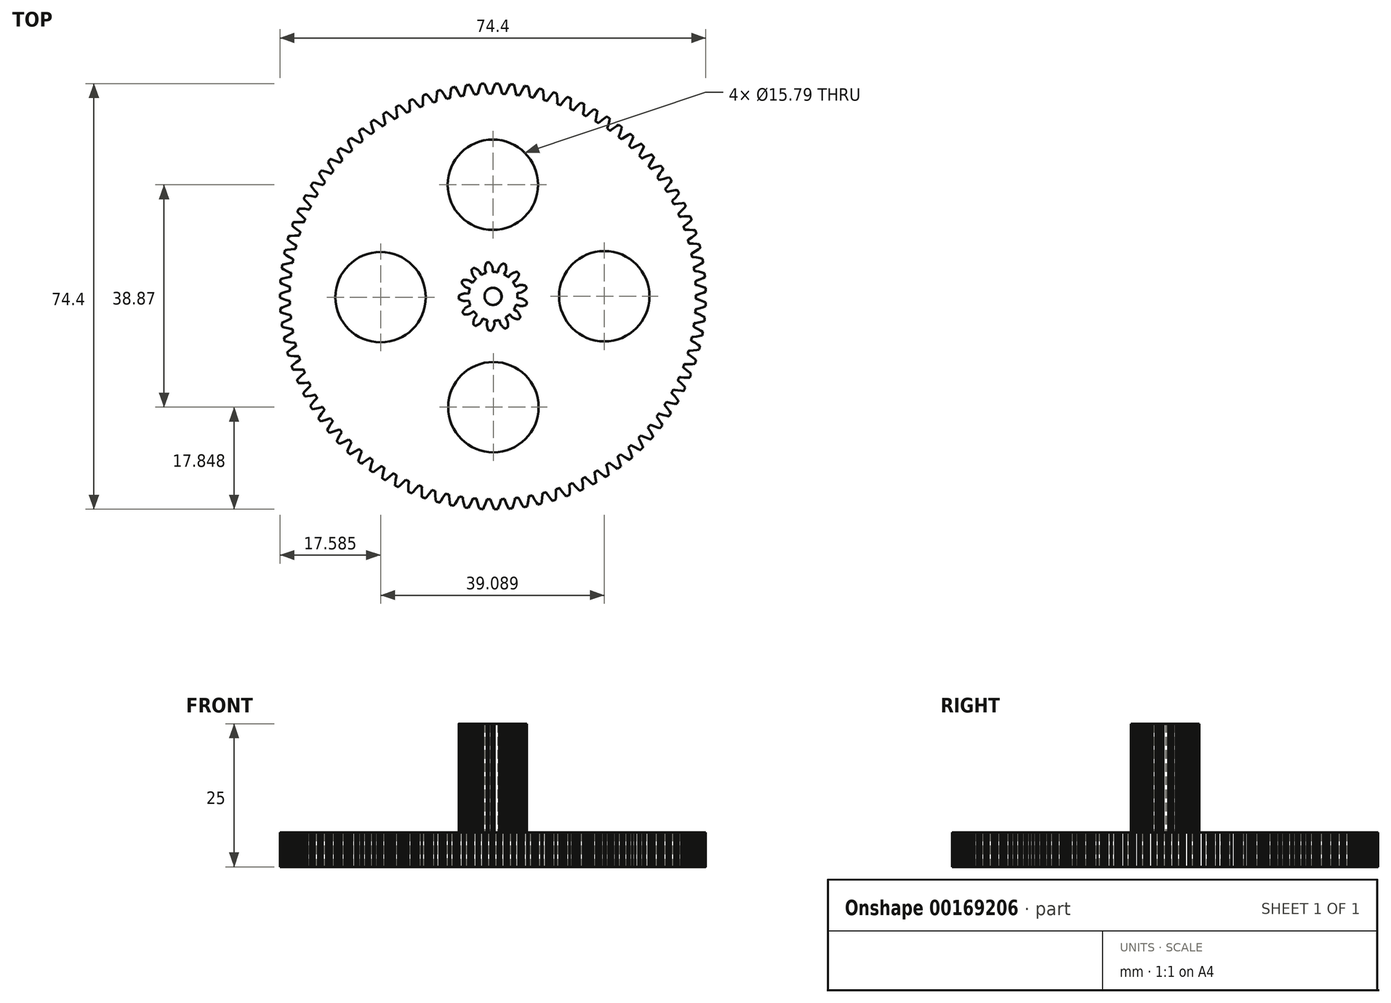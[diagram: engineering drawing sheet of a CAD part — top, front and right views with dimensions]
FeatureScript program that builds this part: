
annotation { "Feature Type Name" : "Feature", "Feature Type Description" : "" }
export const myFeature = defineFeature(function(context is Context, id is Id, definition is map)
    precondition{}
    {
        {
            assignVariable(context, id + "F0", {"name" : "Gear1", "anyValue" : 25});
        }
        {
            var Q0;
            Q0=qCreatedBy(makeId("Top.planeOp"),FACE);
            var sketch = newSketch(context, id + "F1", { "sketchPlane" : qUnion([Q0])});
            skCircle(sketch, "E0", {"center": v(0, 0) * mm, "radius": 1.5 * mm});
            skLineSegment(sketch, "E1", {"start": v(27.62, 22.27) * mm, "end": v(27.85, 22.37) * mm});
            skLineSegment(sketch, "E2", {"start": v(27.85, 22.37) * mm, "end": v(28.37, 22.56) * mm});
            skLineSegment(sketch, "E3", {"start": v(28.37, 22.56) * mm, "end": v(28.98, 22.76) * mm});
            skLineSegment(sketch, "E4", {"start": v(28.98, 22.76) * mm, "end": v(29.35, 22.86) * mm});
            skArc(sketch, "E5", {"start": v(29.35, 22.86) * mm, "mid": v(29.55, 22.6) * mm, "end": v(29.74, 22.35) * mm});
            skLineSegment(sketch, "E6", {"start": v(29.74, 22.35) * mm, "end": v(29.55, 22.01) * mm});
            skLineSegment(sketch, "E7", {"start": v(29.55, 22.01) * mm, "end": v(29.2, 21.47) * mm});
            skLineSegment(sketch, "E8", {"start": v(29.2, 21.47) * mm, "end": v(28.87, 21.02) * mm});
            skLineSegment(sketch, "E9", {"start": v(28.87, 21.02) * mm, "end": v(28.72, 20.83) * mm});
            skArc(sketch, "E10", {"start": v(28.72, 20.83) * mm, "mid": v(28.9, 20.57) * mm, "end": v(29.1, 20.3) * mm});
            skLineSegment(sketch, "E11", {"start": v(29.1, 20.3) * mm, "end": v(29.32, 20.4) * mm});
            skLineSegment(sketch, "E12", {"start": v(29.32, 20.4) * mm, "end": v(29.85, 20.55) * mm});
            skLineSegment(sketch, "E13", {"start": v(29.85, 20.55) * mm, "end": v(30.48, 20.7) * mm});
            skLineSegment(sketch, "E14", {"start": v(30.48, 20.7) * mm, "end": v(30.86, 20.78) * mm});
            skArc(sketch, "E15", {"start": v(30.86, 20.78) * mm, "mid": v(31.04, 20.51) * mm, "end": v(31.21, 20.24) * mm});
            skLineSegment(sketch, "E16", {"start": v(31.21, 20.24) * mm, "end": v(31, 19.92) * mm});
            skLineSegment(sketch, "E17", {"start": v(31, 19.92) * mm, "end": v(30.61, 19.4) * mm});
            skLineSegment(sketch, "E18", {"start": v(30.61, 19.4) * mm, "end": v(30.26, 18.98) * mm});
            skLineSegment(sketch, "E19", {"start": v(30.26, 18.98) * mm, "end": v(30.09, 18.8) * mm});
            skArc(sketch, "E20", {"start": v(30.09, 18.8) * mm, "mid": v(30.26, 18.53) * mm, "end": v(30.42, 18.25) * mm});
            skLineSegment(sketch, "E21", {"start": v(30.42, 18.25) * mm, "end": v(30.66, 18.32) * mm});
            skLineSegment(sketch, "E22", {"start": v(30.66, 18.32) * mm, "end": v(31.2, 18.44) * mm});
            skLineSegment(sketch, "E23", {"start": v(31.2, 18.44) * mm, "end": v(31.83, 18.55) * mm});
            skLineSegment(sketch, "E24", {"start": v(31.83, 18.55) * mm, "end": v(32.22, 18.6) * mm});
            skArc(sketch, "E25", {"start": v(32.22, 18.6) * mm, "mid": v(32.38, 18.32) * mm, "end": v(32.54, 18.04) * mm});
            skLineSegment(sketch, "E26", {"start": v(32.54, 18.04) * mm, "end": v(32.3, 17.73) * mm});
            skLineSegment(sketch, "E27", {"start": v(32.3, 17.73) * mm, "end": v(31.88, 17.25) * mm});
            skLineSegment(sketch, "E28", {"start": v(31.88, 17.25) * mm, "end": v(31.5, 16.85) * mm});
            skLineSegment(sketch, "E29", {"start": v(31.5, 16.85) * mm, "end": v(31.31, 16.68) * mm});
            skArc(sketch, "E30", {"start": v(31.31, 16.68) * mm, "mid": v(31.46, 16.4) * mm, "end": v(31.6, 16.11) * mm});
            skLineSegment(sketch, "E31", {"start": v(31.6, 16.11) * mm, "end": v(31.85, 16.16) * mm});
            skLineSegment(sketch, "E32", {"start": v(31.85, 16.16) * mm, "end": v(32.4, 16.25) * mm});
            skLineSegment(sketch, "E33", {"start": v(32.4, 16.25) * mm, "end": v(33.04, 16.31) * mm});
            skLineSegment(sketch, "E34", {"start": v(33.04, 16.31) * mm, "end": v(33.43, 16.33) * mm});
            skArc(sketch, "E35", {"start": v(33.43, 16.33) * mm, "mid": v(33.57, 16.04) * mm, "end": v(33.7, 15.76) * mm});
            skLineSegment(sketch, "E36", {"start": v(33.7, 15.76) * mm, "end": v(33.44, 15.46) * mm});
            skLineSegment(sketch, "E37", {"start": v(33.44, 15.46) * mm, "end": v(33, 15) * mm});
            skLineSegment(sketch, "E38", {"start": v(33, 15) * mm, "end": v(32.58, 14.63) * mm});
            skLineSegment(sketch, "E39", {"start": v(32.58, 14.63) * mm, "end": v(32.4, 14.48) * mm});
            skArc(sketch, "E40", {"start": v(32.4, 14.48) * mm, "mid": v(32.52, 14.19) * mm, "end": v(32.65, 13.9) * mm});
            skLineSegment(sketch, "E41", {"start": v(32.65, 13.9) * mm, "end": v(32.89, 13.93) * mm});
            skLineSegment(sketch, "E42", {"start": v(32.89, 13.93) * mm, "end": v(33.44, 13.97) * mm});
            skLineSegment(sketch, "E43", {"start": v(33.44, 13.97) * mm, "end": v(34.08, 14) * mm});
            skLineSegment(sketch, "E44", {"start": v(34.08, 14) * mm, "end": v(34.48, 13.99) * mm});
            skArc(sketch, "E45", {"start": v(34.48, 13.99) * mm, "mid": v(34.6, 13.7) * mm, "end": v(34.71, 13.4) * mm});
            skLineSegment(sketch, "E46", {"start": v(34.71, 13.4) * mm, "end": v(34.43, 13.12) * mm});
            skLineSegment(sketch, "E47", {"start": v(34.43, 13.12) * mm, "end": v(33.95, 12.7) * mm});
            skLineSegment(sketch, "E48", {"start": v(33.95, 12.7) * mm, "end": v(33.51, 12.35) * mm});
            skLineSegment(sketch, "E49", {"start": v(33.51, 12.35) * mm, "end": v(33.31, 12.2) * mm});
            skArc(sketch, "E50", {"start": v(33.31, 12.2) * mm, "mid": v(33.42, 11.9) * mm, "end": v(33.53, 11.6) * mm});
            skLineSegment(sketch, "E51", {"start": v(33.53, 11.6) * mm, "end": v(33.77, 11.62) * mm});
            skLineSegment(sketch, "E52", {"start": v(33.77, 11.62) * mm, "end": v(34.33, 11.63) * mm});
            skLineSegment(sketch, "E53", {"start": v(34.33, 11.63) * mm, "end": v(34.97, 11.61) * mm});
            skLineSegment(sketch, "E54", {"start": v(34.97, 11.61) * mm, "end": v(35.36, 11.58) * mm});
            skArc(sketch, "E55", {"start": v(35.36, 11.58) * mm, "mid": v(35.46, 11.27) * mm, "end": v(35.55, 10.97) * mm});
            skLineSegment(sketch, "E56", {"start": v(35.55, 10.97) * mm, "end": v(35.25, 10.71) * mm});
            skLineSegment(sketch, "E57", {"start": v(35.25, 10.71) * mm, "end": v(34.74, 10.33) * mm});
            skLineSegment(sketch, "E58", {"start": v(34.74, 10.33) * mm, "end": v(34.28, 10.01) * mm});
            skLineSegment(sketch, "E59", {"start": v(34.28, 10.01) * mm, "end": v(34.08, 9.88) * mm});
            skArc(sketch, "E60", {"start": v(34.08, 9.88) * mm, "mid": v(34.16, 9.58) * mm, "end": v(34.25, 9.27) * mm});
            skLineSegment(sketch, "E61", {"start": v(34.25, 9.27) * mm, "end": v(34.5, 9.27) * mm});
            skLineSegment(sketch, "E62", {"start": v(34.5, 9.27) * mm, "end": v(35.05, 9.24) * mm});
            skLineSegment(sketch, "E63", {"start": v(35.05, 9.24) * mm, "end": v(35.69, 9.17) * mm});
            skLineSegment(sketch, "E64", {"start": v(35.69, 9.17) * mm, "end": v(36.07, 9.11) * mm});
            skArc(sketch, "E65", {"start": v(36.07, 9.11) * mm, "mid": v(36.15, 8.8) * mm, "end": v(36.22, 8.49) * mm});
            skLineSegment(sketch, "E66", {"start": v(36.22, 8.49) * mm, "end": v(35.9, 8.26) * mm});
            skLineSegment(sketch, "E67", {"start": v(35.9, 8.26) * mm, "end": v(35.37, 7.9) * mm});
            skLineSegment(sketch, "E68", {"start": v(35.37, 7.9) * mm, "end": v(34.9, 7.62) * mm});
            skLineSegment(sketch, "E69", {"start": v(34.9, 7.62) * mm, "end": v(34.68, 7.5) * mm});
            skArc(sketch, "E70", {"start": v(34.68, 7.5) * mm, "mid": v(34.74, 7.2) * mm, "end": v(34.8, 6.88) * mm});
            skLineSegment(sketch, "E71", {"start": v(34.8, 6.88) * mm, "end": v(35.05, 6.87) * mm});
            skLineSegment(sketch, "E72", {"start": v(35.05, 6.87) * mm, "end": v(35.6, 6.8) * mm});
            skLineSegment(sketch, "E73", {"start": v(35.6, 6.8) * mm, "end": v(36.23, 6.69) * mm});
            skLineSegment(sketch, "E74", {"start": v(36.23, 6.69) * mm, "end": v(36.61, 6.6) * mm});
            skArc(sketch, "E75", {"start": v(36.61, 6.6) * mm, "mid": v(36.67, 6.28) * mm, "end": v(36.72, 5.97) * mm});
            skLineSegment(sketch, "E76", {"start": v(36.72, 5.97) * mm, "end": v(36.4, 5.76) * mm});
            skLineSegment(sketch, "E77", {"start": v(36.4, 5.76) * mm, "end": v(35.83, 5.45) * mm});
            skLineSegment(sketch, "E78", {"start": v(35.83, 5.45) * mm, "end": v(35.34, 5.2) * mm});
            skLineSegment(sketch, "E79", {"start": v(35.34, 5.2) * mm, "end": v(35.11, 5.1) * mm});
            skArc(sketch, "E80", {"start": v(35.11, 5.1) * mm, "mid": v(35.16, 4.78) * mm, "end": v(35.2, 4.47) * mm});
            skLineSegment(sketch, "E81", {"start": v(35.2, 4.47) * mm, "end": v(35.44, 4.43) * mm});
            skLineSegment(sketch, "E82", {"start": v(35.44, 4.43) * mm, "end": v(35.99, 4.33) * mm});
            skLineSegment(sketch, "E83", {"start": v(35.99, 4.33) * mm, "end": v(36.6, 4.17) * mm});
            skLineSegment(sketch, "E84", {"start": v(36.6, 4.17) * mm, "end": v(36.98, 4.06) * mm});
            skArc(sketch, "E85", {"start": v(36.98, 4.06) * mm, "mid": v(37.02, 3.74) * mm, "end": v(37.05, 3.42) * mm});
            skLineSegment(sketch, "E86", {"start": v(37.05, 3.42) * mm, "end": v(36.7, 3.24) * mm});
            skLineSegment(sketch, "E87", {"start": v(36.7, 3.24) * mm, "end": v(36.12, 2.96) * mm});
            skLineSegment(sketch, "E88", {"start": v(36.12, 2.96) * mm, "end": v(35.61, 2.75) * mm});
            skLineSegment(sketch, "E89", {"start": v(35.61, 2.75) * mm, "end": v(35.38, 2.66) * mm});
            skArc(sketch, "E90", {"start": v(35.38, 2.66) * mm, "mid": v(35.4, 2.35) * mm, "end": v(35.42, 2.03) * mm});
            skLineSegment(sketch, "E91", {"start": v(35.42, 2.03) * mm, "end": v(35.66, 1.98) * mm});
            skLineSegment(sketch, "E92", {"start": v(35.66, 1.98) * mm, "end": v(36.2, 1.83) * mm});
            skLineSegment(sketch, "E93", {"start": v(36.2, 1.83) * mm, "end": v(36.8, 1.64) * mm});
            skLineSegment(sketch, "E94", {"start": v(36.8, 1.64) * mm, "end": v(37.17, 1.5) * mm});
            skArc(sketch, "E95", {"start": v(37.17, 1.5) * mm, "mid": v(37.19, 1.18) * mm, "end": v(37.2, 0.86) * mm});
            skLineSegment(sketch, "E96", {"start": v(37.2, 0.86) * mm, "end": v(36.84, 0.7) * mm});
            skLineSegment(sketch, "E97", {"start": v(36.84, 0.7) * mm, "end": v(36.24, 0.46) * mm});
            skLineSegment(sketch, "E98", {"start": v(36.24, 0.46) * mm, "end": v(35.71, 0.28) * mm});
            skLineSegment(sketch, "E99", {"start": v(35.71, 0.28) * mm, "end": v(35.48, 0.22) * mm});
            skArc(sketch, "E100", {"start": v(35.48, 0.22) * mm, "mid": v(35.48, -0.1) * mm, "end": v(35.48, -0.42) * mm});
            skLineSegment(sketch, "E101", {"start": v(35.48, -0.42) * mm, "end": v(35.71, -0.49) * mm});
            skLineSegment(sketch, "E102", {"start": v(35.71, -0.49) * mm, "end": v(36.24, -0.67) * mm});
            skLineSegment(sketch, "E103", {"start": v(36.24, -0.67) * mm, "end": v(36.83, -0.9) * mm});
            skLineSegment(sketch, "E104", {"start": v(36.83, -0.9) * mm, "end": v(37.19, -1.07) * mm});
            skArc(sketch, "E105", {"start": v(37.19, -1.07) * mm, "mid": v(37.18, -1.4) * mm, "end": v(37.17, -1.71) * mm});
            skLineSegment(sketch, "E106", {"start": v(37.17, -1.71) * mm, "end": v(36.8, -1.85) * mm});
            skLineSegment(sketch, "E107", {"start": v(36.8, -1.85) * mm, "end": v(36.19, -2.04) * mm});
            skLineSegment(sketch, "E108", {"start": v(36.19, -2.04) * mm, "end": v(35.65, -2.18) * mm});
            skLineSegment(sketch, "E109", {"start": v(35.65, -2.18) * mm, "end": v(35.4, -2.23) * mm});
            skArc(sketch, "E110", {"start": v(35.4, -2.23) * mm, "mid": v(35.39, -2.55) * mm, "end": v(35.36, -2.87) * mm});
            skLineSegment(sketch, "E111", {"start": v(35.36, -2.87) * mm, "end": v(35.6, -2.95) * mm});
            skLineSegment(sketch, "E112", {"start": v(35.6, -2.95) * mm, "end": v(36.1, -3.17) * mm});
            skLineSegment(sketch, "E113", {"start": v(36.1, -3.17) * mm, "end": v(36.68, -3.45) * mm});
            skLineSegment(sketch, "E114", {"start": v(36.68, -3.45) * mm, "end": v(37.03, -3.63) * mm});
            skArc(sketch, "E115", {"start": v(37.03, -3.63) * mm, "mid": v(37, -3.95) * mm, "end": v(36.96, -4.27) * mm});
            skLineSegment(sketch, "E116", {"start": v(36.96, -4.27) * mm, "end": v(36.58, -4.38) * mm});
            skLineSegment(sketch, "E117", {"start": v(36.58, -4.38) * mm, "end": v(35.96, -4.53) * mm});
            skLineSegment(sketch, "E118", {"start": v(35.96, -4.53) * mm, "end": v(35.41, -4.63) * mm});
            skLineSegment(sketch, "E119", {"start": v(35.41, -4.63) * mm, "end": v(35.17, -4.67) * mm});
            skArc(sketch, "E120", {"start": v(35.17, -4.67) * mm, "mid": v(35.13, -4.98) * mm, "end": v(35.08, -5.3) * mm});
            skLineSegment(sketch, "E121", {"start": v(35.08, -5.3) * mm, "end": v(35.3, -5.4) * mm});
            skLineSegment(sketch, "E122", {"start": v(35.3, -5.4) * mm, "end": v(35.8, -5.65) * mm});
            skLineSegment(sketch, "E123", {"start": v(35.8, -5.65) * mm, "end": v(36.36, -5.97) * mm});
            skLineSegment(sketch, "E124", {"start": v(36.36, -5.97) * mm, "end": v(36.69, -6.18) * mm});
            skArc(sketch, "E125", {"start": v(36.69, -6.18) * mm, "mid": v(36.63, -6.5) * mm, "end": v(36.58, -6.8) * mm});
            skLineSegment(sketch, "E126", {"start": v(36.58, -6.8) * mm, "end": v(36.2, -6.9) * mm});
            skLineSegment(sketch, "E127", {"start": v(36.2, -6.9) * mm, "end": v(35.56, -7) * mm});
            skLineSegment(sketch, "E128", {"start": v(35.56, -7) * mm, "end": v(35, -7.07) * mm});
            skLineSegment(sketch, "E129", {"start": v(35, -7.07) * mm, "end": v(34.76, -7.08) * mm});
            skArc(sketch, "E130", {"start": v(34.76, -7.08) * mm, "mid": v(34.7, -7.4) * mm, "end": v(34.63, -7.7) * mm});
            skLineSegment(sketch, "E131", {"start": v(34.63, -7.7) * mm, "end": v(34.85, -7.82) * mm});
            skLineSegment(sketch, "E132", {"start": v(34.85, -7.82) * mm, "end": v(35.33, -8.1) * mm});
            skLineSegment(sketch, "E133", {"start": v(35.33, -8.1) * mm, "end": v(35.86, -8.46) * mm});
            skLineSegment(sketch, "E134", {"start": v(35.86, -8.46) * mm, "end": v(36.17, -8.7) * mm});
            skArc(sketch, "E135", {"start": v(36.17, -8.7) * mm, "mid": v(36.1, -9) * mm, "end": v(36.02, -9.32) * mm});
            skLineSegment(sketch, "E136", {"start": v(36.02, -9.32) * mm, "end": v(35.63, -9.37) * mm});
            skLineSegment(sketch, "E137", {"start": v(35.63, -9.37) * mm, "end": v(35, -9.44) * mm});
            skLineSegment(sketch, "E138", {"start": v(35, -9.44) * mm, "end": v(34.44, -9.46) * mm});
            skLineSegment(sketch, "E139", {"start": v(34.44, -9.46) * mm, "end": v(34.2, -9.46) * mm});
            skArc(sketch, "E140", {"start": v(34.2, -9.46) * mm, "mid": v(34.1, -9.77) * mm, "end": v(34.02, -10.08) * mm});
            skLineSegment(sketch, "E141", {"start": v(34.02, -10.08) * mm, "end": v(34.23, -10.2) * mm});
            skLineSegment(sketch, "E142", {"start": v(34.23, -10.2) * mm, "end": v(34.68, -10.52) * mm});
            skLineSegment(sketch, "E143", {"start": v(34.68, -10.52) * mm, "end": v(35.2, -10.91) * mm});
            skLineSegment(sketch, "E144", {"start": v(35.2, -10.91) * mm, "end": v(35.49, -11.17) * mm});
            skArc(sketch, "E145", {"start": v(35.49, -11.17) * mm, "mid": v(35.4, -11.47) * mm, "end": v(35.3, -11.78) * mm});
            skLineSegment(sketch, "E146", {"start": v(35.3, -11.78) * mm, "end": v(34.9, -11.8) * mm});
            skLineSegment(sketch, "E147", {"start": v(34.9, -11.8) * mm, "end": v(34.26, -11.83) * mm});
            skLineSegment(sketch, "E148", {"start": v(34.26, -11.83) * mm, "end": v(33.7, -11.82) * mm});
            skLineSegment(sketch, "E149", {"start": v(33.7, -11.82) * mm, "end": v(33.46, -11.8) * mm});
            skArc(sketch, "E150", {"start": v(33.46, -11.8) * mm, "mid": v(33.35, -12.1) * mm, "end": v(33.24, -12.4) * mm});
            skLineSegment(sketch, "E151", {"start": v(33.24, -12.4) * mm, "end": v(33.44, -12.54) * mm});
            skLineSegment(sketch, "E152", {"start": v(33.44, -12.54) * mm, "end": v(33.87, -12.9) * mm});
            skLineSegment(sketch, "E153", {"start": v(33.87, -12.9) * mm, "end": v(34.35, -13.32) * mm});
            skLineSegment(sketch, "E154", {"start": v(34.35, -13.32) * mm, "end": v(34.63, -13.6) * mm});
            skArc(sketch, "E155", {"start": v(34.63, -13.6) * mm, "mid": v(34.51, -13.89) * mm, "end": v(34.4, -14.18) * mm});
            skLineSegment(sketch, "E156", {"start": v(34.4, -14.18) * mm, "end": v(34, -14.19) * mm});
            skLineSegment(sketch, "E157", {"start": v(34, -14.19) * mm, "end": v(33.36, -14.16) * mm});
            skLineSegment(sketch, "E158", {"start": v(33.36, -14.16) * mm, "end": v(32.8, -14.11) * mm});
            skLineSegment(sketch, "E159", {"start": v(32.8, -14.11) * mm, "end": v(32.56, -14.08) * mm});
            skArc(sketch, "E160", {"start": v(32.56, -14.08) * mm, "mid": v(32.44, -14.37) * mm, "end": v(32.3, -14.66) * mm});
            skLineSegment(sketch, "E161", {"start": v(32.3, -14.66) * mm, "end": v(32.5, -14.82) * mm});
            skLineSegment(sketch, "E162", {"start": v(32.5, -14.82) * mm, "end": v(32.9, -15.2) * mm});
            skLineSegment(sketch, "E163", {"start": v(32.9, -15.2) * mm, "end": v(33.35, -15.65) * mm});
            skLineSegment(sketch, "E164", {"start": v(33.35, -15.65) * mm, "end": v(33.61, -15.95) * mm});
            skArc(sketch, "E165", {"start": v(33.61, -15.95) * mm, "mid": v(33.47, -16.24) * mm, "end": v(33.33, -16.52) * mm});
            skLineSegment(sketch, "E166", {"start": v(33.33, -16.52) * mm, "end": v(32.94, -16.5) * mm});
            skLineSegment(sketch, "E167", {"start": v(32.94, -16.5) * mm, "end": v(32.3, -16.43) * mm});
            skLineSegment(sketch, "E168", {"start": v(32.3, -16.43) * mm, "end": v(31.76, -16.34) * mm});
            skLineSegment(sketch, "E169", {"start": v(31.76, -16.34) * mm, "end": v(31.52, -16.3) * mm});
            skArc(sketch, "E170", {"start": v(31.52, -16.3) * mm, "mid": v(31.37, -16.58) * mm, "end": v(31.22, -16.86) * mm});
            skLineSegment(sketch, "E171", {"start": v(31.22, -16.86) * mm, "end": v(31.4, -17.03) * mm});
            skLineSegment(sketch, "E172", {"start": v(31.4, -17.03) * mm, "end": v(31.78, -17.43) * mm});
            skLineSegment(sketch, "E173", {"start": v(31.78, -17.43) * mm, "end": v(32.2, -17.92) * mm});
            skLineSegment(sketch, "E174", {"start": v(32.2, -17.92) * mm, "end": v(32.43, -18.23) * mm});
            skArc(sketch, "E175", {"start": v(32.43, -18.23) * mm, "mid": v(32.27, -18.5) * mm, "end": v(32.11, -18.78) * mm});
            skLineSegment(sketch, "E176", {"start": v(32.11, -18.78) * mm, "end": v(31.73, -18.73) * mm});
            skLineSegment(sketch, "E177", {"start": v(31.73, -18.73) * mm, "end": v(31.1, -18.62) * mm});
            skLineSegment(sketch, "E178", {"start": v(31.1, -18.62) * mm, "end": v(30.55, -18.5) * mm});
            skLineSegment(sketch, "E179", {"start": v(30.55, -18.5) * mm, "end": v(30.32, -18.43) * mm});
            skArc(sketch, "E180", {"start": v(30.32, -18.43) * mm, "mid": v(30.15, -18.7) * mm, "end": v(29.98, -18.97) * mm});
            skLineSegment(sketch, "E181", {"start": v(29.98, -18.97) * mm, "end": v(30.15, -19.15) * mm});
            skLineSegment(sketch, "E182", {"start": v(30.15, -19.15) * mm, "end": v(30.5, -19.58) * mm});
            skLineSegment(sketch, "E183", {"start": v(30.5, -19.58) * mm, "end": v(30.88, -20.1) * mm});
            skLineSegment(sketch, "E184", {"start": v(30.88, -20.1) * mm, "end": v(31.1, -20.42) * mm});
            skArc(sketch, "E185", {"start": v(31.1, -20.42) * mm, "mid": v(30.92, -20.69) * mm, "end": v(30.74, -20.95) * mm});
            skLineSegment(sketch, "E186", {"start": v(30.74, -20.95) * mm, "end": v(30.36, -20.88) * mm});
            skLineSegment(sketch, "E187", {"start": v(30.36, -20.88) * mm, "end": v(29.74, -20.72) * mm});
            skLineSegment(sketch, "E188", {"start": v(29.74, -20.72) * mm, "end": v(29.2, -20.56) * mm});
            skLineSegment(sketch, "E189", {"start": v(29.2, -20.56) * mm, "end": v(28.97, -20.48) * mm});
            skArc(sketch, "E190", {"start": v(28.97, -20.48) * mm, "mid": v(28.79, -20.73) * mm, "end": v(28.6, -21) * mm});
            skLineSegment(sketch, "E191", {"start": v(28.6, -21) * mm, "end": v(28.75, -21.18) * mm});
            skLineSegment(sketch, "E192", {"start": v(28.75, -21.18) * mm, "end": v(29.07, -21.64) * mm});
            skLineSegment(sketch, "E193", {"start": v(29.07, -21.64) * mm, "end": v(29.42, -22.18) * mm});
            skLineSegment(sketch, "E194", {"start": v(29.42, -22.18) * mm, "end": v(29.61, -22.52) * mm});
            skArc(sketch, "E195", {"start": v(29.61, -22.52) * mm, "mid": v(29.42, -22.77) * mm, "end": v(29.22, -23.02) * mm});
            skLineSegment(sketch, "E196", {"start": v(29.22, -23.02) * mm, "end": v(28.84, -22.92) * mm});
            skLineSegment(sketch, "E197", {"start": v(28.84, -22.92) * mm, "end": v(28.23, -22.72) * mm});
            skLineSegment(sketch, "E198", {"start": v(28.23, -22.72) * mm, "end": v(27.72, -22.52) * mm});
            skLineSegment(sketch, "E199", {"start": v(27.72, -22.52) * mm, "end": v(27.5, -22.43) * mm});
            skArc(sketch, "E200", {"start": v(27.5, -22.43) * mm, "mid": v(27.29, -22.67) * mm, "end": v(27.08, -22.92) * mm});
            skLineSegment(sketch, "E201", {"start": v(27.08, -22.92) * mm, "end": v(27.22, -23.12) * mm});
            skLineSegment(sketch, "E202", {"start": v(27.22, -23.12) * mm, "end": v(27.51, -23.6) * mm});
            skLineSegment(sketch, "E203", {"start": v(27.51, -23.6) * mm, "end": v(27.82, -24.15) * mm});
            skLineSegment(sketch, "E204", {"start": v(27.82, -24.15) * mm, "end": v(28, -24.5) * mm});
            skArc(sketch, "E205", {"start": v(28, -24.5) * mm, "mid": v(27.78, -24.75) * mm, "end": v(27.56, -24.99) * mm});
            skLineSegment(sketch, "E206", {"start": v(27.56, -24.99) * mm, "end": v(27.2, -24.86) * mm});
            skLineSegment(sketch, "E207", {"start": v(27.2, -24.86) * mm, "end": v(26.6, -24.62) * mm});
            skLineSegment(sketch, "E208", {"start": v(26.6, -24.62) * mm, "end": v(26.1, -24.38) * mm});
            skLineSegment(sketch, "E209", {"start": v(26.1, -24.38) * mm, "end": v(25.88, -24.27) * mm});
            skArc(sketch, "E210", {"start": v(25.88, -24.27) * mm, "mid": v(25.66, -24.5) * mm, "end": v(25.44, -24.73) * mm});
            skLineSegment(sketch, "E211", {"start": v(25.44, -24.73) * mm, "end": v(25.56, -24.94) * mm});
            skLineSegment(sketch, "E212", {"start": v(25.56, -24.94) * mm, "end": v(25.82, -25.43) * mm});
            skLineSegment(sketch, "E213", {"start": v(25.82, -25.43) * mm, "end": v(26.09, -26.02) * mm});
            skLineSegment(sketch, "E214", {"start": v(26.09, -26.02) * mm, "end": v(26.23, -26.38) * mm});
            skArc(sketch, "E215", {"start": v(26.23, -26.38) * mm, "mid": v(26, -26.6) * mm, "end": v(25.77, -26.83) * mm});
            skLineSegment(sketch, "E216", {"start": v(25.77, -26.83) * mm, "end": v(25.41, -26.67) * mm});
            skLineSegment(sketch, "E217", {"start": v(25.41, -26.67) * mm, "end": v(24.84, -26.4) * mm});
            skLineSegment(sketch, "E218", {"start": v(24.84, -26.4) * mm, "end": v(24.35, -26.12) * mm});
            skLineSegment(sketch, "E219", {"start": v(24.35, -26.12) * mm, "end": v(24.14, -26) * mm});
            skArc(sketch, "E220", {"start": v(24.14, -26) * mm, "mid": v(23.9, -26.21) * mm, "end": v(23.67, -26.42) * mm});
            skLineSegment(sketch, "E221", {"start": v(23.67, -26.42) * mm, "end": v(23.78, -26.64) * mm});
            skLineSegment(sketch, "E222", {"start": v(23.78, -26.64) * mm, "end": v(24, -27.15) * mm});
            skLineSegment(sketch, "E223", {"start": v(24, -27.15) * mm, "end": v(24.23, -27.75) * mm});
            skLineSegment(sketch, "E224", {"start": v(24.23, -27.75) * mm, "end": v(24.35, -28.13) * mm});
            skArc(sketch, "E225", {"start": v(24.35, -28.13) * mm, "mid": v(24.1, -28.33) * mm, "end": v(23.86, -28.54) * mm});
            skLineSegment(sketch, "E226", {"start": v(23.86, -28.54) * mm, "end": v(23.51, -28.36) * mm});
            skLineSegment(sketch, "E227", {"start": v(23.51, -28.36) * mm, "end": v(22.96, -28.04) * mm});
            skLineSegment(sketch, "E228", {"start": v(22.96, -28.04) * mm, "end": v(22.5, -27.74) * mm});
            skLineSegment(sketch, "E229", {"start": v(22.5, -27.74) * mm, "end": v(22.3, -27.6) * mm});
            skArc(sketch, "E230", {"start": v(22.3, -27.6) * mm, "mid": v(22.04, -27.8) * mm, "end": v(21.8, -28) * mm});
            skLineSegment(sketch, "E231", {"start": v(21.8, -28) * mm, "end": v(21.89, -28.22) * mm});
            skLineSegment(sketch, "E232", {"start": v(21.89, -28.22) * mm, "end": v(22.07, -28.74) * mm});
            skLineSegment(sketch, "E233", {"start": v(22.07, -28.74) * mm, "end": v(22.26, -29.36) * mm});
            skLineSegment(sketch, "E234", {"start": v(22.26, -29.36) * mm, "end": v(22.35, -29.74) * mm});
            skArc(sketch, "E235", {"start": v(22.35, -29.74) * mm, "mid": v(22.1, -29.93) * mm, "end": v(21.84, -30.12) * mm});
            skLineSegment(sketch, "E236", {"start": v(21.84, -30.12) * mm, "end": v(21.5, -29.92) * mm});
            skLineSegment(sketch, "E237", {"start": v(21.5, -29.92) * mm, "end": v(20.97, -29.56) * mm});
            skLineSegment(sketch, "E238", {"start": v(20.97, -29.56) * mm, "end": v(20.52, -29.23) * mm});
            skLineSegment(sketch, "E239", {"start": v(20.52, -29.23) * mm, "end": v(20.33, -29.07) * mm});
            skArc(sketch, "E240", {"start": v(20.33, -29.07) * mm, "mid": v(20.07, -29.25) * mm, "end": v(19.8, -29.43) * mm});
            skLineSegment(sketch, "E241", {"start": v(19.8, -29.43) * mm, "end": v(19.89, -29.66) * mm});
            skLineSegment(sketch, "E242", {"start": v(19.89, -29.66) * mm, "end": v(20.04, -30.2) * mm});
            skLineSegment(sketch, "E243", {"start": v(20.04, -30.2) * mm, "end": v(20.18, -30.82) * mm});
            skLineSegment(sketch, "E244", {"start": v(20.18, -30.82) * mm, "end": v(20.25, -31.2) * mm});
            skArc(sketch, "E245", {"start": v(20.25, -31.2) * mm, "mid": v(19.98, -31.38) * mm, "end": v(19.7, -31.55) * mm});
            skLineSegment(sketch, "E246", {"start": v(19.7, -31.55) * mm, "end": v(19.39, -31.33) * mm});
            skLineSegment(sketch, "E247", {"start": v(19.39, -31.33) * mm, "end": v(18.88, -30.94) * mm});
            skLineSegment(sketch, "E248", {"start": v(18.88, -30.94) * mm, "end": v(18.46, -30.57) * mm});
            skLineSegment(sketch, "E249", {"start": v(18.46, -30.57) * mm, "end": v(18.28, -30.4) * mm});
            skArc(sketch, "E250", {"start": v(18.28, -30.4) * mm, "mid": v(18, -30.57) * mm, "end": v(17.73, -30.73) * mm});
            skLineSegment(sketch, "E251", {"start": v(17.73, -30.73) * mm, "end": v(17.8, -30.96) * mm});
            skLineSegment(sketch, "E252", {"start": v(17.8, -30.96) * mm, "end": v(17.9, -31.5) * mm});
            skLineSegment(sketch, "E253", {"start": v(17.9, -31.5) * mm, "end": v(18, -32.14) * mm});
            skLineSegment(sketch, "E254", {"start": v(18, -32.14) * mm, "end": v(18.05, -32.53) * mm});
            skArc(sketch, "E255", {"start": v(18.05, -32.53) * mm, "mid": v(17.76, -32.69) * mm, "end": v(17.48, -32.84) * mm});
            skLineSegment(sketch, "E256", {"start": v(17.48, -32.84) * mm, "end": v(17.18, -32.6) * mm});
            skLineSegment(sketch, "E257", {"start": v(17.18, -32.6) * mm, "end": v(16.7, -32.16) * mm});
            skLineSegment(sketch, "E258", {"start": v(16.7, -32.16) * mm, "end": v(16.3, -31.77) * mm});
            skLineSegment(sketch, "E259", {"start": v(16.3, -31.77) * mm, "end": v(16.14, -31.6) * mm});
            skArc(sketch, "E260", {"start": v(16.14, -31.6) * mm, "mid": v(15.85, -31.74) * mm, "end": v(15.57, -31.88) * mm});
            skLineSegment(sketch, "E261", {"start": v(15.57, -31.88) * mm, "end": v(15.61, -32.12) * mm});
            skLineSegment(sketch, "E262", {"start": v(15.61, -32.12) * mm, "end": v(15.69, -32.67) * mm});
            skLineSegment(sketch, "E263", {"start": v(15.69, -32.67) * mm, "end": v(15.74, -33.3) * mm});
            skLineSegment(sketch, "E264", {"start": v(15.74, -33.3) * mm, "end": v(15.76, -33.7) * mm});
            skArc(sketch, "E265", {"start": v(15.76, -33.7) * mm, "mid": v(15.47, -33.83) * mm, "end": v(15.18, -33.97) * mm});
            skLineSegment(sketch, "E266", {"start": v(15.18, -33.97) * mm, "end": v(14.89, -33.7) * mm});
            skLineSegment(sketch, "E267", {"start": v(14.89, -33.7) * mm, "end": v(14.44, -33.24) * mm});
            skLineSegment(sketch, "E268", {"start": v(14.44, -33.24) * mm, "end": v(14.07, -32.82) * mm});
            skLineSegment(sketch, "E269", {"start": v(14.07, -32.82) * mm, "end": v(13.92, -32.63) * mm});
            skArc(sketch, "E270", {"start": v(13.92, -32.63) * mm, "mid": v(13.63, -32.75) * mm, "end": v(13.33, -32.87) * mm});
            skLineSegment(sketch, "E271", {"start": v(13.33, -32.87) * mm, "end": v(13.36, -33.12) * mm});
            skLineSegment(sketch, "E272", {"start": v(13.36, -33.12) * mm, "end": v(13.4, -33.67) * mm});
            skLineSegment(sketch, "E273", {"start": v(13.4, -33.67) * mm, "end": v(13.4, -34.31) * mm});
            skLineSegment(sketch, "E274", {"start": v(13.4, -34.31) * mm, "end": v(13.4, -34.7) * mm});
            skArc(sketch, "E275", {"start": v(13.4, -34.7) * mm, "mid": v(13.1, -34.82) * mm, "end": v(12.8, -34.93) * mm});
            skLineSegment(sketch, "E276", {"start": v(12.8, -34.93) * mm, "end": v(12.53, -34.64) * mm});
            skLineSegment(sketch, "E277", {"start": v(12.53, -34.64) * mm, "end": v(12.11, -34.16) * mm});
            skLineSegment(sketch, "E278", {"start": v(12.11, -34.16) * mm, "end": v(11.78, -33.71) * mm});
            skLineSegment(sketch, "E279", {"start": v(11.78, -33.71) * mm, "end": v(11.64, -33.51) * mm});
            skArc(sketch, "E280", {"start": v(11.64, -33.51) * mm, "mid": v(11.34, -33.62) * mm, "end": v(11.03, -33.72) * mm});
            skLineSegment(sketch, "E281", {"start": v(11.03, -33.72) * mm, "end": v(11.04, -33.96) * mm});
            skLineSegment(sketch, "E282", {"start": v(11.04, -33.96) * mm, "end": v(11.04, -34.52) * mm});
            skLineSegment(sketch, "E283", {"start": v(11.04, -34.52) * mm, "end": v(11, -35.16) * mm});
            skLineSegment(sketch, "E284", {"start": v(11, -35.16) * mm, "end": v(10.97, -35.55) * mm});
            skArc(sketch, "E285", {"start": v(10.97, -35.55) * mm, "mid": v(10.66, -35.64) * mm, "end": v(10.36, -35.73) * mm});
            skLineSegment(sketch, "E286", {"start": v(10.36, -35.73) * mm, "end": v(10.1, -35.43) * mm});
            skLineSegment(sketch, "E287", {"start": v(10.1, -35.43) * mm, "end": v(9.73, -34.9) * mm});
            skLineSegment(sketch, "E288", {"start": v(9.73, -34.9) * mm, "end": v(9.42, -34.45) * mm});
            skLineSegment(sketch, "E289", {"start": v(9.42, -34.45) * mm, "end": v(9.3, -34.23) * mm});
            skArc(sketch, "E290", {"start": v(9.3, -34.23) * mm, "mid": v(8.99, -34.32) * mm, "end": v(8.68, -34.4) * mm});
            skLineSegment(sketch, "E291", {"start": v(8.68, -34.4) * mm, "end": v(8.67, -34.64) * mm});
            skLineSegment(sketch, "E292", {"start": v(8.67, -34.64) * mm, "end": v(8.63, -35.2) * mm});
            skLineSegment(sketch, "E293", {"start": v(8.63, -35.2) * mm, "end": v(8.56, -35.83) * mm});
            skLineSegment(sketch, "E294", {"start": v(8.56, -35.83) * mm, "end": v(8.5, -36.22) * mm});
            skArc(sketch, "E295", {"start": v(8.5, -36.22) * mm, "mid": v(8.18, -36.3) * mm, "end": v(7.87, -36.36) * mm});
            skLineSegment(sketch, "E296", {"start": v(7.87, -36.36) * mm, "end": v(7.64, -36.04) * mm});
            skLineSegment(sketch, "E297", {"start": v(7.64, -36.04) * mm, "end": v(7.3, -35.5) * mm});
            skLineSegment(sketch, "E298", {"start": v(7.3, -35.5) * mm, "end": v(7.02, -35.01) * mm});
            skLineSegment(sketch, "E299", {"start": v(7.02, -35.01) * mm, "end": v(6.91, -34.8) * mm});
            skArc(sketch, "E300", {"start": v(6.91, -34.8) * mm, "mid": v(6.6, -34.86) * mm, "end": v(6.29, -34.91) * mm});
            skLineSegment(sketch, "E301", {"start": v(6.29, -34.91) * mm, "end": v(6.26, -35.16) * mm});
            skLineSegment(sketch, "E302", {"start": v(6.26, -35.16) * mm, "end": v(6.19, -35.7) * mm});
            skLineSegment(sketch, "E303", {"start": v(6.19, -35.7) * mm, "end": v(6.06, -36.34) * mm});
            skLineSegment(sketch, "E304", {"start": v(6.06, -36.34) * mm, "end": v(5.97, -36.72) * mm});
            skArc(sketch, "E305", {"start": v(5.97, -36.72) * mm, "mid": v(5.65, -36.77) * mm, "end": v(5.34, -36.81) * mm});
            skLineSegment(sketch, "E306", {"start": v(5.34, -36.81) * mm, "end": v(5.13, -36.48) * mm});
            skLineSegment(sketch, "E307", {"start": v(5.13, -36.48) * mm, "end": v(4.83, -35.92) * mm});
            skLineSegment(sketch, "E308", {"start": v(4.83, -35.92) * mm, "end": v(4.6, -35.41) * mm});
            skLineSegment(sketch, "E309", {"start": v(4.6, -35.41) * mm, "end": v(4.5, -35.19) * mm});
            skArc(sketch, "E310", {"start": v(4.5, -35.19) * mm, "mid": v(4.18, -35.23) * mm, "end": v(3.86, -35.26) * mm});
            skLineSegment(sketch, "E311", {"start": v(3.86, -35.26) * mm, "end": v(3.82, -35.5) * mm});
            skLineSegment(sketch, "E312", {"start": v(3.82, -35.5) * mm, "end": v(3.7, -36.05) * mm});
            skLineSegment(sketch, "E313", {"start": v(3.7, -36.05) * mm, "end": v(3.54, -36.67) * mm});
            skLineSegment(sketch, "E314", {"start": v(3.54, -36.67) * mm, "end": v(3.42, -37.04) * mm});
            skArc(sketch, "E315", {"start": v(3.42, -37.04) * mm, "mid": v(3.1, -37.07) * mm, "end": v(2.79, -37.1) * mm});
            skLineSegment(sketch, "E316", {"start": v(2.79, -37.1) * mm, "end": v(2.6, -36.75) * mm});
            skLineSegment(sketch, "E317", {"start": v(2.6, -36.75) * mm, "end": v(2.34, -36.16) * mm});
            skLineSegment(sketch, "E318", {"start": v(2.34, -36.16) * mm, "end": v(2.14, -35.65) * mm});
            skLineSegment(sketch, "E319", {"start": v(2.14, -35.65) * mm, "end": v(2.06, -35.41) * mm});
            skArc(sketch, "E320", {"start": v(2.06, -35.41) * mm, "mid": v(1.74, -35.43) * mm, "end": v(1.42, -35.45) * mm});
            skLineSegment(sketch, "E321", {"start": v(1.42, -35.45) * mm, "end": v(1.37, -35.68) * mm});
            skLineSegment(sketch, "E322", {"start": v(1.37, -35.68) * mm, "end": v(1.21, -36.22) * mm});
            skLineSegment(sketch, "E323", {"start": v(1.21, -36.22) * mm, "end": v(1, -36.83) * mm});
            skLineSegment(sketch, "E324", {"start": v(1, -36.83) * mm, "end": v(0.86, -37.19) * mm});
            skArc(sketch, "E325", {"start": v(0.86, -37.19) * mm, "mid": v(0.54, -37.2) * mm, "end": v(0.22, -37.2) * mm});
            skLineSegment(sketch, "E326", {"start": v(0.22, -37.2) * mm, "end": v(0.06, -36.84) * mm});
            skLineSegment(sketch, "E327", {"start": v(0.06, -36.84) * mm, "end": v(-0.16, -36.24) * mm});
            skLineSegment(sketch, "E328", {"start": v(-0.16, -36.24) * mm, "end": v(-0.33, -35.7) * mm});
            skLineSegment(sketch, "E329", {"start": v(-0.33, -35.7) * mm, "end": v(-0.4, -35.47) * mm});
            skArc(sketch, "E330", {"start": v(-0.4, -35.47) * mm, "mid": v(-0.7, -35.47) * mm, "end": v(-1.03, -35.46) * mm});
            skLineSegment(sketch, "E331", {"start": v(-1.03, -35.46) * mm, "end": v(-1.1, -35.7) * mm});
            skLineSegment(sketch, "E332", {"start": v(-1.1, -35.7) * mm, "end": v(-1.29, -36.22) * mm});
            skLineSegment(sketch, "E333", {"start": v(-1.29, -36.22) * mm, "end": v(-1.54, -36.8) * mm});
            skLineSegment(sketch, "E334", {"start": v(-1.54, -36.8) * mm, "end": v(-1.7, -37.16) * mm});
            skArc(sketch, "E335", {"start": v(-1.7, -37.16) * mm, "mid": v(-2.03, -37.14) * mm, "end": v(-2.35, -37.12) * mm});
            skLineSegment(sketch, "E336", {"start": v(-2.35, -37.12) * mm, "end": v(-2.48, -36.76) * mm});
            skLineSegment(sketch, "E337", {"start": v(-2.48, -36.76) * mm, "end": v(-2.66, -36.14) * mm});
            skLineSegment(sketch, "E338", {"start": v(-2.66, -36.14) * mm, "end": v(-2.8, -35.6) * mm});
            skLineSegment(sketch, "E339", {"start": v(-2.8, -35.6) * mm, "end": v(-2.84, -35.36) * mm});
            skArc(sketch, "E340", {"start": v(-2.84, -35.36) * mm, "mid": v(-3.15, -35.33) * mm, "end": v(-3.47, -35.3) * mm});
            skLineSegment(sketch, "E341", {"start": v(-3.47, -35.3) * mm, "end": v(-3.56, -35.53) * mm});
            skLineSegment(sketch, "E342", {"start": v(-3.56, -35.53) * mm, "end": v(-3.79, -36.04) * mm});
            skLineSegment(sketch, "E343", {"start": v(-3.79, -36.04) * mm, "end": v(-4.07, -36.61) * mm});
            skLineSegment(sketch, "E344", {"start": v(-4.07, -36.61) * mm, "end": v(-4.27, -36.95) * mm});
            skArc(sketch, "E345", {"start": v(-4.27, -36.95) * mm, "mid": v(-4.59, -36.91) * mm, "end": v(-4.9, -36.87) * mm});
            skLineSegment(sketch, "E346", {"start": v(-4.9, -36.87) * mm, "end": v(-5, -36.5) * mm});
            skLineSegment(sketch, "E347", {"start": v(-5, -36.5) * mm, "end": v(-5.15, -35.87) * mm});
            skLineSegment(sketch, "E348", {"start": v(-5.15, -35.87) * mm, "end": v(-5.24, -35.32) * mm});
            skLineSegment(sketch, "E349", {"start": v(-5.24, -35.32) * mm, "end": v(-5.27, -35.08) * mm});
            skArc(sketch, "E350", {"start": v(-5.27, -35.08) * mm, "mid": v(-5.58, -35.03) * mm, "end": v(-5.9, -34.98) * mm});
            skLineSegment(sketch, "E351", {"start": v(-5.9, -34.98) * mm, "end": v(-6, -35.2) * mm});
            skLineSegment(sketch, "E352", {"start": v(-6, -35.2) * mm, "end": v(-6.26, -35.7) * mm});
            skLineSegment(sketch, "E353", {"start": v(-6.26, -35.7) * mm, "end": v(-6.6, -36.24) * mm});
            skLineSegment(sketch, "E354", {"start": v(-6.6, -36.24) * mm, "end": v(-6.8, -36.57) * mm});
            skArc(sketch, "E355", {"start": v(-6.8, -36.57) * mm, "mid": v(-7.12, -36.51) * mm, "end": v(-7.44, -36.45) * mm});
            skLineSegment(sketch, "E356", {"start": v(-7.44, -36.45) * mm, "end": v(-7.51, -36.06) * mm});
            skLineSegment(sketch, "E357", {"start": v(-7.51, -36.06) * mm, "end": v(-7.6, -35.43) * mm});
            skLineSegment(sketch, "E358", {"start": v(-7.6, -35.43) * mm, "end": v(-7.67, -34.88) * mm});
            skLineSegment(sketch, "E359", {"start": v(-7.67, -34.88) * mm, "end": v(-7.68, -34.63) * mm});
            skArc(sketch, "E360", {"start": v(-7.68, -34.63) * mm, "mid": v(-7.99, -34.56) * mm, "end": v(-8.3, -34.49) * mm});
            skLineSegment(sketch, "E361", {"start": v(-8.3, -34.49) * mm, "end": v(-8.42, -34.7) * mm});
            skLineSegment(sketch, "E362", {"start": v(-8.42, -34.7) * mm, "end": v(-8.71, -35.17) * mm});
            skLineSegment(sketch, "E363", {"start": v(-8.71, -35.17) * mm, "end": v(-9.08, -35.7) * mm});
            skLineSegment(sketch, "E364", {"start": v(-9.08, -35.7) * mm, "end": v(-9.31, -36.01) * mm});
            skArc(sketch, "E365", {"start": v(-9.31, -36.01) * mm, "mid": v(-9.62, -35.93) * mm, "end": v(-9.93, -35.85) * mm});
            skLineSegment(sketch, "E366", {"start": v(-9.93, -35.85) * mm, "end": v(-9.98, -35.46) * mm});
            skLineSegment(sketch, "E367", {"start": v(-9.98, -35.46) * mm, "end": v(-10.04, -34.82) * mm});
            skLineSegment(sketch, "E368", {"start": v(-10.04, -34.82) * mm, "end": v(-10.05, -34.26) * mm});
            skLineSegment(sketch, "E369", {"start": v(-10.05, -34.26) * mm, "end": v(-10.05, -34.02) * mm});
            skArc(sketch, "E370", {"start": v(-10.05, -34.02) * mm, "mid": v(-10.35, -33.93) * mm, "end": v(-10.66, -33.83) * mm});
            skLineSegment(sketch, "E371", {"start": v(-10.66, -33.83) * mm, "end": v(-10.8, -34.04) * mm});
            skLineSegment(sketch, "E372", {"start": v(-10.8, -34.04) * mm, "end": v(-11.12, -34.49) * mm});
            skLineSegment(sketch, "E373", {"start": v(-11.12, -34.49) * mm, "end": v(-11.52, -35) * mm});
            skLineSegment(sketch, "E374", {"start": v(-11.52, -35) * mm, "end": v(-11.78, -35.28) * mm});
            skArc(sketch, "E375", {"start": v(-11.78, -35.28) * mm, "mid": v(-12.08, -35.18) * mm, "end": v(-12.38, -35.08) * mm});
            skLineSegment(sketch, "E376", {"start": v(-12.38, -35.08) * mm, "end": v(-12.4, -34.69) * mm});
            skLineSegment(sketch, "E377", {"start": v(-12.4, -34.69) * mm, "end": v(-12.41, -34.04) * mm});
            skLineSegment(sketch, "E378", {"start": v(-12.41, -34.04) * mm, "end": v(-12.4, -33.49) * mm});
            skLineSegment(sketch, "E379", {"start": v(-12.4, -33.49) * mm, "end": v(-12.37, -33.24) * mm});
            skArc(sketch, "E380", {"start": v(-12.37, -33.24) * mm, "mid": v(-12.67, -33.13) * mm, "end": v(-12.97, -33.02) * mm});
            skLineSegment(sketch, "E381", {"start": v(-12.97, -33.02) * mm, "end": v(-13.11, -33.21) * mm});
            skLineSegment(sketch, "E382", {"start": v(-13.11, -33.21) * mm, "end": v(-13.47, -33.64) * mm});
            skLineSegment(sketch, "E383", {"start": v(-13.47, -33.64) * mm, "end": v(-13.9, -34.11) * mm});
            skLineSegment(sketch, "E384", {"start": v(-13.9, -34.11) * mm, "end": v(-14.18, -34.39) * mm});
            skArc(sketch, "E385", {"start": v(-14.18, -34.39) * mm, "mid": v(-14.48, -34.26) * mm, "end": v(-14.77, -34.14) * mm});
            skLineSegment(sketch, "E386", {"start": v(-14.77, -34.14) * mm, "end": v(-14.77, -33.75) * mm});
            skLineSegment(sketch, "E387", {"start": v(-14.77, -33.75) * mm, "end": v(-14.73, -33.1) * mm});
            skLineSegment(sketch, "E388", {"start": v(-14.73, -33.1) * mm, "end": v(-14.67, -32.55) * mm});
            skLineSegment(sketch, "E389", {"start": v(-14.67, -32.55) * mm, "end": v(-14.64, -32.31) * mm});
            skArc(sketch, "E390", {"start": v(-14.64, -32.31) * mm, "mid": v(-14.93, -32.18) * mm, "end": v(-15.21, -32.04) * mm});
            skLineSegment(sketch, "E391", {"start": v(-15.21, -32.04) * mm, "end": v(-15.37, -32.23) * mm});
            skLineSegment(sketch, "E392", {"start": v(-15.37, -32.23) * mm, "end": v(-15.76, -32.63) * mm});
            skLineSegment(sketch, "E393", {"start": v(-15.76, -32.63) * mm, "end": v(-16.22, -33.07) * mm});
            skLineSegment(sketch, "E394", {"start": v(-16.22, -33.07) * mm, "end": v(-16.52, -33.33) * mm});
            skArc(sketch, "E395", {"start": v(-16.52, -33.33) * mm, "mid": v(-16.8, -33.18) * mm, "end": v(-17.1, -33.04) * mm});
            skLineSegment(sketch, "E396", {"start": v(-17.1, -33.04) * mm, "end": v(-17.06, -32.65) * mm});
            skLineSegment(sketch, "E397", {"start": v(-17.06, -32.65) * mm, "end": v(-16.98, -32.01) * mm});
            skLineSegment(sketch, "E398", {"start": v(-16.98, -32.01) * mm, "end": v(-16.89, -31.46) * mm});
            skLineSegment(sketch, "E399", {"start": v(-16.89, -31.46) * mm, "end": v(-16.83, -31.22) * mm});
            skArc(sketch, "E400", {"start": v(-16.83, -31.22) * mm, "mid": v(-17.11, -31.07) * mm, "end": v(-17.39, -30.92) * mm});
            skLineSegment(sketch, "E401", {"start": v(-17.39, -30.92) * mm, "end": v(-17.56, -31.1) * mm});
            skLineSegment(sketch, "E402", {"start": v(-17.56, -31.1) * mm, "end": v(-17.97, -31.47) * mm});
            skLineSegment(sketch, "E403", {"start": v(-17.97, -31.47) * mm, "end": v(-18.47, -31.87) * mm});
            skLineSegment(sketch, "E404", {"start": v(-18.47, -31.87) * mm, "end": v(-18.78, -32.1) * mm});
            skArc(sketch, "E405", {"start": v(-18.78, -32.1) * mm, "mid": v(-19.06, -31.94) * mm, "end": v(-19.33, -31.78) * mm});
            skLineSegment(sketch, "E406", {"start": v(-19.33, -31.78) * mm, "end": v(-19.27, -31.4) * mm});
            skLineSegment(sketch, "E407", {"start": v(-19.27, -31.4) * mm, "end": v(-19.15, -30.76) * mm});
            skLineSegment(sketch, "E408", {"start": v(-19.15, -30.76) * mm, "end": v(-19.02, -30.22) * mm});
            skLineSegment(sketch, "E409", {"start": v(-19.02, -30.22) * mm, "end": v(-18.94, -29.99) * mm});
            skArc(sketch, "E410", {"start": v(-18.94, -29.99) * mm, "mid": v(-19.21, -29.82) * mm, "end": v(-19.48, -29.64) * mm});
            skLineSegment(sketch, "E411", {"start": v(-19.48, -29.64) * mm, "end": v(-19.66, -29.8) * mm});
            skLineSegment(sketch, "E412", {"start": v(-19.66, -29.8) * mm, "end": v(-20.1, -30.15) * mm});
            skLineSegment(sketch, "E413", {"start": v(-20.1, -30.15) * mm, "end": v(-20.62, -30.52) * mm});
            skLineSegment(sketch, "E414", {"start": v(-20.62, -30.52) * mm, "end": v(-20.95, -30.73) * mm});
            skArc(sketch, "E415", {"start": v(-20.95, -30.73) * mm, "mid": v(-21.22, -30.55) * mm, "end": v(-21.48, -30.37) * mm});
            skLineSegment(sketch, "E416", {"start": v(-21.48, -30.37) * mm, "end": v(-21.4, -29.99) * mm});
            skLineSegment(sketch, "E417", {"start": v(-21.4, -29.99) * mm, "end": v(-21.23, -29.37) * mm});
            skLineSegment(sketch, "E418", {"start": v(-21.23, -29.37) * mm, "end": v(-21.06, -28.84) * mm});
            skLineSegment(sketch, "E419", {"start": v(-21.06, -28.84) * mm, "end": v(-20.97, -28.6) * mm});
            skArc(sketch, "E420", {"start": v(-20.97, -28.6) * mm, "mid": v(-21.22, -28.42) * mm, "end": v(-21.48, -28.23) * mm});
            skLineSegment(sketch, "E421", {"start": v(-21.48, -28.23) * mm, "end": v(-21.67, -28.38) * mm});
            skLineSegment(sketch, "E422", {"start": v(-21.67, -28.38) * mm, "end": v(-22.13, -28.7) * mm});
            skLineSegment(sketch, "E423", {"start": v(-22.13, -28.7) * mm, "end": v(-22.68, -29.03) * mm});
            skLineSegment(sketch, "E424", {"start": v(-22.68, -29.03) * mm, "end": v(-23.02, -29.22) * mm});
            skArc(sketch, "E425", {"start": v(-23.02, -29.22) * mm, "mid": v(-23.27, -29.02) * mm, "end": v(-23.52, -28.81) * mm});
            skLineSegment(sketch, "E426", {"start": v(-23.52, -28.81) * mm, "end": v(-23.41, -28.44) * mm});
            skLineSegment(sketch, "E427", {"start": v(-23.41, -28.44) * mm, "end": v(-23.2, -27.83) * mm});
            skLineSegment(sketch, "E428", {"start": v(-23.2, -27.83) * mm, "end": v(-23, -27.32) * mm});
            skLineSegment(sketch, "E429", {"start": v(-23, -27.32) * mm, "end": v(-22.9, -27.1) * mm});
            skArc(sketch, "E430", {"start": v(-22.9, -27.1) * mm, "mid": v(-23.13, -26.89) * mm, "end": v(-23.38, -26.68) * mm});
            skLineSegment(sketch, "E431", {"start": v(-23.38, -26.68) * mm, "end": v(-23.58, -26.81) * mm});
            skLineSegment(sketch, "E432", {"start": v(-23.58, -26.81) * mm, "end": v(-24.06, -27.1) * mm});
            skLineSegment(sketch, "E433", {"start": v(-24.06, -27.1) * mm, "end": v(-24.63, -27.4) * mm});
            skLineSegment(sketch, "E434", {"start": v(-24.63, -27.4) * mm, "end": v(-24.98, -27.56) * mm});
            skArc(sketch, "E435", {"start": v(-24.98, -27.56) * mm, "mid": v(-25.22, -27.34) * mm, "end": v(-25.45, -27.12) * mm});
            skLineSegment(sketch, "E436", {"start": v(-25.45, -27.12) * mm, "end": v(-25.32, -26.76) * mm});
            skLineSegment(sketch, "E437", {"start": v(-25.32, -26.76) * mm, "end": v(-25.07, -26.17) * mm});
            skLineSegment(sketch, "E438", {"start": v(-25.07, -26.17) * mm, "end": v(-24.82, -25.67) * mm});
            skLineSegment(sketch, "E439", {"start": v(-24.82, -25.67) * mm, "end": v(-24.7, -25.45) * mm});
            skArc(sketch, "E440", {"start": v(-24.7, -25.45) * mm, "mid": v(-24.93, -25.23) * mm, "end": v(-25.16, -25) * mm});
            skLineSegment(sketch, "E441", {"start": v(-25.16, -25) * mm, "end": v(-25.37, -25.12) * mm});
            skLineSegment(sketch, "E442", {"start": v(-25.37, -25.12) * mm, "end": v(-25.87, -25.37) * mm});
            skLineSegment(sketch, "E443", {"start": v(-25.87, -25.37) * mm, "end": v(-26.46, -25.63) * mm});
            skLineSegment(sketch, "E444", {"start": v(-26.46, -25.63) * mm, "end": v(-26.82, -25.77) * mm});
            skArc(sketch, "E445", {"start": v(-26.82, -25.77) * mm, "mid": v(-27.05, -25.54) * mm, "end": v(-27.26, -25.3) * mm});
            skLineSegment(sketch, "E446", {"start": v(-27.26, -25.3) * mm, "end": v(-27.1, -24.94) * mm});
            skLineSegment(sketch, "E447", {"start": v(-27.1, -24.94) * mm, "end": v(-26.81, -24.37) * mm});
            skLineSegment(sketch, "E448", {"start": v(-26.81, -24.37) * mm, "end": v(-26.54, -23.9) * mm});
            skLineSegment(sketch, "E449", {"start": v(-26.54, -23.9) * mm, "end": v(-26.4, -23.68) * mm});
            skArc(sketch, "E450", {"start": v(-26.4, -23.68) * mm, "mid": v(-26.62, -23.45) * mm, "end": v(-26.83, -23.2) * mm});
            skLineSegment(sketch, "E451", {"start": v(-26.83, -23.2) * mm, "end": v(-27.05, -23.31) * mm});
            skLineSegment(sketch, "E452", {"start": v(-27.05, -23.31) * mm, "end": v(-27.56, -23.53) * mm});
            skLineSegment(sketch, "E453", {"start": v(-27.56, -23.53) * mm, "end": v(-28.16, -23.74) * mm});
            skLineSegment(sketch, "E454", {"start": v(-28.16, -23.74) * mm, "end": v(-28.54, -23.86) * mm});
            skArc(sketch, "E455", {"start": v(-28.54, -23.86) * mm, "mid": v(-28.74, -23.6) * mm, "end": v(-28.94, -23.36) * mm});
            skLineSegment(sketch, "E456", {"start": v(-28.94, -23.36) * mm, "end": v(-28.76, -23.01) * mm});
            skLineSegment(sketch, "E457", {"start": v(-28.76, -23.01) * mm, "end": v(-28.43, -22.46) * mm});
            skLineSegment(sketch, "E458", {"start": v(-28.43, -22.46) * mm, "end": v(-28.12, -22) * mm});
            skLineSegment(sketch, "E459", {"start": v(-28.12, -22) * mm, "end": v(-27.98, -21.8) * mm});
            skArc(sketch, "E460", {"start": v(-27.98, -21.8) * mm, "mid": v(-28.17, -21.55) * mm, "end": v(-28.36, -21.3) * mm});
            skLineSegment(sketch, "E461", {"start": v(-28.36, -21.3) * mm, "end": v(-28.6, -21.39) * mm});
            skLineSegment(sketch, "E462", {"start": v(-28.6, -21.39) * mm, "end": v(-29.12, -21.57) * mm});
            skLineSegment(sketch, "E463", {"start": v(-29.12, -21.57) * mm, "end": v(-29.73, -21.74) * mm});
            skLineSegment(sketch, "E464", {"start": v(-29.73, -21.74) * mm, "end": v(-30.12, -21.83) * mm});
            skArc(sketch, "E465", {"start": v(-30.12, -21.83) * mm, "mid": v(-30.3, -21.57) * mm, "end": v(-30.49, -21.3) * mm});
            skLineSegment(sketch, "E466", {"start": v(-30.49, -21.3) * mm, "end": v(-30.28, -20.98) * mm});
            skLineSegment(sketch, "E467", {"start": v(-30.28, -20.98) * mm, "end": v(-29.91, -20.45) * mm});
            skLineSegment(sketch, "E468", {"start": v(-29.91, -20.45) * mm, "end": v(-29.57, -20) * mm});
            skLineSegment(sketch, "E469", {"start": v(-29.57, -20) * mm, "end": v(-29.41, -19.82) * mm});
            skArc(sketch, "E470", {"start": v(-29.41, -19.82) * mm, "mid": v(-29.59, -19.56) * mm, "end": v(-29.76, -19.3) * mm});
            skLineSegment(sketch, "E471", {"start": v(-29.76, -19.3) * mm, "end": v(-30, -19.37) * mm});
            skLineSegment(sketch, "E472", {"start": v(-30, -19.37) * mm, "end": v(-30.54, -19.5) * mm});
            skLineSegment(sketch, "E473", {"start": v(-30.54, -19.5) * mm, "end": v(-31.16, -19.64) * mm});
            skLineSegment(sketch, "E474", {"start": v(-31.16, -19.64) * mm, "end": v(-31.55, -19.7) * mm});
            skArc(sketch, "E475", {"start": v(-31.55, -19.7) * mm, "mid": v(-31.72, -19.43) * mm, "end": v(-31.88, -19.15) * mm});
            skLineSegment(sketch, "E476", {"start": v(-31.88, -19.15) * mm, "end": v(-31.65, -18.84) * mm});
            skLineSegment(sketch, "E477", {"start": v(-31.65, -18.84) * mm, "end": v(-31.25, -18.34) * mm});
            skLineSegment(sketch, "E478", {"start": v(-31.25, -18.34) * mm, "end": v(-30.88, -17.92) * mm});
            skLineSegment(sketch, "E479", {"start": v(-30.88, -17.92) * mm, "end": v(-30.71, -17.75) * mm});
            skArc(sketch, "E480", {"start": v(-30.71, -17.75) * mm, "mid": v(-30.87, -17.47) * mm, "end": v(-31.02, -17.2) * mm});
            skLineSegment(sketch, "E481", {"start": v(-31.02, -17.2) * mm, "end": v(-31.26, -17.25) * mm});
            skLineSegment(sketch, "E482", {"start": v(-31.26, -17.25) * mm, "end": v(-31.8, -17.35) * mm});
            skLineSegment(sketch, "E483", {"start": v(-31.8, -17.35) * mm, "end": v(-32.44, -17.44) * mm});
            skLineSegment(sketch, "E484", {"start": v(-32.44, -17.44) * mm, "end": v(-32.83, -17.48) * mm});
            skArc(sketch, "E485", {"start": v(-32.83, -17.48) * mm, "mid": v(-32.98, -17.2) * mm, "end": v(-33.13, -16.9) * mm});
            skLineSegment(sketch, "E486", {"start": v(-33.13, -16.9) * mm, "end": v(-32.88, -16.6) * mm});
            skLineSegment(sketch, "E487", {"start": v(-32.88, -16.6) * mm, "end": v(-32.44, -16.14) * mm});
            skLineSegment(sketch, "E488", {"start": v(-32.44, -16.14) * mm, "end": v(-32.05, -15.75) * mm});
            skLineSegment(sketch, "E489", {"start": v(-32.05, -15.75) * mm, "end": v(-31.86, -15.59) * mm});
            skArc(sketch, "E490", {"start": v(-31.86, -15.59) * mm, "mid": v(-32, -15.3) * mm, "end": v(-32.14, -15.01) * mm});
            skLineSegment(sketch, "E491", {"start": v(-32.14, -15.01) * mm, "end": v(-32.38, -15.05) * mm});
            skLineSegment(sketch, "E492", {"start": v(-32.38, -15.05) * mm, "end": v(-32.93, -15.12) * mm});
            skLineSegment(sketch, "E493", {"start": v(-32.93, -15.12) * mm, "end": v(-33.57, -15.16) * mm});
            skLineSegment(sketch, "E494", {"start": v(-33.57, -15.16) * mm, "end": v(-33.96, -15.17) * mm});
            skArc(sketch, "E495", {"start": v(-33.96, -15.17) * mm, "mid": v(-34.1, -14.87) * mm, "end": v(-34.22, -14.58) * mm});
            skLineSegment(sketch, "E496", {"start": v(-34.22, -14.58) * mm, "end": v(-33.95, -14.3) * mm});
            skLineSegment(sketch, "E497", {"start": v(-33.95, -14.3) * mm, "end": v(-33.48, -13.86) * mm});
            skLineSegment(sketch, "E498", {"start": v(-33.48, -13.86) * mm, "end": v(-33.06, -13.5) * mm});
            skLineSegment(sketch, "E499", {"start": v(-33.06, -13.5) * mm, "end": v(-32.86, -13.35) * mm});
            skArc(sketch, "E500", {"start": v(-32.86, -13.35) * mm, "mid": v(-32.98, -13.05) * mm, "end": v(-33.1, -12.76) * mm});
            skLineSegment(sketch, "E501", {"start": v(-33.1, -12.76) * mm, "end": v(-33.34, -12.78) * mm});
            skLineSegment(sketch, "E502", {"start": v(-33.34, -12.78) * mm, "end": v(-33.9, -12.8) * mm});
            skLineSegment(sketch, "E503", {"start": v(-33.9, -12.8) * mm, "end": v(-34.54, -12.8) * mm});
            skLineSegment(sketch, "E504", {"start": v(-34.54, -12.8) * mm, "end": v(-34.93, -12.79) * mm});
            skArc(sketch, "E505", {"start": v(-34.93, -12.79) * mm, "mid": v(-35.04, -12.49) * mm, "end": v(-35.14, -12.19) * mm});
            skLineSegment(sketch, "E506", {"start": v(-35.14, -12.19) * mm, "end": v(-34.85, -11.92) * mm});
            skLineSegment(sketch, "E507", {"start": v(-34.85, -11.92) * mm, "end": v(-34.36, -11.52) * mm});
            skLineSegment(sketch, "E508", {"start": v(-34.36, -11.52) * mm, "end": v(-33.9, -11.19) * mm});
            skLineSegment(sketch, "E509", {"start": v(-33.9, -11.19) * mm, "end": v(-33.7, -11.05) * mm});
            skArc(sketch, "E510", {"start": v(-33.7, -11.05) * mm, "mid": v(-33.8, -10.75) * mm, "end": v(-33.9, -10.44) * mm});
            skLineSegment(sketch, "E511", {"start": v(-33.9, -10.44) * mm, "end": v(-34.14, -10.45) * mm});
            skLineSegment(sketch, "E512", {"start": v(-34.14, -10.45) * mm, "end": v(-34.7, -10.44) * mm});
            skLineSegment(sketch, "E513", {"start": v(-34.7, -10.44) * mm, "end": v(-35.34, -10.4) * mm});
            skLineSegment(sketch, "E514", {"start": v(-35.34, -10.4) * mm, "end": v(-35.73, -10.35) * mm});
            skArc(sketch, "E515", {"start": v(-35.73, -10.35) * mm, "mid": v(-35.81, -10.04) * mm, "end": v(-35.9, -9.73) * mm});
            skLineSegment(sketch, "E516", {"start": v(-35.9, -9.73) * mm, "end": v(-35.6, -9.49) * mm});
            skLineSegment(sketch, "E517", {"start": v(-35.6, -9.49) * mm, "end": v(-35.07, -9.12) * mm});
            skLineSegment(sketch, "E518", {"start": v(-35.07, -9.12) * mm, "end": v(-34.6, -8.82) * mm});
            skLineSegment(sketch, "E519", {"start": v(-34.6, -8.82) * mm, "end": v(-34.39, -8.7) * mm});
            skArc(sketch, "E520", {"start": v(-34.39, -8.7) * mm, "mid": v(-34.46, -8.39) * mm, "end": v(-34.54, -8.08) * mm});
            skLineSegment(sketch, "E521", {"start": v(-34.54, -8.08) * mm, "end": v(-34.78, -8.07) * mm});
            skLineSegment(sketch, "E522", {"start": v(-34.78, -8.07) * mm, "end": v(-35.34, -8.02) * mm});
            skLineSegment(sketch, "E523", {"start": v(-35.34, -8.02) * mm, "end": v(-35.97, -7.93) * mm});
            skLineSegment(sketch, "E524", {"start": v(-35.97, -7.93) * mm, "end": v(-36.36, -7.86) * mm});
            skArc(sketch, "E525", {"start": v(-36.36, -7.86) * mm, "mid": v(-36.42, -7.54) * mm, "end": v(-36.49, -7.23) * mm});
            skLineSegment(sketch, "E526", {"start": v(-36.49, -7.23) * mm, "end": v(-36.16, -7.01) * mm});
            skLineSegment(sketch, "E527", {"start": v(-36.16, -7.01) * mm, "end": v(-35.61, -6.68) * mm});
            skLineSegment(sketch, "E528", {"start": v(-35.61, -6.68) * mm, "end": v(-35.13, -6.41) * mm});
            skLineSegment(sketch, "E529", {"start": v(-35.13, -6.41) * mm, "end": v(-34.9, -6.3) * mm});
            skArc(sketch, "E530", {"start": v(-34.9, -6.3) * mm, "mid": v(-34.96, -6) * mm, "end": v(-35.01, -5.68) * mm});
            skLineSegment(sketch, "E531", {"start": v(-35.01, -5.68) * mm, "end": v(-35.26, -5.65) * mm});
            skLineSegment(sketch, "E532", {"start": v(-35.26, -5.65) * mm, "end": v(-35.8, -5.56) * mm});
            skLineSegment(sketch, "E533", {"start": v(-35.8, -5.56) * mm, "end": v(-36.43, -5.43) * mm});
            skLineSegment(sketch, "E534", {"start": v(-36.43, -5.43) * mm, "end": v(-36.81, -5.33) * mm});
            skArc(sketch, "E535", {"start": v(-36.81, -5.33) * mm, "mid": v(-36.86, -5.01) * mm, "end": v(-36.9, -4.7) * mm});
            skLineSegment(sketch, "E536", {"start": v(-36.9, -4.7) * mm, "end": v(-36.56, -4.5) * mm});
            skLineSegment(sketch, "E537", {"start": v(-36.56, -4.5) * mm, "end": v(-35.99, -4.2) * mm});
            skLineSegment(sketch, "E538", {"start": v(-35.99, -4.2) * mm, "end": v(-35.48, -3.97) * mm});
            skLineSegment(sketch, "E539", {"start": v(-35.48, -3.97) * mm, "end": v(-35.26, -3.88) * mm});
            skArc(sketch, "E540", {"start": v(-35.26, -3.88) * mm, "mid": v(-35.29, -3.56) * mm, "end": v(-35.32, -3.25) * mm});
            skLineSegment(sketch, "E541", {"start": v(-35.32, -3.25) * mm, "end": v(-35.56, -3.2) * mm});
            skLineSegment(sketch, "E542", {"start": v(-35.56, -3.2) * mm, "end": v(-36.1, -3.08) * mm});
            skLineSegment(sketch, "E543", {"start": v(-36.1, -3.08) * mm, "end": v(-36.72, -2.9) * mm});
            skLineSegment(sketch, "E544", {"start": v(-36.72, -2.9) * mm, "end": v(-37.1, -2.78) * mm});
            skArc(sketch, "E545", {"start": v(-37.1, -2.78) * mm, "mid": v(-37.11, -2.46) * mm, "end": v(-37.13, -2.14) * mm});
            skLineSegment(sketch, "E546", {"start": v(-37.13, -2.14) * mm, "end": v(-36.78, -1.97) * mm});
            skLineSegment(sketch, "E547", {"start": v(-36.78, -1.97) * mm, "end": v(-36.2, -1.71) * mm});
            skLineSegment(sketch, "E548", {"start": v(-36.2, -1.71) * mm, "end": v(-35.67, -1.51) * mm});
            skLineSegment(sketch, "E549", {"start": v(-35.67, -1.51) * mm, "end": v(-35.44, -1.44) * mm});
            skArc(sketch, "E550", {"start": v(-35.44, -1.44) * mm, "mid": v(-35.45, -1.12) * mm, "end": v(-35.46, -0.8) * mm});
            skLineSegment(sketch, "E551", {"start": v(-35.46, -0.8) * mm, "end": v(-35.7, -0.74) * mm});
            skLineSegment(sketch, "E552", {"start": v(-35.7, -0.74) * mm, "end": v(-36.23, -0.58) * mm});
            skLineSegment(sketch, "E553", {"start": v(-36.23, -0.58) * mm, "end": v(-36.83, -0.36) * mm});
            skLineSegment(sketch, "E554", {"start": v(-36.83, -0.36) * mm, "end": v(-37.2, -0.21) * mm});
            skArc(sketch, "E555", {"start": v(-37.2, -0.21) * mm, "mid": v(-37.2, 0.1) * mm, "end": v(-37.2, 0.43) * mm});
            skLineSegment(sketch, "E556", {"start": v(-37.2, 0.43) * mm, "end": v(-36.83, 0.58) * mm});
            skLineSegment(sketch, "E557", {"start": v(-36.83, 0.58) * mm, "end": v(-36.23, 0.8) * mm});
            skLineSegment(sketch, "E558", {"start": v(-36.23, 0.8) * mm, "end": v(-35.7, 0.95) * mm});
            skLineSegment(sketch, "E559", {"start": v(-35.7, 0.95) * mm, "end": v(-35.46, 1) * mm});
            skArc(sketch, "E560", {"start": v(-35.46, 1) * mm, "mid": v(-35.44, 1.33) * mm, "end": v(-35.43, 1.65) * mm});
            skLineSegment(sketch, "E561", {"start": v(-35.43, 1.65) * mm, "end": v(-35.66, 1.72) * mm});
            skLineSegment(sketch, "E562", {"start": v(-35.66, 1.72) * mm, "end": v(-36.18, 1.92) * mm});
            skLineSegment(sketch, "E563", {"start": v(-36.18, 1.92) * mm, "end": v(-36.77, 2.18) * mm});
            skLineSegment(sketch, "E564", {"start": v(-36.77, 2.18) * mm, "end": v(-37.12, 2.35) * mm});
            skArc(sketch, "E565", {"start": v(-37.12, 2.35) * mm, "mid": v(-37.1, 2.67) * mm, "end": v(-37.07, 3) * mm});
            skLineSegment(sketch, "E566", {"start": v(-37.07, 3) * mm, "end": v(-36.7, 3.12) * mm});
            skLineSegment(sketch, "E567", {"start": v(-36.7, 3.12) * mm, "end": v(-36.08, 3.29) * mm});
            skLineSegment(sketch, "E568", {"start": v(-36.08, 3.29) * mm, "end": v(-35.54, 3.41) * mm});
            skLineSegment(sketch, "E569", {"start": v(-35.54, 3.41) * mm, "end": v(-35.3, 3.45) * mm});
            skArc(sketch, "E570", {"start": v(-35.3, 3.45) * mm, "mid": v(-35.27, 3.77) * mm, "end": v(-35.23, 4.09) * mm});
            skLineSegment(sketch, "E571", {"start": v(-35.23, 4.09) * mm, "end": v(-35.46, 4.18) * mm});
            skLineSegment(sketch, "E572", {"start": v(-35.46, 4.18) * mm, "end": v(-35.96, 4.41) * mm});
            skLineSegment(sketch, "E573", {"start": v(-35.96, 4.41) * mm, "end": v(-36.53, 4.71) * mm});
            skLineSegment(sketch, "E574", {"start": v(-36.53, 4.71) * mm, "end": v(-36.87, 4.91) * mm});
            skArc(sketch, "E575", {"start": v(-36.87, 4.91) * mm, "mid": v(-36.83, 5.23) * mm, "end": v(-36.78, 5.54) * mm});
            skLineSegment(sketch, "E576", {"start": v(-36.78, 5.54) * mm, "end": v(-36.4, 5.64) * mm});
            skLineSegment(sketch, "E577", {"start": v(-36.4, 5.64) * mm, "end": v(-35.77, 5.77) * mm});
            skLineSegment(sketch, "E578", {"start": v(-35.77, 5.77) * mm, "end": v(-35.22, 5.86) * mm});
            skLineSegment(sketch, "E579", {"start": v(-35.22, 5.86) * mm, "end": v(-34.98, 5.88) * mm});
            skArc(sketch, "E580", {"start": v(-34.98, 5.88) * mm, "mid": v(-34.92, 6.2) * mm, "end": v(-34.87, 6.5) * mm});
            skLineSegment(sketch, "E581", {"start": v(-34.87, 6.5) * mm, "end": v(-35.09, 6.62) * mm});
            skLineSegment(sketch, "E582", {"start": v(-35.09, 6.62) * mm, "end": v(-35.57, 6.88) * mm});
            skLineSegment(sketch, "E583", {"start": v(-35.57, 6.88) * mm, "end": v(-36.12, 7.22) * mm});
            skLineSegment(sketch, "E584", {"start": v(-36.12, 7.22) * mm, "end": v(-36.44, 7.44) * mm});
            skArc(sketch, "E585", {"start": v(-36.44, 7.44) * mm, "mid": v(-36.38, 7.76) * mm, "end": v(-36.3, 8.07) * mm});
            skLineSegment(sketch, "E586", {"start": v(-36.3, 8.07) * mm, "end": v(-35.92, 8.14) * mm});
            skLineSegment(sketch, "E587", {"start": v(-35.92, 8.14) * mm, "end": v(-35.29, 8.23) * mm});
            skLineSegment(sketch, "E588", {"start": v(-35.29, 8.23) * mm, "end": v(-34.73, 8.27) * mm});
            skLineSegment(sketch, "E589", {"start": v(-34.73, 8.27) * mm, "end": v(-34.49, 8.28) * mm});
            skArc(sketch, "E590", {"start": v(-34.49, 8.28) * mm, "mid": v(-34.41, 8.59) * mm, "end": v(-34.34, 8.9) * mm});
            skLineSegment(sketch, "E591", {"start": v(-34.34, 8.9) * mm, "end": v(-34.55, 9.02) * mm});
            skLineSegment(sketch, "E592", {"start": v(-34.55, 9.02) * mm, "end": v(-35.02, 9.32) * mm});
            skLineSegment(sketch, "E593", {"start": v(-35.02, 9.32) * mm, "end": v(-35.54, 9.7) * mm});
            skLineSegment(sketch, "E594", {"start": v(-35.54, 9.7) * mm, "end": v(-35.84, 9.94) * mm});
            skArc(sketch, "E595", {"start": v(-35.84, 9.94) * mm, "mid": v(-35.76, 10.25) * mm, "end": v(-35.67, 10.56) * mm});
            skLineSegment(sketch, "E596", {"start": v(-35.67, 10.56) * mm, "end": v(-35.28, 10.6) * mm});
            skLineSegment(sketch, "E597", {"start": v(-35.28, 10.6) * mm, "end": v(-34.64, 10.64) * mm});
            skLineSegment(sketch, "E598", {"start": v(-34.64, 10.64) * mm, "end": v(-34.08, 10.65) * mm});
            skLineSegment(sketch, "E599", {"start": v(-34.08, 10.65) * mm, "end": v(-33.84, 10.64) * mm});
            skArc(sketch, "E600", {"start": v(-33.84, 10.64) * mm, "mid": v(-33.74, 10.94) * mm, "end": v(-33.64, 11.25) * mm});
            skLineSegment(sketch, "E601", {"start": v(-33.64, 11.25) * mm, "end": v(-33.84, 11.38) * mm});
            skLineSegment(sketch, "E602", {"start": v(-33.84, 11.38) * mm, "end": v(-34.29, 11.72) * mm});
            skLineSegment(sketch, "E603", {"start": v(-34.29, 11.72) * mm, "end": v(-34.78, 12.12) * mm});
            skLineSegment(sketch, "E604", {"start": v(-34.78, 12.12) * mm, "end": v(-35.07, 12.39) * mm});
            skArc(sketch, "E605", {"start": v(-35.07, 12.39) * mm, "mid": v(-34.96, 12.7) * mm, "end": v(-34.85, 13) * mm});
            skLineSegment(sketch, "E606", {"start": v(-34.85, 13) * mm, "end": v(-34.46, 13) * mm});
            skLineSegment(sketch, "E607", {"start": v(-34.46, 13) * mm, "end": v(-33.82, 13) * mm});
            skLineSegment(sketch, "E608", {"start": v(-33.82, 13) * mm, "end": v(-33.27, 12.98) * mm});
            skLineSegment(sketch, "E609", {"start": v(-33.27, 12.98) * mm, "end": v(-33.02, 12.95) * mm});
            skArc(sketch, "E610", {"start": v(-33.02, 12.95) * mm, "mid": v(-32.9, 13.25) * mm, "end": v(-32.78, 13.54) * mm});
            skLineSegment(sketch, "E611", {"start": v(-32.78, 13.54) * mm, "end": v(-32.98, 13.7) * mm});
            skLineSegment(sketch, "E612", {"start": v(-32.98, 13.7) * mm, "end": v(-33.4, 14.05) * mm});
            skLineSegment(sketch, "E613", {"start": v(-33.4, 14.05) * mm, "end": v(-33.86, 14.5) * mm});
            skLineSegment(sketch, "E614", {"start": v(-33.86, 14.5) * mm, "end": v(-34.13, 14.78) * mm});
            skArc(sketch, "E615", {"start": v(-34.13, 14.78) * mm, "mid": v(-34, 15.07) * mm, "end": v(-33.87, 15.37) * mm});
            skLineSegment(sketch, "E616", {"start": v(-33.87, 15.37) * mm, "end": v(-33.48, 15.36) * mm});
            skLineSegment(sketch, "E617", {"start": v(-33.48, 15.36) * mm, "end": v(-32.84, 15.3) * mm});
            skLineSegment(sketch, "E618", {"start": v(-32.84, 15.3) * mm, "end": v(-32.3, 15.24) * mm});
            skLineSegment(sketch, "E619", {"start": v(-32.3, 15.24) * mm, "end": v(-32.05, 15.2) * mm});
            skArc(sketch, "E620", {"start": v(-32.05, 15.2) * mm, "mid": v(-31.91, 15.48) * mm, "end": v(-31.77, 15.77) * mm});
            skLineSegment(sketch, "E621", {"start": v(-31.77, 15.77) * mm, "end": v(-31.95, 15.93) * mm});
            skLineSegment(sketch, "E622", {"start": v(-31.95, 15.93) * mm, "end": v(-32.35, 16.32) * mm});
            skLineSegment(sketch, "E623", {"start": v(-32.35, 16.32) * mm, "end": v(-32.78, 16.8) * mm});
            skLineSegment(sketch, "E624", {"start": v(-32.78, 16.8) * mm, "end": v(-33.03, 17.1) * mm});
            skArc(sketch, "E625", {"start": v(-33.03, 17.1) * mm, "mid": v(-32.88, 17.38) * mm, "end": v(-32.73, 17.67) * mm});
            skLineSegment(sketch, "E626", {"start": v(-32.73, 17.67) * mm, "end": v(-32.34, 17.63) * mm});
            skLineSegment(sketch, "E627", {"start": v(-32.34, 17.63) * mm, "end": v(-31.7, 17.54) * mm});
            skLineSegment(sketch, "E628", {"start": v(-31.7, 17.54) * mm, "end": v(-31.16, 17.43) * mm});
            skLineSegment(sketch, "E629", {"start": v(-31.16, 17.43) * mm, "end": v(-30.92, 17.37) * mm});
            skArc(sketch, "E630", {"start": v(-30.92, 17.37) * mm, "mid": v(-30.77, 17.65) * mm, "end": v(-30.6, 17.93) * mm});
            skLineSegment(sketch, "E631", {"start": v(-30.6, 17.93) * mm, "end": v(-30.78, 18.1) * mm});
            skLineSegment(sketch, "E632", {"start": v(-30.78, 18.1) * mm, "end": v(-31.15, 18.52) * mm});
            skLineSegment(sketch, "E633", {"start": v(-31.15, 18.52) * mm, "end": v(-31.55, 19.02) * mm});
            skLineSegment(sketch, "E634", {"start": v(-31.55, 19.02) * mm, "end": v(-31.77, 19.34) * mm});
            skArc(sketch, "E635", {"start": v(-31.77, 19.34) * mm, "mid": v(-31.6, 19.61) * mm, "end": v(-31.44, 19.88) * mm});
            skLineSegment(sketch, "E636", {"start": v(-31.44, 19.88) * mm, "end": v(-31.05, 19.82) * mm});
            skLineSegment(sketch, "E637", {"start": v(-31.05, 19.82) * mm, "end": v(-30.42, 19.68) * mm});
            skLineSegment(sketch, "E638", {"start": v(-30.42, 19.68) * mm, "end": v(-29.89, 19.54) * mm});
            skLineSegment(sketch, "E639", {"start": v(-29.89, 19.54) * mm, "end": v(-29.65, 19.47) * mm});
            skArc(sketch, "E640", {"start": v(-29.65, 19.47) * mm, "mid": v(-29.48, 19.73) * mm, "end": v(-29.3, 20) * mm});
            skLineSegment(sketch, "E641", {"start": v(-29.3, 20) * mm, "end": v(-29.46, 20.18) * mm});
            skLineSegment(sketch, "E642", {"start": v(-29.46, 20.18) * mm, "end": v(-29.8, 20.62) * mm});
            skLineSegment(sketch, "E643", {"start": v(-29.8, 20.62) * mm, "end": v(-30.16, 21.15) * mm});
            skLineSegment(sketch, "E644", {"start": v(-30.16, 21.15) * mm, "end": v(-30.36, 21.48) * mm});
            skArc(sketch, "E645", {"start": v(-30.36, 21.48) * mm, "mid": v(-30.18, 21.75) * mm, "end": v(-29.99, 22) * mm});
            skLineSegment(sketch, "E646", {"start": v(-29.99, 22) * mm, "end": v(-29.6, 21.91) * mm});
            skLineSegment(sketch, "E647", {"start": v(-29.6, 21.91) * mm, "end": v(-29, 21.74) * mm});
            skLineSegment(sketch, "E648", {"start": v(-29, 21.74) * mm, "end": v(-28.47, 21.56) * mm});
            skLineSegment(sketch, "E649", {"start": v(-28.47, 21.56) * mm, "end": v(-28.24, 21.46) * mm});
            skArc(sketch, "E650", {"start": v(-28.24, 21.46) * mm, "mid": v(-28.05, 21.72) * mm, "end": v(-27.85, 21.97) * mm});
            skLineSegment(sketch, "E651", {"start": v(-27.85, 21.97) * mm, "end": v(-28, 22.17) * mm});
            skLineSegment(sketch, "E652", {"start": v(-28, 22.17) * mm, "end": v(-28.3, 22.63) * mm});
            skLineSegment(sketch, "E653", {"start": v(-28.3, 22.63) * mm, "end": v(-28.63, 23.18) * mm});
            skLineSegment(sketch, "E654", {"start": v(-28.63, 23.18) * mm, "end": v(-28.8, 23.53) * mm});
            skArc(sketch, "E655", {"start": v(-28.8, 23.53) * mm, "mid": v(-28.6, 23.78) * mm, "end": v(-28.4, 24.02) * mm});
            skLineSegment(sketch, "E656", {"start": v(-28.4, 24.02) * mm, "end": v(-28.03, 23.9) * mm});
            skLineSegment(sketch, "E657", {"start": v(-28.03, 23.9) * mm, "end": v(-27.42, 23.69) * mm});
            skLineSegment(sketch, "E658", {"start": v(-27.42, 23.69) * mm, "end": v(-26.91, 23.47) * mm});
            skLineSegment(sketch, "E659", {"start": v(-26.91, 23.47) * mm, "end": v(-26.7, 23.36) * mm});
            skArc(sketch, "E660", {"start": v(-26.7, 23.36) * mm, "mid": v(-26.48, 23.6) * mm, "end": v(-26.27, 23.84) * mm});
            skLineSegment(sketch, "E661", {"start": v(-26.27, 23.84) * mm, "end": v(-26.4, 24.05) * mm});
            skLineSegment(sketch, "E662", {"start": v(-26.4, 24.05) * mm, "end": v(-26.67, 24.53) * mm});
            skLineSegment(sketch, "E663", {"start": v(-26.67, 24.53) * mm, "end": v(-26.96, 25.1) * mm});
            skLineSegment(sketch, "E664", {"start": v(-26.96, 25.1) * mm, "end": v(-27.12, 25.46) * mm});
            skArc(sketch, "E665", {"start": v(-27.12, 25.46) * mm, "mid": v(-26.9, 25.7) * mm, "end": v(-26.68, 25.92) * mm});
            skLineSegment(sketch, "E666", {"start": v(-26.68, 25.92) * mm, "end": v(-26.31, 25.78) * mm});
            skLineSegment(sketch, "E667", {"start": v(-26.31, 25.78) * mm, "end": v(-25.72, 25.52) * mm});
            skLineSegment(sketch, "E668", {"start": v(-25.72, 25.52) * mm, "end": v(-25.23, 25.27) * mm});
            skLineSegment(sketch, "E669", {"start": v(-25.23, 25.27) * mm, "end": v(-25.02, 25.15) * mm});
            skArc(sketch, "E670", {"start": v(-25.02, 25.15) * mm, "mid": v(-24.79, 25.37) * mm, "end": v(-24.56, 25.6) * mm});
            skLineSegment(sketch, "E671", {"start": v(-24.56, 25.6) * mm, "end": v(-24.68, 25.8) * mm});
            skLineSegment(sketch, "E672", {"start": v(-24.68, 25.8) * mm, "end": v(-24.92, 26.31) * mm});
            skLineSegment(sketch, "E673", {"start": v(-24.92, 26.31) * mm, "end": v(-25.16, 26.9) * mm});
            skLineSegment(sketch, "E674", {"start": v(-25.16, 26.9) * mm, "end": v(-25.3, 27.27) * mm});
            skArc(sketch, "E675", {"start": v(-25.3, 27.27) * mm, "mid": v(-25.06, 27.49) * mm, "end": v(-24.82, 27.7) * mm});
            skLineSegment(sketch, "E676", {"start": v(-24.82, 27.7) * mm, "end": v(-24.47, 27.54) * mm});
            skLineSegment(sketch, "E677", {"start": v(-24.47, 27.54) * mm, "end": v(-23.9, 27.24) * mm});
            skLineSegment(sketch, "E678", {"start": v(-23.9, 27.24) * mm, "end": v(-23.43, 26.95) * mm});
            skLineSegment(sketch, "E679", {"start": v(-23.43, 26.95) * mm, "end": v(-23.22, 26.81) * mm});
            skArc(sketch, "E680", {"start": v(-23.22, 26.81) * mm, "mid": v(-22.98, 27.02) * mm, "end": v(-22.74, 27.23) * mm});
            skLineSegment(sketch, "E681", {"start": v(-22.74, 27.23) * mm, "end": v(-22.84, 27.45) * mm});
            skLineSegment(sketch, "E682", {"start": v(-22.84, 27.45) * mm, "end": v(-23.04, 27.97) * mm});
            skLineSegment(sketch, "E683", {"start": v(-23.04, 27.97) * mm, "end": v(-23.25, 28.57) * mm});
            skLineSegment(sketch, "E684", {"start": v(-23.25, 28.57) * mm, "end": v(-23.35, 28.95) * mm});
            skArc(sketch, "E685", {"start": v(-23.35, 28.95) * mm, "mid": v(-23.1, 29.15) * mm, "end": v(-22.85, 29.35) * mm});
            skLineSegment(sketch, "E686", {"start": v(-22.85, 29.35) * mm, "end": v(-22.51, 29.16) * mm});
            skLineSegment(sketch, "E687", {"start": v(-22.51, 29.16) * mm, "end": v(-21.97, 28.82) * mm});
            skLineSegment(sketch, "E688", {"start": v(-21.97, 28.82) * mm, "end": v(-21.51, 28.5) * mm});
            skLineSegment(sketch, "E689", {"start": v(-21.51, 28.5) * mm, "end": v(-21.32, 28.35) * mm});
            skArc(sketch, "E690", {"start": v(-21.32, 28.35) * mm, "mid": v(-21.06, 28.54) * mm, "end": v(-20.8, 28.73) * mm});
            skLineSegment(sketch, "E691", {"start": v(-20.8, 28.73) * mm, "end": v(-20.89, 28.96) * mm});
            skLineSegment(sketch, "E692", {"start": v(-20.89, 28.96) * mm, "end": v(-21.06, 29.5) * mm});
            skLineSegment(sketch, "E693", {"start": v(-21.06, 29.5) * mm, "end": v(-21.22, 30.11) * mm});
            skLineSegment(sketch, "E694", {"start": v(-21.22, 30.11) * mm, "end": v(-21.3, 30.5) * mm});
            skArc(sketch, "E695", {"start": v(-21.3, 30.5) * mm, "mid": v(-21.04, 30.68) * mm, "end": v(-20.77, 30.86) * mm});
            skLineSegment(sketch, "E696", {"start": v(-20.77, 30.86) * mm, "end": v(-20.45, 30.64) * mm});
            skLineSegment(sketch, "E697", {"start": v(-20.45, 30.64) * mm, "end": v(-19.93, 30.27) * mm});
            skLineSegment(sketch, "E698", {"start": v(-19.93, 30.27) * mm, "end": v(-19.5, 29.92) * mm});
            skLineSegment(sketch, "E699", {"start": v(-19.5, 29.92) * mm, "end": v(-19.3, 29.76) * mm});
            skArc(sketch, "E700", {"start": v(-19.3, 29.76) * mm, "mid": v(-19.04, 29.93) * mm, "end": v(-18.77, 30.1) * mm});
            skLineSegment(sketch, "E701", {"start": v(-18.77, 30.1) * mm, "end": v(-18.84, 30.33) * mm});
            skLineSegment(sketch, "E702", {"start": v(-18.84, 30.33) * mm, "end": v(-18.97, 30.87) * mm});
            skLineSegment(sketch, "E703", {"start": v(-18.97, 30.87) * mm, "end": v(-19.1, 31.5) * mm});
            skLineSegment(sketch, "E704", {"start": v(-19.1, 31.5) * mm, "end": v(-19.15, 31.9) * mm});
            skArc(sketch, "E705", {"start": v(-19.15, 31.9) * mm, "mid": v(-18.87, 32.06) * mm, "end": v(-18.6, 32.22) * mm});
            skLineSegment(sketch, "E706", {"start": v(-18.6, 32.22) * mm, "end": v(-18.28, 31.98) * mm});
            skLineSegment(sketch, "E707", {"start": v(-18.28, 31.98) * mm, "end": v(-17.8, 31.57) * mm});
            skLineSegment(sketch, "E708", {"start": v(-17.8, 31.57) * mm, "end": v(-17.38, 31.2) * mm});
            skLineSegment(sketch, "E709", {"start": v(-17.38, 31.2) * mm, "end": v(-17.21, 31.02) * mm});
            skArc(sketch, "E710", {"start": v(-17.21, 31.02) * mm, "mid": v(-16.93, 31.17) * mm, "end": v(-16.65, 31.32) * mm});
            skLineSegment(sketch, "E711", {"start": v(-16.65, 31.32) * mm, "end": v(-16.7, 31.56) * mm});
            skLineSegment(sketch, "E712", {"start": v(-16.7, 31.56) * mm, "end": v(-16.8, 32.1) * mm});
            skLineSegment(sketch, "E713", {"start": v(-16.8, 32.1) * mm, "end": v(-16.87, 32.75) * mm});
            skLineSegment(sketch, "E714", {"start": v(-16.87, 32.75) * mm, "end": v(-16.9, 33.14) * mm});
            skArc(sketch, "E715", {"start": v(-16.9, 33.14) * mm, "mid": v(-16.62, 33.28) * mm, "end": v(-16.33, 33.42) * mm});
            skLineSegment(sketch, "E716", {"start": v(-16.33, 33.42) * mm, "end": v(-16.03, 33.17) * mm});
            skLineSegment(sketch, "E717", {"start": v(-16.03, 33.17) * mm, "end": v(-15.57, 32.72) * mm});
            skLineSegment(sketch, "E718", {"start": v(-15.57, 32.72) * mm, "end": v(-15.19, 32.32) * mm});
            skLineSegment(sketch, "E719", {"start": v(-15.19, 32.32) * mm, "end": v(-15.03, 32.13) * mm});
            skArc(sketch, "E720", {"start": v(-15.03, 32.13) * mm, "mid": v(-14.74, 32.27) * mm, "end": v(-14.45, 32.4) * mm});
            skLineSegment(sketch, "E721", {"start": v(-14.45, 32.4) * mm, "end": v(-14.49, 32.64) * mm});
            skLineSegment(sketch, "E722", {"start": v(-14.49, 32.64) * mm, "end": v(-14.54, 33.2) * mm});
            skLineSegment(sketch, "E723", {"start": v(-14.54, 33.2) * mm, "end": v(-14.57, 33.83) * mm});
            skLineSegment(sketch, "E724", {"start": v(-14.57, 33.83) * mm, "end": v(-14.58, 34.22) * mm});
            skArc(sketch, "E725", {"start": v(-14.58, 34.22) * mm, "mid": v(-14.28, 34.35) * mm, "end": v(-13.98, 34.47) * mm});
            skLineSegment(sketch, "E726", {"start": v(-13.98, 34.47) * mm, "end": v(-13.7, 34.2) * mm});
            skLineSegment(sketch, "E727", {"start": v(-13.7, 34.2) * mm, "end": v(-13.28, 33.72) * mm});
            skLineSegment(sketch, "E728", {"start": v(-13.28, 33.72) * mm, "end": v(-12.92, 33.29) * mm});
            skLineSegment(sketch, "E729", {"start": v(-12.92, 33.29) * mm, "end": v(-12.78, 33.1) * mm});
            skArc(sketch, "E730", {"start": v(-12.78, 33.1) * mm, "mid": v(-12.48, 33.2) * mm, "end": v(-12.18, 33.32) * mm});
            skLineSegment(sketch, "E731", {"start": v(-12.18, 33.32) * mm, "end": v(-12.2, 33.56) * mm});
            skLineSegment(sketch, "E732", {"start": v(-12.2, 33.56) * mm, "end": v(-12.22, 34.12) * mm});
            skLineSegment(sketch, "E733", {"start": v(-12.22, 34.12) * mm, "end": v(-12.2, 34.76) * mm});
            skLineSegment(sketch, "E734", {"start": v(-12.2, 34.76) * mm, "end": v(-12.18, 35.15) * mm});
            skArc(sketch, "E735", {"start": v(-12.18, 35.15) * mm, "mid": v(-11.88, 35.25) * mm, "end": v(-11.57, 35.35) * mm});
            skLineSegment(sketch, "E736", {"start": v(-11.57, 35.35) * mm, "end": v(-11.31, 35.06) * mm});
            skLineSegment(sketch, "E737", {"start": v(-11.31, 35.06) * mm, "end": v(-10.92, 34.56) * mm});
            skLineSegment(sketch, "E738", {"start": v(-10.92, 34.56) * mm, "end": v(-10.6, 34.1) * mm});
            skLineSegment(sketch, "E739", {"start": v(-10.6, 34.1) * mm, "end": v(-10.46, 33.9) * mm});
            skArc(sketch, "E740", {"start": v(-10.46, 33.9) * mm, "mid": v(-10.16, 33.99) * mm, "end": v(-9.85, 34.08) * mm});
            skLineSegment(sketch, "E741", {"start": v(-9.85, 34.08) * mm, "end": v(-9.86, 34.32) * mm});
            skLineSegment(sketch, "E742", {"start": v(-9.86, 34.32) * mm, "end": v(-9.83, 34.88) * mm});
            skLineSegment(sketch, "E743", {"start": v(-9.83, 34.88) * mm, "end": v(-9.78, 35.52) * mm});
            skLineSegment(sketch, "E744", {"start": v(-9.78, 35.52) * mm, "end": v(-9.73, 35.9) * mm});
            skArc(sketch, "E745", {"start": v(-9.73, 35.9) * mm, "mid": v(-9.42, 35.99) * mm, "end": v(-9.1, 36.07) * mm});
            skLineSegment(sketch, "E746", {"start": v(-9.1, 36.07) * mm, "end": v(-8.87, 35.76) * mm});
            skLineSegment(sketch, "E747", {"start": v(-8.87, 35.76) * mm, "end": v(-8.5, 35.23) * mm});
            skLineSegment(sketch, "E748", {"start": v(-8.5, 35.23) * mm, "end": v(-8.22, 34.75) * mm});
            skLineSegment(sketch, "E749", {"start": v(-8.22, 34.75) * mm, "end": v(-8.1, 34.54) * mm});
            skArc(sketch, "E750", {"start": v(-8.1, 34.54) * mm, "mid": v(-7.79, 34.6) * mm, "end": v(-7.48, 34.68) * mm});
            skLineSegment(sketch, "E751", {"start": v(-7.48, 34.68) * mm, "end": v(-7.46, 34.92) * mm});
            skLineSegment(sketch, "E752", {"start": v(-7.46, 34.92) * mm, "end": v(-7.4, 35.47) * mm});
            skLineSegment(sketch, "E753", {"start": v(-7.4, 35.47) * mm, "end": v(-7.3, 36.1) * mm});
            skLineSegment(sketch, "E754", {"start": v(-7.3, 36.1) * mm, "end": v(-7.23, 36.5) * mm});
            skArc(sketch, "E755", {"start": v(-7.23, 36.5) * mm, "mid": v(-6.91, 36.55) * mm, "end": v(-6.6, 36.61) * mm});
            skLineSegment(sketch, "E756", {"start": v(-6.6, 36.61) * mm, "end": v(-6.38, 36.28) * mm});
            skLineSegment(sketch, "E757", {"start": v(-6.38, 36.28) * mm, "end": v(-6.06, 35.73) * mm});
            skLineSegment(sketch, "E758", {"start": v(-6.06, 35.73) * mm, "end": v(-5.8, 35.24) * mm});
            skLineSegment(sketch, "E759", {"start": v(-5.8, 35.24) * mm, "end": v(-5.7, 35.01) * mm});
            skArc(sketch, "E760", {"start": v(-5.7, 35.01) * mm, "mid": v(-5.38, 35.06) * mm, "end": v(-5.07, 35.11) * mm});
            skLineSegment(sketch, "E761", {"start": v(-5.07, 35.11) * mm, "end": v(-5.04, 35.35) * mm});
            skLineSegment(sketch, "E762", {"start": v(-5.04, 35.35) * mm, "end": v(-4.94, 35.9) * mm});
            skLineSegment(sketch, "E763", {"start": v(-4.94, 35.9) * mm, "end": v(-4.8, 36.53) * mm});
            skLineSegment(sketch, "E764", {"start": v(-4.8, 36.53) * mm, "end": v(-4.7, 36.9) * mm});
            skArc(sketch, "E765", {"start": v(-4.7, 36.9) * mm, "mid": v(-4.37, 36.94) * mm, "end": v(-4.05, 36.98) * mm});
            skLineSegment(sketch, "E766", {"start": v(-4.05, 36.98) * mm, "end": v(-3.86, 36.64) * mm});
            skLineSegment(sketch, "E767", {"start": v(-3.86, 36.64) * mm, "end": v(-3.58, 36.06) * mm});
            skLineSegment(sketch, "E768", {"start": v(-3.58, 36.06) * mm, "end": v(-3.36, 35.55) * mm});
            skLineSegment(sketch, "E769", {"start": v(-3.36, 35.55) * mm, "end": v(-3.27, 35.32) * mm});
            skArc(sketch, "E770", {"start": v(-3.27, 35.32) * mm, "mid": v(-2.95, 35.35) * mm, "end": v(-2.63, 35.38) * mm});
            skLineSegment(sketch, "E771", {"start": v(-2.63, 35.38) * mm, "end": v(-2.59, 35.62) * mm});
            skLineSegment(sketch, "E772", {"start": v(-2.59, 35.62) * mm, "end": v(-2.45, 36.16) * mm});
            skLineSegment(sketch, "E773", {"start": v(-2.45, 36.16) * mm, "end": v(-2.27, 36.77) * mm});
            skLineSegment(sketch, "E774", {"start": v(-2.27, 36.77) * mm, "end": v(-2.13, 37.14) * mm});
            skArc(sketch, "E775", {"start": v(-2.13, 37.14) * mm, "mid": v(-1.81, 37.16) * mm, "end": v(-1.5, 37.17) * mm});
            skLineSegment(sketch, "E776", {"start": v(-1.5, 37.17) * mm, "end": v(-1.33, 36.82) * mm});
            skLineSegment(sketch, "E777", {"start": v(-1.33, 36.82) * mm, "end": v(-1.08, 36.22) * mm});
            skLineSegment(sketch, "E778", {"start": v(-1.08, 36.22) * mm, "end": v(-0.9, 35.7) * mm});
            skLineSegment(sketch, "E779", {"start": v(-0.9, 35.7) * mm, "end": v(-0.82, 35.47) * mm});
            skArc(sketch, "E780", {"start": v(-0.82, 35.47) * mm, "mid": v(-0.5, 35.47) * mm, "end": v(-0.19, 35.47) * mm});
            skLineSegment(sketch, "E781", {"start": v(-0.19, 35.47) * mm, "end": v(-0.12, 35.71) * mm});
            skLineSegment(sketch, "E782", {"start": v(-0.12, 35.71) * mm, "end": v(0.05, 36.24) * mm});
            skLineSegment(sketch, "E783", {"start": v(0.05, 36.24) * mm, "end": v(0.28, 36.84) * mm});
            skLineSegment(sketch, "E784", {"start": v(0.28, 36.84) * mm, "end": v(0.43, 37.2) * mm});
            skArc(sketch, "E785", {"start": v(0.43, 37.2) * mm, "mid": v(0.75, 37.2) * mm, "end": v(1.07, 37.19) * mm});
            skLineSegment(sketch, "E786", {"start": v(1.07, 37.19) * mm, "end": v(1.22, 36.82) * mm});
            skLineSegment(sketch, "E787", {"start": v(1.22, 36.82) * mm, "end": v(1.42, 36.21) * mm});
            skLineSegment(sketch, "E788", {"start": v(1.42, 36.21) * mm, "end": v(1.57, 35.68) * mm});
            skLineSegment(sketch, "E789", {"start": v(1.57, 35.68) * mm, "end": v(1.62, 35.44) * mm});
            skArc(sketch, "E790", {"start": v(1.62, 35.44) * mm, "mid": v(1.94, 35.42) * mm, "end": v(2.26, 35.4) * mm});
            skLineSegment(sketch, "E791", {"start": v(2.26, 35.4) * mm, "end": v(2.34, 35.64) * mm});
            skLineSegment(sketch, "E792", {"start": v(2.34, 35.64) * mm, "end": v(2.55, 36.15) * mm});
            skLineSegment(sketch, "E793", {"start": v(2.55, 36.15) * mm, "end": v(2.82, 36.73) * mm});
            skLineSegment(sketch, "E794", {"start": v(2.82, 36.73) * mm, "end": v(3, 37.08) * mm});
            skArc(sketch, "E795", {"start": v(3, 37.08) * mm, "mid": v(3.32, 37.05) * mm, "end": v(3.64, 37.02) * mm});
            skLineSegment(sketch, "E796", {"start": v(3.64, 37.02) * mm, "end": v(3.75, 36.65) * mm});
            skLineSegment(sketch, "E797", {"start": v(3.75, 36.65) * mm, "end": v(3.92, 36.03) * mm});
            skLineSegment(sketch, "E798", {"start": v(3.92, 36.03) * mm, "end": v(4.03, 35.48) * mm});
            skLineSegment(sketch, "E799", {"start": v(4.03, 35.48) * mm, "end": v(4.07, 35.24) * mm});
            skArc(sketch, "E800", {"start": v(4.07, 35.24) * mm, "mid": v(4.38, 35.2) * mm, "end": v(4.7, 35.16) * mm});
            skLineSegment(sketch, "E801", {"start": v(4.7, 35.16) * mm, "end": v(4.8, 35.39) * mm});
            skLineSegment(sketch, "E802", {"start": v(4.8, 35.39) * mm, "end": v(5.04, 35.89) * mm});
            skLineSegment(sketch, "E803", {"start": v(5.04, 35.89) * mm, "end": v(5.35, 36.45) * mm});
            skLineSegment(sketch, "E804", {"start": v(5.35, 36.45) * mm, "end": v(5.55, 36.79) * mm});
            skArc(sketch, "E805", {"start": v(5.55, 36.79) * mm, "mid": v(5.87, 36.74) * mm, "end": v(6.18, 36.68) * mm});
            skLineSegment(sketch, "E806", {"start": v(6.18, 36.68) * mm, "end": v(6.27, 36.3) * mm});
            skLineSegment(sketch, "E807", {"start": v(6.27, 36.3) * mm, "end": v(6.4, 35.67) * mm});
            skLineSegment(sketch, "E808", {"start": v(6.4, 35.67) * mm, "end": v(6.47, 35.12) * mm});
            skLineSegment(sketch, "E809", {"start": v(6.47, 35.12) * mm, "end": v(6.49, 34.88) * mm});
            skArc(sketch, "E810", {"start": v(6.49, 34.88) * mm, "mid": v(6.8, 34.82) * mm, "end": v(7.11, 34.76) * mm});
            skLineSegment(sketch, "E811", {"start": v(7.11, 34.76) * mm, "end": v(7.22, 34.97) * mm});
            skLineSegment(sketch, "E812", {"start": v(7.22, 34.97) * mm, "end": v(7.5, 35.46) * mm});
            skLineSegment(sketch, "E813", {"start": v(7.5, 35.46) * mm, "end": v(7.85, 36) * mm});
            skLineSegment(sketch, "E814", {"start": v(7.85, 36) * mm, "end": v(8.08, 36.32) * mm});
            skArc(sketch, "E815", {"start": v(8.08, 36.32) * mm, "mid": v(8.39, 36.24) * mm, "end": v(8.7, 36.17) * mm});
            skLineSegment(sketch, "E816", {"start": v(8.7, 36.17) * mm, "end": v(8.76, 35.78) * mm});
            skLineSegment(sketch, "E817", {"start": v(8.76, 35.78) * mm, "end": v(8.84, 35.15) * mm});
            skLineSegment(sketch, "E818", {"start": v(8.84, 35.15) * mm, "end": v(8.87, 34.6) * mm});
            skLineSegment(sketch, "E819", {"start": v(8.87, 34.6) * mm, "end": v(8.88, 34.35) * mm});
            skArc(sketch, "E820", {"start": v(8.88, 34.35) * mm, "mid": v(9.19, 34.27) * mm, "end": v(9.5, 34.18) * mm});
            skLineSegment(sketch, "E821", {"start": v(9.5, 34.18) * mm, "end": v(9.62, 34.4) * mm});
            skLineSegment(sketch, "E822", {"start": v(9.62, 34.4) * mm, "end": v(9.93, 34.85) * mm});
            skLineSegment(sketch, "E823", {"start": v(9.93, 34.85) * mm, "end": v(10.31, 35.37) * mm});
            skLineSegment(sketch, "E824", {"start": v(10.31, 35.37) * mm, "end": v(10.56, 35.67) * mm});
            skArc(sketch, "E825", {"start": v(10.56, 35.67) * mm, "mid": v(10.87, 35.58) * mm, "end": v(11.17, 35.48) * mm});
            skLineSegment(sketch, "E826", {"start": v(11.17, 35.48) * mm, "end": v(11.21, 35.1) * mm});
            skLineSegment(sketch, "E827", {"start": v(11.21, 35.1) * mm, "end": v(11.24, 34.45) * mm});
            skLineSegment(sketch, "E828", {"start": v(11.24, 34.45) * mm, "end": v(11.24, 33.9) * mm});
            skLineSegment(sketch, "E829", {"start": v(11.24, 33.9) * mm, "end": v(11.23, 33.65) * mm});
            skArc(sketch, "E830", {"start": v(11.23, 33.65) * mm, "mid": v(11.53, 33.55) * mm, "end": v(11.83, 33.45) * mm});
            skLineSegment(sketch, "E831", {"start": v(11.83, 33.45) * mm, "end": v(11.97, 33.65) * mm});
            skLineSegment(sketch, "E832", {"start": v(11.97, 33.65) * mm, "end": v(12.31, 34.09) * mm});
            skLineSegment(sketch, "E833", {"start": v(12.31, 34.09) * mm, "end": v(12.73, 34.57) * mm});
            skLineSegment(sketch, "E834", {"start": v(12.73, 34.57) * mm, "end": v(13, 34.86) * mm});
            skArc(sketch, "E835", {"start": v(13, 34.86) * mm, "mid": v(13.3, 34.75) * mm, "end": v(13.6, 34.63) * mm});
            skLineSegment(sketch, "E836", {"start": v(13.6, 34.63) * mm, "end": v(13.6, 34.24) * mm});
            skLineSegment(sketch, "E837", {"start": v(13.6, 34.24) * mm, "end": v(13.6, 33.6) * mm});
            skLineSegment(sketch, "E838", {"start": v(13.6, 33.6) * mm, "end": v(13.55, 33.04) * mm});
            skLineSegment(sketch, "E839", {"start": v(13.55, 33.04) * mm, "end": v(13.52, 32.8) * mm});
            skArc(sketch, "E840", {"start": v(13.52, 32.8) * mm, "mid": v(13.82, 32.68) * mm, "end": v(14.1, 32.55) * mm});
            skLineSegment(sketch, "E841", {"start": v(14.1, 32.55) * mm, "end": v(14.26, 32.74) * mm});
            skLineSegment(sketch, "E842", {"start": v(14.26, 32.74) * mm, "end": v(14.63, 33.16) * mm});
            skLineSegment(sketch, "E843", {"start": v(14.63, 33.16) * mm, "end": v(15.08, 33.61) * mm});
            skLineSegment(sketch, "E844", {"start": v(15.08, 33.61) * mm, "end": v(15.37, 33.88) * mm});
            skArc(sketch, "E845", {"start": v(15.37, 33.88) * mm, "mid": v(15.66, 33.75) * mm, "end": v(15.95, 33.6) * mm});
            skLineSegment(sketch, "E846", {"start": v(15.95, 33.6) * mm, "end": v(15.94, 33.22) * mm});
            skLineSegment(sketch, "E847", {"start": v(15.94, 33.22) * mm, "end": v(15.88, 32.58) * mm});
            skLineSegment(sketch, "E848", {"start": v(15.88, 32.58) * mm, "end": v(15.8, 32.03) * mm});
            skLineSegment(sketch, "E849", {"start": v(15.8, 32.03) * mm, "end": v(15.75, 31.79) * mm});
            skArc(sketch, "E850", {"start": v(15.75, 31.79) * mm, "mid": v(16.04, 31.65) * mm, "end": v(16.32, 31.5) * mm});
            skLineSegment(sketch, "E851", {"start": v(16.32, 31.5) * mm, "end": v(16.49, 31.68) * mm});
            skLineSegment(sketch, "E852", {"start": v(16.49, 31.68) * mm, "end": v(16.89, 32.07) * mm});
            skLineSegment(sketch, "E853", {"start": v(16.89, 32.07) * mm, "end": v(17.37, 32.5) * mm});
            skLineSegment(sketch, "E854", {"start": v(17.37, 32.5) * mm, "end": v(17.67, 32.74) * mm});
            skArc(sketch, "E855", {"start": v(17.67, 32.74) * mm, "mid": v(17.95, 32.58) * mm, "end": v(18.23, 32.43) * mm});
            skLineSegment(sketch, "E856", {"start": v(18.23, 32.43) * mm, "end": v(18.19, 32.04) * mm});
            skLineSegment(sketch, "E857", {"start": v(18.19, 32.04) * mm, "end": v(18.09, 31.4) * mm});
            skLineSegment(sketch, "E858", {"start": v(18.09, 31.4) * mm, "end": v(17.97, 30.86) * mm});
            skLineSegment(sketch, "E859", {"start": v(17.97, 30.86) * mm, "end": v(17.9, 30.63) * mm});
            skArc(sketch, "E860", {"start": v(17.9, 30.63) * mm, "mid": v(18.18, 30.46) * mm, "end": v(18.46, 30.3) * mm});
            skLineSegment(sketch, "E861", {"start": v(18.46, 30.3) * mm, "end": v(18.63, 30.47) * mm});
            skLineSegment(sketch, "E862", {"start": v(18.63, 30.47) * mm, "end": v(19.06, 30.83) * mm});
            skLineSegment(sketch, "E863", {"start": v(19.06, 30.83) * mm, "end": v(19.57, 31.22) * mm});
            skLineSegment(sketch, "E864", {"start": v(19.57, 31.22) * mm, "end": v(19.89, 31.44) * mm});
            skArc(sketch, "E865", {"start": v(19.89, 31.44) * mm, "mid": v(20.16, 31.27) * mm, "end": v(20.43, 31.1) * mm});
            skLineSegment(sketch, "E866", {"start": v(20.43, 31.1) * mm, "end": v(20.36, 30.7) * mm});
            skLineSegment(sketch, "E867", {"start": v(20.36, 30.7) * mm, "end": v(20.21, 30.08) * mm});
            skLineSegment(sketch, "E868", {"start": v(20.21, 30.08) * mm, "end": v(20.06, 29.55) * mm});
            skLineSegment(sketch, "E869", {"start": v(20.06, 29.55) * mm, "end": v(19.98, 29.32) * mm});
            skArc(sketch, "E870", {"start": v(19.98, 29.32) * mm, "mid": v(20.24, 29.14) * mm, "end": v(20.5, 28.95) * mm});
            skLineSegment(sketch, "E871", {"start": v(20.5, 28.95) * mm, "end": v(20.7, 29.1) * mm});
            skLineSegment(sketch, "E872", {"start": v(20.7, 29.1) * mm, "end": v(21.14, 29.44) * mm});
            skLineSegment(sketch, "E873", {"start": v(21.14, 29.44) * mm, "end": v(21.67, 29.8) * mm});
            skLineSegment(sketch, "E874", {"start": v(21.67, 29.8) * mm, "end": v(22, 30) * mm});
            skArc(sketch, "E875", {"start": v(22, 30) * mm, "mid": v(22.27, 29.8) * mm, "end": v(22.52, 29.61) * mm});
            skLineSegment(sketch, "E876", {"start": v(22.52, 29.61) * mm, "end": v(22.43, 29.23) * mm});
            skLineSegment(sketch, "E877", {"start": v(22.43, 29.23) * mm, "end": v(22.24, 28.62) * mm});
            skLineSegment(sketch, "E878", {"start": v(22.24, 28.62) * mm, "end": v(22.05, 28.1) * mm});
            skLineSegment(sketch, "E879", {"start": v(22.05, 28.1) * mm, "end": v(21.95, 27.87) * mm});
            skArc(sketch, "E880", {"start": v(21.95, 27.87) * mm, "mid": v(22.2, 27.67) * mm, "end": v(22.45, 27.47) * mm});
            skLineSegment(sketch, "E881", {"start": v(22.45, 27.47) * mm, "end": v(22.65, 27.61) * mm});
            skLineSegment(sketch, "E882", {"start": v(22.65, 27.61) * mm, "end": v(23.12, 27.91) * mm});
            skLineSegment(sketch, "E883", {"start": v(23.12, 27.91) * mm, "end": v(23.68, 28.23) * mm});
            skLineSegment(sketch, "E884", {"start": v(23.68, 28.23) * mm, "end": v(24.03, 28.4) * mm});
            skArc(sketch, "E885", {"start": v(24.03, 28.4) * mm, "mid": v(24.27, 28.2) * mm, "end": v(24.51, 27.99) * mm});
            skLineSegment(sketch, "E886", {"start": v(24.51, 27.99) * mm, "end": v(24.39, 27.62) * mm});
            skLineSegment(sketch, "E887", {"start": v(24.39, 27.62) * mm, "end": v(24.16, 27.02) * mm});
            skLineSegment(sketch, "E888", {"start": v(24.16, 27.02) * mm, "end": v(23.93, 26.5) * mm});
            skLineSegment(sketch, "E889", {"start": v(23.93, 26.5) * mm, "end": v(23.82, 26.29) * mm});
            skArc(sketch, "E890", {"start": v(23.82, 26.29) * mm, "mid": v(24.06, 26.07) * mm, "end": v(24.3, 25.86) * mm});
            skLineSegment(sketch, "E891", {"start": v(24.3, 25.86) * mm, "end": v(24.5, 25.99) * mm});
            skLineSegment(sketch, "E892", {"start": v(24.5, 25.99) * mm, "end": v(24.99, 26.25) * mm});
            skLineSegment(sketch, "E893", {"start": v(24.99, 26.25) * mm, "end": v(25.57, 26.53) * mm});
            skLineSegment(sketch, "E894", {"start": v(25.57, 26.53) * mm, "end": v(25.93, 26.68) * mm});
            skArc(sketch, "E895", {"start": v(25.93, 26.68) * mm, "mid": v(26.16, 26.46) * mm, "end": v(26.38, 26.23) * mm});
            skLineSegment(sketch, "E896", {"start": v(26.38, 26.23) * mm, "end": v(26.24, 25.87) * mm});
            skLineSegment(sketch, "E897", {"start": v(26.24, 25.87) * mm, "end": v(25.97, 25.29) * mm});
            skLineSegment(sketch, "E898", {"start": v(25.97, 25.29) * mm, "end": v(25.7, 24.8) * mm});
            skLineSegment(sketch, "E899", {"start": v(25.7, 24.8) * mm, "end": v(25.58, 24.58) * mm});
            skArc(sketch, "E900", {"start": v(25.58, 24.58) * mm, "mid": v(25.8, 24.35) * mm, "end": v(26.02, 24.12) * mm});
            skLineSegment(sketch, "E901", {"start": v(26.02, 24.12) * mm, "end": v(26.24, 24.23) * mm});
            skLineSegment(sketch, "E902", {"start": v(26.24, 24.23) * mm, "end": v(26.74, 24.46) * mm});
            skLineSegment(sketch, "E903", {"start": v(26.74, 24.46) * mm, "end": v(27.34, 24.7) * mm});
            skLineSegment(sketch, "E904", {"start": v(27.34, 24.7) * mm, "end": v(27.7, 24.83) * mm});
            skArc(sketch, "E905", {"start": v(27.7, 24.83) * mm, "mid": v(27.92, 24.59) * mm, "end": v(28.13, 24.35) * mm});
            skLineSegment(sketch, "E906", {"start": v(28.13, 24.35) * mm, "end": v(27.96, 24) * mm});
            skLineSegment(sketch, "E907", {"start": v(27.96, 24) * mm, "end": v(27.65, 23.43) * mm});
            skLineSegment(sketch, "E908", {"start": v(27.65, 23.43) * mm, "end": v(27.36, 22.96) * mm});
            skLineSegment(sketch, "E909", {"start": v(27.36, 22.96) * mm, "end": v(27.22, 22.76) * mm});
            skArc(sketch, "E910", {"start": v(27.22, 22.76) * mm, "mid": v(27.42, 22.52) * mm, "end": v(27.62, 22.27) * mm});
            skSolve(sketch);
        }
        {
            var Q0;
            Q0=qCreatedBy(makeId("Top.planeOp"),FACE);
            var sketch = newSketch(context, id + "F2", { "sketchPlane" : qUnion([Q0])});
            skCircle(sketch, "E911", {"center": v(0.04, 0.01) * mm, "radius": 1.5 * mm});
            skLineSegment(sketch, "E912", {"start": v(2.72, 3.34) * mm, "end": v(3.1, 3.82) * mm});
            skLineSegment(sketch, "E913", {"start": v(3.1, 3.82) * mm, "end": v(3.11, 3.82) * mm});
            skLineSegment(sketch, "E914", {"start": v(3.11, 3.82) * mm, "end": v(3.12, 3.84) * mm});
            skLineSegment(sketch, "E915", {"start": v(3.12, 3.84) * mm, "end": v(3.15, 3.86) * mm});
            skLineSegment(sketch, "E916", {"start": v(3.15, 3.86) * mm, "end": v(3.18, 3.89) * mm});
            skLineSegment(sketch, "E917", {"start": v(3.18, 3.89) * mm, "end": v(3.22, 3.92) * mm});
            skLineSegment(sketch, "E918", {"start": v(3.22, 3.92) * mm, "end": v(3.28, 3.96) * mm});
            skLineSegment(sketch, "E919", {"start": v(3.28, 3.96) * mm, "end": v(3.34, 4) * mm});
            skLineSegment(sketch, "E920", {"start": v(3.34, 4) * mm, "end": v(3.42, 4.05) * mm});
            skLineSegment(sketch, "E921", {"start": v(3.42, 4.05) * mm, "end": v(3.52, 4.1) * mm});
            skLineSegment(sketch, "E922", {"start": v(3.52, 4.1) * mm, "end": v(3.62, 4.14) * mm});
            skLineSegment(sketch, "E923", {"start": v(3.62, 4.14) * mm, "end": v(3.74, 4.19) * mm});
            skLineSegment(sketch, "E924", {"start": v(3.74, 4.19) * mm, "end": v(3.88, 4.23) * mm});
            skLineSegment(sketch, "E925", {"start": v(3.88, 4.23) * mm, "end": v(4.02, 4.27) * mm});
            skLineSegment(sketch, "E926", {"start": v(4.02, 4.27) * mm, "end": v(4.18, 4.3) * mm});
            skLineSegment(sketch, "E927", {"start": v(4.18, 4.3) * mm, "end": v(4.23, 4.31) * mm});
            skArc(sketch, "E928", {"start": v(4.23, 4.31) * mm, "mid": v(4.4, 4.13) * mm, "end": v(4.57, 3.95) * mm});
            skLineSegment(sketch, "E929", {"start": v(4.57, 3.95) * mm, "end": v(4.57, 3.9) * mm});
            skLineSegment(sketch, "E930", {"start": v(4.57, 3.9) * mm, "end": v(4.52, 3.74) * mm});
            skLineSegment(sketch, "E931", {"start": v(4.52, 3.74) * mm, "end": v(4.47, 3.6) * mm});
            skLineSegment(sketch, "E932", {"start": v(4.47, 3.6) * mm, "end": v(4.42, 3.47) * mm});
            skLineSegment(sketch, "E933", {"start": v(4.42, 3.47) * mm, "end": v(4.37, 3.35) * mm});
            skLineSegment(sketch, "E934", {"start": v(4.37, 3.35) * mm, "end": v(4.31, 3.25) * mm});
            skLineSegment(sketch, "E935", {"start": v(4.31, 3.25) * mm, "end": v(4.26, 3.16) * mm});
            skLineSegment(sketch, "E936", {"start": v(4.26, 3.16) * mm, "end": v(4.21, 3.08) * mm});
            skLineSegment(sketch, "E937", {"start": v(4.21, 3.08) * mm, "end": v(4.17, 3.02) * mm});
            skLineSegment(sketch, "E938", {"start": v(4.17, 3.02) * mm, "end": v(4.12, 2.97) * mm});
            skLineSegment(sketch, "E939", {"start": v(4.12, 2.97) * mm, "end": v(4.09, 2.92) * mm});
            skLineSegment(sketch, "E940", {"start": v(4.09, 2.92) * mm, "end": v(4.06, 2.9) * mm});
            skLineSegment(sketch, "E941", {"start": v(4.06, 2.9) * mm, "end": v(4.04, 2.87) * mm});
            skLineSegment(sketch, "E942", {"start": v(4.04, 2.87) * mm, "end": v(4.02, 2.86) * mm});
            skLineSegment(sketch, "E943", {"start": v(4.02, 2.86) * mm, "end": v(4.02, 2.86) * mm});
            skLineSegment(sketch, "E944", {"start": v(4.02, 2.86) * mm, "end": v(3.52, 2.5) * mm});
            skArc(sketch, "E945", {"start": v(3.52, 2.5) * mm, "mid": v(3.76, 2.12) * mm, "end": v(3.96, 1.72) * mm});
            skLineSegment(sketch, "E946", {"start": v(3.96, 1.72) * mm, "end": v(4.53, 1.96) * mm});
            skLineSegment(sketch, "E947", {"start": v(4.53, 1.96) * mm, "end": v(4.53, 1.96) * mm});
            skLineSegment(sketch, "E948", {"start": v(4.53, 1.96) * mm, "end": v(4.55, 1.97) * mm});
            skLineSegment(sketch, "E949", {"start": v(4.55, 1.97) * mm, "end": v(4.58, 1.98) * mm});
            skLineSegment(sketch, "E950", {"start": v(4.58, 1.98) * mm, "end": v(4.62, 1.99) * mm});
            skLineSegment(sketch, "E951", {"start": v(4.62, 1.99) * mm, "end": v(4.67, 2) * mm});
            skLineSegment(sketch, "E952", {"start": v(4.67, 2) * mm, "end": v(4.74, 2) * mm});
            skLineSegment(sketch, "E953", {"start": v(4.74, 2) * mm, "end": v(4.82, 2.01) * mm});
            skLineSegment(sketch, "E954", {"start": v(4.82, 2.01) * mm, "end": v(4.91, 2.01) * mm});
            skLineSegment(sketch, "E955", {"start": v(4.91, 2.01) * mm, "end": v(5.01, 2.01) * mm});
            skLineSegment(sketch, "E956", {"start": v(5.01, 2.01) * mm, "end": v(5.13, 2) * mm});
            skLineSegment(sketch, "E957", {"start": v(5.13, 2) * mm, "end": v(5.26, 1.99) * mm});
            skLineSegment(sketch, "E958", {"start": v(5.26, 1.99) * mm, "end": v(5.4, 1.97) * mm});
            skLineSegment(sketch, "E959", {"start": v(5.4, 1.97) * mm, "end": v(5.55, 1.93) * mm});
            skLineSegment(sketch, "E960", {"start": v(5.55, 1.93) * mm, "end": v(5.7, 1.9) * mm});
            skLineSegment(sketch, "E961", {"start": v(5.7, 1.9) * mm, "end": v(5.75, 1.88) * mm});
            skArc(sketch, "E962", {"start": v(5.75, 1.88) * mm, "mid": v(5.82, 1.63) * mm, "end": v(5.88, 1.39) * mm});
            skLineSegment(sketch, "E963", {"start": v(5.88, 1.39) * mm, "end": v(5.85, 1.36) * mm});
            skLineSegment(sketch, "E964", {"start": v(5.85, 1.36) * mm, "end": v(5.74, 1.24) * mm});
            skLineSegment(sketch, "E965", {"start": v(5.74, 1.24) * mm, "end": v(5.63, 1.13) * mm});
            skLineSegment(sketch, "E966", {"start": v(5.63, 1.13) * mm, "end": v(5.52, 1.04) * mm});
            skLineSegment(sketch, "E967", {"start": v(5.52, 1.04) * mm, "end": v(5.42, 0.96) * mm});
            skLineSegment(sketch, "E968", {"start": v(5.42, 0.96) * mm, "end": v(5.33, 0.9) * mm});
            skLineSegment(sketch, "E969", {"start": v(5.33, 0.9) * mm, "end": v(5.24, 0.84) * mm});
            skLineSegment(sketch, "E970", {"start": v(5.24, 0.84) * mm, "end": v(5.16, 0.8) * mm});
            skLineSegment(sketch, "E971", {"start": v(5.16, 0.8) * mm, "end": v(5.09, 0.76) * mm});
            skLineSegment(sketch, "E972", {"start": v(5.09, 0.76) * mm, "end": v(5.03, 0.73) * mm});
            skLineSegment(sketch, "E973", {"start": v(5.03, 0.73) * mm, "end": v(4.98, 0.71) * mm});
            skLineSegment(sketch, "E974", {"start": v(4.98, 0.71) * mm, "end": v(4.94, 0.7) * mm});
            skLineSegment(sketch, "E975", {"start": v(4.94, 0.7) * mm, "end": v(4.9, 0.69) * mm});
            skLineSegment(sketch, "E976", {"start": v(4.9, 0.69) * mm, "end": v(4.89, 0.69) * mm});
            skLineSegment(sketch, "E977", {"start": v(4.89, 0.69) * mm, "end": v(4.88, 0.68) * mm});
            skLineSegment(sketch, "E978", {"start": v(4.88, 0.68) * mm, "end": v(4.28, 0.6) * mm});
            skArc(sketch, "E979", {"start": v(4.28, 0.6) * mm, "mid": v(4.31, 0.15) * mm, "end": v(4.3, -0.3) * mm});
            skLineSegment(sketch, "E980", {"start": v(4.3, -0.3) * mm, "end": v(4.92, -0.35) * mm});
            skLineSegment(sketch, "E981", {"start": v(4.92, -0.35) * mm, "end": v(4.92, -0.35) * mm});
            skLineSegment(sketch, "E982", {"start": v(4.92, -0.35) * mm, "end": v(4.94, -0.35) * mm});
            skLineSegment(sketch, "E983", {"start": v(4.94, -0.35) * mm, "end": v(4.97, -0.36) * mm});
            skLineSegment(sketch, "E984", {"start": v(4.97, -0.36) * mm, "end": v(5.01, -0.37) * mm});
            skLineSegment(sketch, "E985", {"start": v(5.01, -0.37) * mm, "end": v(5.06, -0.38) * mm});
            skLineSegment(sketch, "E986", {"start": v(5.06, -0.38) * mm, "end": v(5.13, -0.4) * mm});
            skLineSegment(sketch, "E987", {"start": v(5.13, -0.4) * mm, "end": v(5.2, -0.44) * mm});
            skLineSegment(sketch, "E988", {"start": v(5.2, -0.44) * mm, "end": v(5.28, -0.48) * mm});
            skLineSegment(sketch, "E989", {"start": v(5.28, -0.48) * mm, "end": v(5.37, -0.53) * mm});
            skLineSegment(sketch, "E990", {"start": v(5.37, -0.53) * mm, "end": v(5.47, -0.59) * mm});
            skLineSegment(sketch, "E991", {"start": v(5.47, -0.59) * mm, "end": v(5.58, -0.66) * mm});
            skLineSegment(sketch, "E992", {"start": v(5.58, -0.66) * mm, "end": v(5.69, -0.75) * mm});
            skLineSegment(sketch, "E993", {"start": v(5.69, -0.75) * mm, "end": v(5.8, -0.84) * mm});
            skLineSegment(sketch, "E994", {"start": v(5.8, -0.84) * mm, "end": v(5.93, -0.96) * mm});
            skLineSegment(sketch, "E995", {"start": v(5.93, -0.96) * mm, "end": v(5.96, -0.99) * mm});
            skArc(sketch, "E996", {"start": v(5.96, -0.99) * mm, "mid": v(5.91, -1.24) * mm, "end": v(5.85, -1.48) * mm});
            skLineSegment(sketch, "E997", {"start": v(5.85, -1.48) * mm, "end": v(5.81, -1.5) * mm});
            skLineSegment(sketch, "E998", {"start": v(5.81, -1.5) * mm, "end": v(5.66, -1.55) * mm});
            skLineSegment(sketch, "E999", {"start": v(5.66, -1.55) * mm, "end": v(5.5, -1.6) * mm});
            skLineSegment(sketch, "E1000", {"start": v(5.5, -1.6) * mm, "end": v(5.37, -1.63) * mm});
            skLineSegment(sketch, "E1001", {"start": v(5.37, -1.63) * mm, "end": v(5.25, -1.65) * mm});
            skLineSegment(sketch, "E1002", {"start": v(5.25, -1.65) * mm, "end": v(5.13, -1.66) * mm});
            skLineSegment(sketch, "E1003", {"start": v(5.13, -1.66) * mm, "end": v(5.03, -1.67) * mm});
            skLineSegment(sketch, "E1004", {"start": v(5.03, -1.67) * mm, "end": v(4.94, -1.68) * mm});
            skLineSegment(sketch, "E1005", {"start": v(4.94, -1.68) * mm, "end": v(4.86, -1.67) * mm});
            skLineSegment(sketch, "E1006", {"start": v(4.86, -1.67) * mm, "end": v(4.79, -1.67) * mm});
            skLineSegment(sketch, "E1007", {"start": v(4.79, -1.67) * mm, "end": v(4.73, -1.66) * mm});
            skLineSegment(sketch, "E1008", {"start": v(4.73, -1.66) * mm, "end": v(4.7, -1.65) * mm});
            skLineSegment(sketch, "E1009", {"start": v(4.7, -1.65) * mm, "end": v(4.66, -1.65) * mm});
            skLineSegment(sketch, "E1010", {"start": v(4.66, -1.65) * mm, "end": v(4.65, -1.64) * mm});
            skLineSegment(sketch, "E1011", {"start": v(4.65, -1.64) * mm, "end": v(4.64, -1.64) * mm});
            skLineSegment(sketch, "E1012", {"start": v(4.64, -1.64) * mm, "end": v(4.06, -1.43) * mm});
            skArc(sketch, "E1013", {"start": v(4.06, -1.43) * mm, "mid": v(3.89, -1.85) * mm, "end": v(3.67, -2.25) * mm});
            skLineSegment(sketch, "E1014", {"start": v(3.67, -2.25) * mm, "end": v(4.19, -2.57) * mm});
            skLineSegment(sketch, "E1015", {"start": v(4.19, -2.57) * mm, "end": v(4.2, -2.57) * mm});
            skLineSegment(sketch, "E1016", {"start": v(4.2, -2.57) * mm, "end": v(4.2, -2.58) * mm});
            skLineSegment(sketch, "E1017", {"start": v(4.2, -2.58) * mm, "end": v(4.23, -2.6) * mm});
            skLineSegment(sketch, "E1018", {"start": v(4.23, -2.6) * mm, "end": v(4.26, -2.63) * mm});
            skLineSegment(sketch, "E1019", {"start": v(4.26, -2.63) * mm, "end": v(4.3, -2.67) * mm});
            skLineSegment(sketch, "E1020", {"start": v(4.3, -2.67) * mm, "end": v(4.35, -2.72) * mm});
            skLineSegment(sketch, "E1021", {"start": v(4.35, -2.72) * mm, "end": v(4.4, -2.78) * mm});
            skLineSegment(sketch, "E1022", {"start": v(4.4, -2.78) * mm, "end": v(4.45, -2.86) * mm});
            skLineSegment(sketch, "E1023", {"start": v(4.45, -2.86) * mm, "end": v(4.51, -2.94) * mm});
            skLineSegment(sketch, "E1024", {"start": v(4.51, -2.94) * mm, "end": v(4.57, -3.04) * mm});
            skLineSegment(sketch, "E1025", {"start": v(4.57, -3.04) * mm, "end": v(4.63, -3.16) * mm});
            skLineSegment(sketch, "E1026", {"start": v(4.63, -3.16) * mm, "end": v(4.69, -3.28) * mm});
            skLineSegment(sketch, "E1027", {"start": v(4.69, -3.28) * mm, "end": v(4.75, -3.42) * mm});
            skLineSegment(sketch, "E1028", {"start": v(4.75, -3.42) * mm, "end": v(4.8, -3.58) * mm});
            skLineSegment(sketch, "E1029", {"start": v(4.8, -3.58) * mm, "end": v(4.81, -3.62) * mm});
            skArc(sketch, "E1030", {"start": v(4.81, -3.62) * mm, "mid": v(4.66, -3.82) * mm, "end": v(4.5, -4.01) * mm});
            skLineSegment(sketch, "E1031", {"start": v(4.5, -4.01) * mm, "end": v(4.45, -4) * mm});
            skLineSegment(sketch, "E1032", {"start": v(4.45, -4) * mm, "end": v(4.28, -3.98) * mm});
            skLineSegment(sketch, "E1033", {"start": v(4.28, -3.98) * mm, "end": v(4.13, -3.95) * mm});
            skLineSegment(sketch, "E1034", {"start": v(4.13, -3.95) * mm, "end": v(4, -3.92) * mm});
            skLineSegment(sketch, "E1035", {"start": v(4, -3.92) * mm, "end": v(3.88, -3.88) * mm});
            skLineSegment(sketch, "E1036", {"start": v(3.88, -3.88) * mm, "end": v(3.77, -3.84) * mm});
            skLineSegment(sketch, "E1037", {"start": v(3.77, -3.84) * mm, "end": v(3.67, -3.8) * mm});
            skLineSegment(sketch, "E1038", {"start": v(3.67, -3.8) * mm, "end": v(3.59, -3.76) * mm});
            skLineSegment(sketch, "E1039", {"start": v(3.59, -3.76) * mm, "end": v(3.52, -3.72) * mm});
            skLineSegment(sketch, "E1040", {"start": v(3.52, -3.72) * mm, "end": v(3.46, -3.68) * mm});
            skLineSegment(sketch, "E1041", {"start": v(3.46, -3.68) * mm, "end": v(3.42, -3.65) * mm});
            skLineSegment(sketch, "E1042", {"start": v(3.42, -3.65) * mm, "end": v(3.38, -3.62) * mm});
            skLineSegment(sketch, "E1043", {"start": v(3.38, -3.62) * mm, "end": v(3.36, -3.6) * mm});
            skLineSegment(sketch, "E1044", {"start": v(3.36, -3.6) * mm, "end": v(3.35, -3.6) * mm});
            skLineSegment(sketch, "E1045", {"start": v(3.35, -3.6) * mm, "end": v(3.34, -3.59) * mm});
            skLineSegment(sketch, "E1046", {"start": v(3.34, -3.59) * mm, "end": v(2.93, -3.14) * mm});
            skArc(sketch, "E1047", {"start": v(2.93, -3.14) * mm, "mid": v(2.58, -3.42) * mm, "end": v(2.2, -3.67) * mm});
            skLineSegment(sketch, "E1048", {"start": v(2.2, -3.67) * mm, "end": v(2.51, -4.2) * mm});
            skLineSegment(sketch, "E1049", {"start": v(2.51, -4.2) * mm, "end": v(2.52, -4.2) * mm});
            skLineSegment(sketch, "E1050", {"start": v(2.52, -4.2) * mm, "end": v(2.52, -4.22) * mm});
            skLineSegment(sketch, "E1051", {"start": v(2.52, -4.22) * mm, "end": v(2.54, -4.25) * mm});
            skLineSegment(sketch, "E1052", {"start": v(2.54, -4.25) * mm, "end": v(2.55, -4.3) * mm});
            skLineSegment(sketch, "E1053", {"start": v(2.55, -4.3) * mm, "end": v(2.57, -4.34) * mm});
            skLineSegment(sketch, "E1054", {"start": v(2.57, -4.34) * mm, "end": v(2.58, -4.4) * mm});
            skLineSegment(sketch, "E1055", {"start": v(2.58, -4.4) * mm, "end": v(2.6, -4.49) * mm});
            skLineSegment(sketch, "E1056", {"start": v(2.6, -4.49) * mm, "end": v(2.61, -4.58) * mm});
            skLineSegment(sketch, "E1057", {"start": v(2.61, -4.58) * mm, "end": v(2.62, -4.68) * mm});
            skLineSegment(sketch, "E1058", {"start": v(2.62, -4.68) * mm, "end": v(2.63, -4.8) * mm});
            skLineSegment(sketch, "E1059", {"start": v(2.63, -4.8) * mm, "end": v(2.63, -4.92) * mm});
            skLineSegment(sketch, "E1060", {"start": v(2.63, -4.92) * mm, "end": v(2.62, -5.06) * mm});
            skLineSegment(sketch, "E1061", {"start": v(2.62, -5.06) * mm, "end": v(2.61, -5.22) * mm});
            skLineSegment(sketch, "E1062", {"start": v(2.61, -5.22) * mm, "end": v(2.59, -5.38) * mm});
            skLineSegment(sketch, "E1063", {"start": v(2.59, -5.38) * mm, "end": v(2.58, -5.42) * mm});
            skArc(sketch, "E1064", {"start": v(2.58, -5.42) * mm, "mid": v(2.35, -5.53) * mm, "end": v(2.11, -5.62) * mm});
            skLineSegment(sketch, "E1065", {"start": v(2.11, -5.62) * mm, "end": v(2.07, -5.6) * mm});
            skLineSegment(sketch, "E1066", {"start": v(2.07, -5.6) * mm, "end": v(1.94, -5.5) * mm});
            skLineSegment(sketch, "E1067", {"start": v(1.94, -5.5) * mm, "end": v(1.82, -5.4) * mm});
            skLineSegment(sketch, "E1068", {"start": v(1.82, -5.4) * mm, "end": v(1.72, -5.3) * mm});
            skLineSegment(sketch, "E1069", {"start": v(1.72, -5.3) * mm, "end": v(1.63, -5.21) * mm});
            skLineSegment(sketch, "E1070", {"start": v(1.63, -5.21) * mm, "end": v(1.55, -5.13) * mm});
            skLineSegment(sketch, "E1071", {"start": v(1.55, -5.13) * mm, "end": v(1.49, -5.05) * mm});
            skLineSegment(sketch, "E1072", {"start": v(1.49, -5.05) * mm, "end": v(1.43, -4.97) * mm});
            skLineSegment(sketch, "E1073", {"start": v(1.43, -4.97) * mm, "end": v(1.39, -4.9) * mm});
            skLineSegment(sketch, "E1074", {"start": v(1.39, -4.9) * mm, "end": v(1.35, -4.85) * mm});
            skLineSegment(sketch, "E1075", {"start": v(1.35, -4.85) * mm, "end": v(1.33, -4.8) * mm});
            skLineSegment(sketch, "E1076", {"start": v(1.33, -4.8) * mm, "end": v(1.3, -4.76) * mm});
            skLineSegment(sketch, "E1077", {"start": v(1.3, -4.76) * mm, "end": v(1.3, -4.73) * mm});
            skLineSegment(sketch, "E1078", {"start": v(1.3, -4.73) * mm, "end": v(1.3, -4.72) * mm});
            skLineSegment(sketch, "E1079", {"start": v(1.3, -4.72) * mm, "end": v(1.3, -4.7) * mm});
            skLineSegment(sketch, "E1080", {"start": v(1.3, -4.7) * mm, "end": v(1.13, -4.12) * mm});
            skArc(sketch, "E1081", {"start": v(1.13, -4.12) * mm, "mid": v(0.7, -4.2) * mm, "end": v(0.24, -4.25) * mm});
            skLineSegment(sketch, "E1082", {"start": v(0.24, -4.25) * mm, "end": v(0.27, -4.87) * mm});
            skLineSegment(sketch, "E1083", {"start": v(0.27, -4.87) * mm, "end": v(0.27, -4.87) * mm});
            skLineSegment(sketch, "E1084", {"start": v(0.27, -4.87) * mm, "end": v(0.27, -4.9) * mm});
            skLineSegment(sketch, "E1085", {"start": v(0.27, -4.9) * mm, "end": v(0.27, -4.92) * mm});
            skLineSegment(sketch, "E1086", {"start": v(0.27, -4.92) * mm, "end": v(0.26, -4.96) * mm});
            skLineSegment(sketch, "E1087", {"start": v(0.26, -4.96) * mm, "end": v(0.25, -5.02) * mm});
            skLineSegment(sketch, "E1088", {"start": v(0.25, -5.02) * mm, "end": v(0.24, -5.08) * mm});
            skLineSegment(sketch, "E1089", {"start": v(0.24, -5.08) * mm, "end": v(0.21, -5.16) * mm});
            skLineSegment(sketch, "E1090", {"start": v(0.21, -5.16) * mm, "end": v(0.18, -5.25) * mm});
            skLineSegment(sketch, "E1091", {"start": v(0.18, -5.25) * mm, "end": v(0.15, -5.34) * mm});
            skLineSegment(sketch, "E1092", {"start": v(0.15, -5.34) * mm, "end": v(0.1, -5.45) * mm});
            skLineSegment(sketch, "E1093", {"start": v(0.1, -5.45) * mm, "end": v(0.04, -5.56) * mm});
            skLineSegment(sketch, "E1094", {"start": v(0.04, -5.56) * mm, "end": v(-0.03, -5.68) * mm});
            skLineSegment(sketch, "E1095", {"start": v(-0.03, -5.68) * mm, "end": v(-0.12, -5.81) * mm});
            skLineSegment(sketch, "E1096", {"start": v(-0.12, -5.81) * mm, "end": v(-0.21, -5.94) * mm});
            skLineSegment(sketch, "E1097", {"start": v(-0.21, -5.94) * mm, "end": v(-0.24, -5.98) * mm});
            skArc(sketch, "E1098", {"start": v(-0.24, -5.98) * mm, "mid": v(-0.5, -5.96) * mm, "end": v(-0.74, -5.93) * mm});
            skLineSegment(sketch, "E1099", {"start": v(-0.74, -5.93) * mm, "end": v(-0.77, -5.9) * mm});
            skLineSegment(sketch, "E1100", {"start": v(-0.77, -5.9) * mm, "end": v(-0.84, -5.75) * mm});
            skLineSegment(sketch, "E1101", {"start": v(-0.84, -5.75) * mm, "end": v(-0.9, -5.6) * mm});
            skLineSegment(sketch, "E1102", {"start": v(-0.9, -5.6) * mm, "end": v(-0.94, -5.47) * mm});
            skLineSegment(sketch, "E1103", {"start": v(-0.94, -5.47) * mm, "end": v(-0.98, -5.35) * mm});
            skLineSegment(sketch, "E1104", {"start": v(-0.98, -5.35) * mm, "end": v(-1.01, -5.24) * mm});
            skLineSegment(sketch, "E1105", {"start": v(-1.01, -5.24) * mm, "end": v(-1.03, -5.14) * mm});
            skLineSegment(sketch, "E1106", {"start": v(-1.03, -5.14) * mm, "end": v(-1.05, -5.05) * mm});
            skLineSegment(sketch, "E1107", {"start": v(-1.05, -5.05) * mm, "end": v(-1.05, -4.97) * mm});
            skLineSegment(sketch, "E1108", {"start": v(-1.05, -4.97) * mm, "end": v(-1.06, -4.9) * mm});
            skLineSegment(sketch, "E1109", {"start": v(-1.06, -4.9) * mm, "end": v(-1.06, -4.85) * mm});
            skLineSegment(sketch, "E1110", {"start": v(-1.06, -4.85) * mm, "end": v(-1.05, -4.8) * mm});
            skLineSegment(sketch, "E1111", {"start": v(-1.05, -4.8) * mm, "end": v(-1.05, -4.77) * mm});
            skLineSegment(sketch, "E1112", {"start": v(-1.05, -4.77) * mm, "end": v(-1.05, -4.75) * mm});
            skLineSegment(sketch, "E1113", {"start": v(-1.05, -4.75) * mm, "end": v(-1.05, -4.75) * mm});
            skLineSegment(sketch, "E1114", {"start": v(-1.05, -4.75) * mm, "end": v(-0.91, -4.15) * mm});
            skArc(sketch, "E1115", {"start": v(-0.91, -4.15) * mm, "mid": v(-1.35, -4.03) * mm, "end": v(-1.77, -3.86) * mm});
            skLineSegment(sketch, "E1116", {"start": v(-1.77, -3.86) * mm, "end": v(-2.02, -4.41) * mm});
            skLineSegment(sketch, "E1117", {"start": v(-2.02, -4.41) * mm, "end": v(-2.03, -4.42) * mm});
            skLineSegment(sketch, "E1118", {"start": v(-2.03, -4.42) * mm, "end": v(-2.04, -4.43) * mm});
            skLineSegment(sketch, "E1119", {"start": v(-2.04, -4.43) * mm, "end": v(-2.05, -4.46) * mm});
            skLineSegment(sketch, "E1120", {"start": v(-2.05, -4.46) * mm, "end": v(-2.08, -4.5) * mm});
            skLineSegment(sketch, "E1121", {"start": v(-2.08, -4.5) * mm, "end": v(-2.11, -4.54) * mm});
            skLineSegment(sketch, "E1122", {"start": v(-2.11, -4.54) * mm, "end": v(-2.15, -4.59) * mm});
            skLineSegment(sketch, "E1123", {"start": v(-2.15, -4.59) * mm, "end": v(-2.2, -4.65) * mm});
            skLineSegment(sketch, "E1124", {"start": v(-2.2, -4.65) * mm, "end": v(-2.28, -4.7) * mm});
            skLineSegment(sketch, "E1125", {"start": v(-2.28, -4.7) * mm, "end": v(-2.36, -4.78) * mm});
            skLineSegment(sketch, "E1126", {"start": v(-2.36, -4.78) * mm, "end": v(-2.45, -4.85) * mm});
            skLineSegment(sketch, "E1127", {"start": v(-2.45, -4.85) * mm, "end": v(-2.55, -4.92) * mm});
            skLineSegment(sketch, "E1128", {"start": v(-2.55, -4.92) * mm, "end": v(-2.67, -5) * mm});
            skLineSegment(sketch, "E1129", {"start": v(-2.67, -5) * mm, "end": v(-2.8, -5.07) * mm});
            skLineSegment(sketch, "E1130", {"start": v(-2.8, -5.07) * mm, "end": v(-2.95, -5.14) * mm});
            skLineSegment(sketch, "E1131", {"start": v(-2.95, -5.14) * mm, "end": v(-3, -5.16) * mm});
            skArc(sketch, "E1132", {"start": v(-3, -5.16) * mm, "mid": v(-3.2, -5.03) * mm, "end": v(-3.42, -4.89) * mm});
            skLineSegment(sketch, "E1133", {"start": v(-3.42, -4.89) * mm, "end": v(-3.42, -4.84) * mm});
            skLineSegment(sketch, "E1134", {"start": v(-3.42, -4.84) * mm, "end": v(-3.41, -4.68) * mm});
            skLineSegment(sketch, "E1135", {"start": v(-3.41, -4.68) * mm, "end": v(-3.4, -4.53) * mm});
            skLineSegment(sketch, "E1136", {"start": v(-3.4, -4.53) * mm, "end": v(-3.38, -4.39) * mm});
            skLineSegment(sketch, "E1137", {"start": v(-3.38, -4.39) * mm, "end": v(-3.36, -4.26) * mm});
            skLineSegment(sketch, "E1138", {"start": v(-3.36, -4.26) * mm, "end": v(-3.33, -4.15) * mm});
            skLineSegment(sketch, "E1139", {"start": v(-3.33, -4.15) * mm, "end": v(-3.3, -4.05) * mm});
            skLineSegment(sketch, "E1140", {"start": v(-3.3, -4.05) * mm, "end": v(-3.27, -3.96) * mm});
            skLineSegment(sketch, "E1141", {"start": v(-3.27, -3.96) * mm, "end": v(-3.24, -3.89) * mm});
            skLineSegment(sketch, "E1142", {"start": v(-3.24, -3.89) * mm, "end": v(-3.22, -3.83) * mm});
            skLineSegment(sketch, "E1143", {"start": v(-3.22, -3.83) * mm, "end": v(-3.19, -3.78) * mm});
            skLineSegment(sketch, "E1144", {"start": v(-3.19, -3.78) * mm, "end": v(-3.17, -3.74) * mm});
            skLineSegment(sketch, "E1145", {"start": v(-3.17, -3.74) * mm, "end": v(-3.15, -3.72) * mm});
            skLineSegment(sketch, "E1146", {"start": v(-3.15, -3.72) * mm, "end": v(-3.14, -3.7) * mm});
            skLineSegment(sketch, "E1147", {"start": v(-3.14, -3.7) * mm, "end": v(-3.14, -3.7) * mm});
            skLineSegment(sketch, "E1148", {"start": v(-3.14, -3.7) * mm, "end": v(-2.74, -3.23) * mm});
            skArc(sketch, "E1149", {"start": v(-2.74, -3.23) * mm, "mid": v(-3.07, -2.92) * mm, "end": v(-3.36, -2.57) * mm});
            skLineSegment(sketch, "E1150", {"start": v(-3.36, -2.57) * mm, "end": v(-3.85, -2.95) * mm});
            skLineSegment(sketch, "E1151", {"start": v(-3.85, -2.95) * mm, "end": v(-3.85, -2.95) * mm});
            skLineSegment(sketch, "E1152", {"start": v(-3.85, -2.95) * mm, "end": v(-3.87, -2.96) * mm});
            skLineSegment(sketch, "E1153", {"start": v(-3.87, -2.96) * mm, "end": v(-3.9, -2.97) * mm});
            skLineSegment(sketch, "E1154", {"start": v(-3.9, -2.97) * mm, "end": v(-3.93, -3) * mm});
            skLineSegment(sketch, "E1155", {"start": v(-3.93, -3) * mm, "end": v(-3.98, -3.02) * mm});
            skLineSegment(sketch, "E1156", {"start": v(-3.98, -3.02) * mm, "end": v(-4.04, -3.04) * mm});
            skLineSegment(sketch, "E1157", {"start": v(-4.04, -3.04) * mm, "end": v(-4.12, -3.07) * mm});
            skLineSegment(sketch, "E1158", {"start": v(-4.12, -3.07) * mm, "end": v(-4.2, -3.1) * mm});
            skLineSegment(sketch, "E1159", {"start": v(-4.2, -3.1) * mm, "end": v(-4.3, -3.11) * mm});
            skLineSegment(sketch, "E1160", {"start": v(-4.3, -3.11) * mm, "end": v(-4.42, -3.13) * mm});
            skLineSegment(sketch, "E1161", {"start": v(-4.42, -3.13) * mm, "end": v(-4.55, -3.15) * mm});
            skLineSegment(sketch, "E1162", {"start": v(-4.55, -3.15) * mm, "end": v(-4.69, -3.16) * mm});
            skLineSegment(sketch, "E1163", {"start": v(-4.69, -3.16) * mm, "end": v(-4.84, -3.17) * mm});
            skLineSegment(sketch, "E1164", {"start": v(-4.84, -3.17) * mm, "end": v(-5, -3.16) * mm});
            skLineSegment(sketch, "E1165", {"start": v(-5, -3.16) * mm, "end": v(-5.05, -3.16) * mm});
            skArc(sketch, "E1166", {"start": v(-5.05, -3.16) * mm, "mid": v(-5.18, -2.94) * mm, "end": v(-5.3, -2.72) * mm});
            skLineSegment(sketch, "E1167", {"start": v(-5.3, -2.72) * mm, "end": v(-5.28, -2.68) * mm});
            skLineSegment(sketch, "E1168", {"start": v(-5.28, -2.68) * mm, "end": v(-5.2, -2.53) * mm});
            skLineSegment(sketch, "E1169", {"start": v(-5.2, -2.53) * mm, "end": v(-5.12, -2.4) * mm});
            skLineSegment(sketch, "E1170", {"start": v(-5.12, -2.4) * mm, "end": v(-5.04, -2.3) * mm});
            skLineSegment(sketch, "E1171", {"start": v(-5.04, -2.3) * mm, "end": v(-4.96, -2.2) * mm});
            skLineSegment(sketch, "E1172", {"start": v(-4.96, -2.2) * mm, "end": v(-4.88, -2.1) * mm});
            skLineSegment(sketch, "E1173", {"start": v(-4.88, -2.1) * mm, "end": v(-4.8, -2.03) * mm});
            skLineSegment(sketch, "E1174", {"start": v(-4.8, -2.03) * mm, "end": v(-4.74, -1.97) * mm});
            skLineSegment(sketch, "E1175", {"start": v(-4.74, -1.97) * mm, "end": v(-4.68, -1.91) * mm});
            skLineSegment(sketch, "E1176", {"start": v(-4.68, -1.91) * mm, "end": v(-4.63, -1.87) * mm});
            skLineSegment(sketch, "E1177", {"start": v(-4.63, -1.87) * mm, "end": v(-4.58, -1.84) * mm});
            skLineSegment(sketch, "E1178", {"start": v(-4.58, -1.84) * mm, "end": v(-4.55, -1.82) * mm});
            skLineSegment(sketch, "E1179", {"start": v(-4.55, -1.82) * mm, "end": v(-4.52, -1.8) * mm});
            skLineSegment(sketch, "E1180", {"start": v(-4.52, -1.8) * mm, "end": v(-4.5, -1.8) * mm});
            skLineSegment(sketch, "E1181", {"start": v(-4.5, -1.8) * mm, "end": v(-4.5, -1.8) * mm});
            skLineSegment(sketch, "E1182", {"start": v(-4.5, -1.8) * mm, "end": v(-3.93, -1.57) * mm});
            skArc(sketch, "E1183", {"start": v(-3.93, -1.57) * mm, "mid": v(-4.07, -1.14) * mm, "end": v(-4.17, -0.7) * mm});
            skLineSegment(sketch, "E1184", {"start": v(-4.17, -0.7) * mm, "end": v(-4.78, -0.8) * mm});
            skLineSegment(sketch, "E1185", {"start": v(-4.78, -0.8) * mm, "end": v(-4.78, -0.8) * mm});
            skLineSegment(sketch, "E1186", {"start": v(-4.78, -0.8) * mm, "end": v(-4.8, -0.8) * mm});
            skLineSegment(sketch, "E1187", {"start": v(-4.8, -0.8) * mm, "end": v(-4.83, -0.8) * mm});
            skLineSegment(sketch, "E1188", {"start": v(-4.83, -0.8) * mm, "end": v(-4.87, -0.8) * mm});
            skLineSegment(sketch, "E1189", {"start": v(-4.87, -0.8) * mm, "end": v(-4.93, -0.8) * mm});
            skLineSegment(sketch, "E1190", {"start": v(-4.93, -0.8) * mm, "end": v(-5, -0.8) * mm});
            skLineSegment(sketch, "E1191", {"start": v(-5, -0.8) * mm, "end": v(-5.07, -0.78) * mm});
            skLineSegment(sketch, "E1192", {"start": v(-5.07, -0.78) * mm, "end": v(-5.16, -0.76) * mm});
            skLineSegment(sketch, "E1193", {"start": v(-5.16, -0.76) * mm, "end": v(-5.26, -0.73) * mm});
            skLineSegment(sketch, "E1194", {"start": v(-5.26, -0.73) * mm, "end": v(-5.37, -0.7) * mm});
            skLineSegment(sketch, "E1195", {"start": v(-5.37, -0.7) * mm, "end": v(-5.5, -0.65) * mm});
            skLineSegment(sketch, "E1196", {"start": v(-5.5, -0.65) * mm, "end": v(-5.62, -0.6) * mm});
            skLineSegment(sketch, "E1197", {"start": v(-5.62, -0.6) * mm, "end": v(-5.76, -0.53) * mm});
            skLineSegment(sketch, "E1198", {"start": v(-5.76, -0.53) * mm, "end": v(-5.9, -0.45) * mm});
            skLineSegment(sketch, "E1199", {"start": v(-5.9, -0.45) * mm, "end": v(-5.94, -0.43) * mm});
            skArc(sketch, "E1200", {"start": v(-5.94, -0.43) * mm, "mid": v(-5.95, -0.17) * mm, "end": v(-5.96, 0.08) * mm});
            skLineSegment(sketch, "E1201", {"start": v(-5.96, 0.08) * mm, "end": v(-5.92, 0.1) * mm});
            skLineSegment(sketch, "E1202", {"start": v(-5.92, 0.1) * mm, "end": v(-5.78, 0.2) * mm});
            skLineSegment(sketch, "E1203", {"start": v(-5.78, 0.2) * mm, "end": v(-5.65, 0.27) * mm});
            skLineSegment(sketch, "E1204", {"start": v(-5.65, 0.27) * mm, "end": v(-5.53, 0.33) * mm});
            skLineSegment(sketch, "E1205", {"start": v(-5.53, 0.33) * mm, "end": v(-5.4, 0.39) * mm});
            skLineSegment(sketch, "E1206", {"start": v(-5.4, 0.39) * mm, "end": v(-5.3, 0.43) * mm});
            skLineSegment(sketch, "E1207", {"start": v(-5.3, 0.43) * mm, "end": v(-5.2, 0.46) * mm});
            skLineSegment(sketch, "E1208", {"start": v(-5.2, 0.46) * mm, "end": v(-5.11, 0.48) * mm});
            skLineSegment(sketch, "E1209", {"start": v(-5.11, 0.48) * mm, "end": v(-5.04, 0.5) * mm});
            skLineSegment(sketch, "E1210", {"start": v(-5.04, 0.5) * mm, "end": v(-4.97, 0.51) * mm});
            skLineSegment(sketch, "E1211", {"start": v(-4.97, 0.51) * mm, "end": v(-4.92, 0.52) * mm});
            skLineSegment(sketch, "E1212", {"start": v(-4.92, 0.52) * mm, "end": v(-4.87, 0.52) * mm});
            skLineSegment(sketch, "E1213", {"start": v(-4.87, 0.52) * mm, "end": v(-4.84, 0.52) * mm});
            skLineSegment(sketch, "E1214", {"start": v(-4.84, 0.52) * mm, "end": v(-4.82, 0.52) * mm});
            skLineSegment(sketch, "E1215", {"start": v(-4.82, 0.52) * mm, "end": v(-4.82, 0.52) * mm});
            skLineSegment(sketch, "E1216", {"start": v(-4.82, 0.52) * mm, "end": v(-4.2, 0.46) * mm});
            skArc(sketch, "E1217", {"start": v(-4.2, 0.46) * mm, "mid": v(-4.14, 0.9) * mm, "end": v(-4.02, 1.34) * mm});
            skLineSegment(sketch, "E1218", {"start": v(-4.02, 1.34) * mm, "end": v(-4.6, 1.53) * mm});
            skLineSegment(sketch, "E1219", {"start": v(-4.6, 1.53) * mm, "end": v(-4.6, 1.53) * mm});
            skLineSegment(sketch, "E1220", {"start": v(-4.6, 1.53) * mm, "end": v(-4.63, 1.54) * mm});
            skLineSegment(sketch, "E1221", {"start": v(-4.63, 1.54) * mm, "end": v(-4.65, 1.55) * mm});
            skLineSegment(sketch, "E1222", {"start": v(-4.65, 1.55) * mm, "end": v(-4.7, 1.58) * mm});
            skLineSegment(sketch, "E1223", {"start": v(-4.7, 1.58) * mm, "end": v(-4.74, 1.6) * mm});
            skLineSegment(sketch, "E1224", {"start": v(-4.74, 1.6) * mm, "end": v(-4.8, 1.64) * mm});
            skLineSegment(sketch, "E1225", {"start": v(-4.8, 1.64) * mm, "end": v(-4.86, 1.69) * mm});
            skLineSegment(sketch, "E1226", {"start": v(-4.86, 1.69) * mm, "end": v(-4.93, 1.75) * mm});
            skLineSegment(sketch, "E1227", {"start": v(-4.93, 1.75) * mm, "end": v(-5, 1.82) * mm});
            skLineSegment(sketch, "E1228", {"start": v(-5, 1.82) * mm, "end": v(-5.09, 1.9) * mm});
            skLineSegment(sketch, "E1229", {"start": v(-5.09, 1.9) * mm, "end": v(-5.17, 2) * mm});
            skLineSegment(sketch, "E1230", {"start": v(-5.17, 2) * mm, "end": v(-5.26, 2.1) * mm});
            skLineSegment(sketch, "E1231", {"start": v(-5.26, 2.1) * mm, "end": v(-5.35, 2.23) * mm});
            skLineSegment(sketch, "E1232", {"start": v(-5.35, 2.23) * mm, "end": v(-5.44, 2.37) * mm});
            skLineSegment(sketch, "E1233", {"start": v(-5.44, 2.37) * mm, "end": v(-5.46, 2.4) * mm});
            skArc(sketch, "E1234", {"start": v(-5.46, 2.4) * mm, "mid": v(-5.36, 2.63) * mm, "end": v(-5.24, 2.86) * mm});
            skLineSegment(sketch, "E1235", {"start": v(-5.24, 2.86) * mm, "end": v(-5.2, 2.87) * mm});
            skLineSegment(sketch, "E1236", {"start": v(-5.2, 2.87) * mm, "end": v(-5.03, 2.88) * mm});
            skLineSegment(sketch, "E1237", {"start": v(-5.03, 2.88) * mm, "end": v(-4.88, 2.89) * mm});
            skLineSegment(sketch, "E1238", {"start": v(-4.88, 2.89) * mm, "end": v(-4.74, 2.88) * mm});
            skLineSegment(sketch, "E1239", {"start": v(-4.74, 2.88) * mm, "end": v(-4.61, 2.88) * mm});
            skLineSegment(sketch, "E1240", {"start": v(-4.61, 2.88) * mm, "end": v(-4.5, 2.86) * mm});
            skLineSegment(sketch, "E1241", {"start": v(-4.5, 2.86) * mm, "end": v(-4.4, 2.85) * mm});
            skLineSegment(sketch, "E1242", {"start": v(-4.4, 2.85) * mm, "end": v(-4.3, 2.83) * mm});
            skLineSegment(sketch, "E1243", {"start": v(-4.3, 2.83) * mm, "end": v(-4.23, 2.8) * mm});
            skLineSegment(sketch, "E1244", {"start": v(-4.23, 2.8) * mm, "end": v(-4.16, 2.79) * mm});
            skLineSegment(sketch, "E1245", {"start": v(-4.16, 2.79) * mm, "end": v(-4.11, 2.77) * mm});
            skLineSegment(sketch, "E1246", {"start": v(-4.11, 2.77) * mm, "end": v(-4.07, 2.75) * mm});
            skLineSegment(sketch, "E1247", {"start": v(-4.07, 2.75) * mm, "end": v(-4.05, 2.74) * mm});
            skLineSegment(sketch, "E1248", {"start": v(-4.05, 2.74) * mm, "end": v(-4.03, 2.73) * mm});
            skLineSegment(sketch, "E1249", {"start": v(-4.03, 2.73) * mm, "end": v(-4.02, 2.72) * mm});
            skLineSegment(sketch, "E1250", {"start": v(-4.02, 2.72) * mm, "end": v(-3.52, 2.38) * mm});
            skArc(sketch, "E1251", {"start": v(-3.52, 2.38) * mm, "mid": v(-3.25, 2.75) * mm, "end": v(-2.94, 3.08) * mm});
            skLineSegment(sketch, "E1252", {"start": v(-2.94, 3.08) * mm, "end": v(-3.37, 3.52) * mm});
            skLineSegment(sketch, "E1253", {"start": v(-3.37, 3.52) * mm, "end": v(-3.37, 3.52) * mm});
            skLineSegment(sketch, "E1254", {"start": v(-3.37, 3.52) * mm, "end": v(-3.38, 3.54) * mm});
            skLineSegment(sketch, "E1255", {"start": v(-3.38, 3.54) * mm, "end": v(-3.4, 3.56) * mm});
            skLineSegment(sketch, "E1256", {"start": v(-3.4, 3.56) * mm, "end": v(-3.42, 3.6) * mm});
            skLineSegment(sketch, "E1257", {"start": v(-3.42, 3.6) * mm, "end": v(-3.45, 3.64) * mm});
            skLineSegment(sketch, "E1258", {"start": v(-3.45, 3.64) * mm, "end": v(-3.48, 3.7) * mm});
            skLineSegment(sketch, "E1259", {"start": v(-3.48, 3.7) * mm, "end": v(-3.52, 3.77) * mm});
            skLineSegment(sketch, "E1260", {"start": v(-3.52, 3.77) * mm, "end": v(-3.55, 3.86) * mm});
            skLineSegment(sketch, "E1261", {"start": v(-3.55, 3.86) * mm, "end": v(-3.59, 3.96) * mm});
            skLineSegment(sketch, "E1262", {"start": v(-3.59, 3.96) * mm, "end": v(-3.62, 4.07) * mm});
            skLineSegment(sketch, "E1263", {"start": v(-3.62, 4.07) * mm, "end": v(-3.65, 4.2) * mm});
            skLineSegment(sketch, "E1264", {"start": v(-3.65, 4.2) * mm, "end": v(-3.68, 4.33) * mm});
            skLineSegment(sketch, "E1265", {"start": v(-3.68, 4.33) * mm, "end": v(-3.7, 4.48) * mm});
            skLineSegment(sketch, "E1266", {"start": v(-3.7, 4.48) * mm, "end": v(-3.72, 4.64) * mm});
            skLineSegment(sketch, "E1267", {"start": v(-3.72, 4.64) * mm, "end": v(-3.72, 4.69) * mm});
            skArc(sketch, "E1268", {"start": v(-3.72, 4.69) * mm, "mid": v(-3.52, 4.84) * mm, "end": v(-3.31, 4.99) * mm});
            skLineSegment(sketch, "E1269", {"start": v(-3.31, 4.99) * mm, "end": v(-3.27, 4.97) * mm});
            skLineSegment(sketch, "E1270", {"start": v(-3.27, 4.97) * mm, "end": v(-3.12, 4.91) * mm});
            skLineSegment(sketch, "E1271", {"start": v(-3.12, 4.91) * mm, "end": v(-2.98, 4.84) * mm});
            skLineSegment(sketch, "E1272", {"start": v(-2.98, 4.84) * mm, "end": v(-2.86, 4.78) * mm});
            skLineSegment(sketch, "E1273", {"start": v(-2.86, 4.78) * mm, "end": v(-2.75, 4.71) * mm});
            skLineSegment(sketch, "E1274", {"start": v(-2.75, 4.71) * mm, "end": v(-2.65, 4.65) * mm});
            skLineSegment(sketch, "E1275", {"start": v(-2.65, 4.65) * mm, "end": v(-2.57, 4.58) * mm});
            skLineSegment(sketch, "E1276", {"start": v(-2.57, 4.58) * mm, "end": v(-2.5, 4.52) * mm});
            skLineSegment(sketch, "E1277", {"start": v(-2.5, 4.52) * mm, "end": v(-2.44, 4.47) * mm});
            skLineSegment(sketch, "E1278", {"start": v(-2.44, 4.47) * mm, "end": v(-2.4, 4.42) * mm});
            skLineSegment(sketch, "E1279", {"start": v(-2.4, 4.42) * mm, "end": v(-2.36, 4.38) * mm});
            skLineSegment(sketch, "E1280", {"start": v(-2.36, 4.38) * mm, "end": v(-2.33, 4.35) * mm});
            skLineSegment(sketch, "E1281", {"start": v(-2.33, 4.35) * mm, "end": v(-2.31, 4.32) * mm});
            skLineSegment(sketch, "E1282", {"start": v(-2.31, 4.32) * mm, "end": v(-2.3, 4.3) * mm});
            skLineSegment(sketch, "E1283", {"start": v(-2.3, 4.3) * mm, "end": v(-2.3, 4.3) * mm});
            skLineSegment(sketch, "E1284", {"start": v(-2.3, 4.3) * mm, "end": v(-2, 3.77) * mm});
            skArc(sketch, "E1285", {"start": v(-2, 3.77) * mm, "mid": v(-1.6, 3.96) * mm, "end": v(-1.17, 4.11) * mm});
            skLineSegment(sketch, "E1286", {"start": v(-1.17, 4.11) * mm, "end": v(-1.35, 4.7) * mm});
            skLineSegment(sketch, "E1287", {"start": v(-1.35, 4.7) * mm, "end": v(-1.35, 4.7) * mm});
            skLineSegment(sketch, "E1288", {"start": v(-1.35, 4.7) * mm, "end": v(-1.35, 4.72) * mm});
            skLineSegment(sketch, "E1289", {"start": v(-1.35, 4.72) * mm, "end": v(-1.36, 4.75) * mm});
            skLineSegment(sketch, "E1290", {"start": v(-1.36, 4.75) * mm, "end": v(-1.36, 4.8) * mm});
            skLineSegment(sketch, "E1291", {"start": v(-1.36, 4.8) * mm, "end": v(-1.37, 4.85) * mm});
            skLineSegment(sketch, "E1292", {"start": v(-1.37, 4.85) * mm, "end": v(-1.37, 4.92) * mm});
            skLineSegment(sketch, "E1293", {"start": v(-1.37, 4.92) * mm, "end": v(-1.36, 5) * mm});
            skLineSegment(sketch, "E1294", {"start": v(-1.36, 5) * mm, "end": v(-1.36, 5.09) * mm});
            skLineSegment(sketch, "E1295", {"start": v(-1.36, 5.09) * mm, "end": v(-1.34, 5.2) * mm});
            skLineSegment(sketch, "E1296", {"start": v(-1.34, 5.2) * mm, "end": v(-1.32, 5.3) * mm});
            skLineSegment(sketch, "E1297", {"start": v(-1.32, 5.3) * mm, "end": v(-1.29, 5.43) * mm});
            skLineSegment(sketch, "E1298", {"start": v(-1.29, 5.43) * mm, "end": v(-1.25, 5.56) * mm});
            skLineSegment(sketch, "E1299", {"start": v(-1.25, 5.56) * mm, "end": v(-1.2, 5.7) * mm});
            skLineSegment(sketch, "E1300", {"start": v(-1.2, 5.7) * mm, "end": v(-1.14, 5.86) * mm});
            skLineSegment(sketch, "E1301", {"start": v(-1.14, 5.86) * mm, "end": v(-1.12, 5.9) * mm});
            skArc(sketch, "E1302", {"start": v(-1.12, 5.9) * mm, "mid": v(-0.87, 5.95) * mm, "end": v(-0.62, 5.98) * mm});
            skLineSegment(sketch, "E1303", {"start": v(-0.62, 5.98) * mm, "end": v(-0.59, 5.95) * mm});
            skLineSegment(sketch, "E1304", {"start": v(-0.59, 5.95) * mm, "end": v(-0.48, 5.82) * mm});
            skLineSegment(sketch, "E1305", {"start": v(-0.48, 5.82) * mm, "end": v(-0.4, 5.7) * mm});
            skLineSegment(sketch, "E1306", {"start": v(-0.4, 5.7) * mm, "end": v(-0.31, 5.58) * mm});
            skLineSegment(sketch, "E1307", {"start": v(-0.31, 5.58) * mm, "end": v(-0.25, 5.47) * mm});
            skLineSegment(sketch, "E1308", {"start": v(-0.25, 5.47) * mm, "end": v(-0.2, 5.37) * mm});
            skLineSegment(sketch, "E1309", {"start": v(-0.2, 5.37) * mm, "end": v(-0.15, 5.27) * mm});
            skLineSegment(sketch, "E1310", {"start": v(-0.15, 5.27) * mm, "end": v(-0.11, 5.19) * mm});
            skLineSegment(sketch, "E1311", {"start": v(-0.11, 5.19) * mm, "end": v(-0.09, 5.11) * mm});
            skLineSegment(sketch, "E1312", {"start": v(-0.09, 5.11) * mm, "end": v(-0.07, 5.05) * mm});
            skLineSegment(sketch, "E1313", {"start": v(-0.07, 5.05) * mm, "end": v(-0.05, 5) * mm});
            skLineSegment(sketch, "E1314", {"start": v(-0.05, 5) * mm, "end": v(-0.05, 4.96) * mm});
            skLineSegment(sketch, "E1315", {"start": v(-0.05, 4.96) * mm, "end": v(-0.04, 4.92) * mm});
            skLineSegment(sketch, "E1316", {"start": v(-0.04, 4.92) * mm, "end": v(-0.04, 4.9) * mm});
            skLineSegment(sketch, "E1317", {"start": v(-0.04, 4.9) * mm, "end": v(-0.04, 4.9) * mm});
            skLineSegment(sketch, "E1318", {"start": v(-0.04, 4.9) * mm, "end": v(-0.03, 4.29) * mm});
            skArc(sketch, "E1319", {"start": v(-0.03, 4.29) * mm, "mid": v(0.42, 4.27) * mm, "end": v(0.87, 4.2) * mm});
            skLineSegment(sketch, "E1320", {"start": v(0.87, 4.2) * mm, "end": v(0.99, 4.8) * mm});
            skLineSegment(sketch, "E1321", {"start": v(0.99, 4.8) * mm, "end": v(1, 4.81) * mm});
            skLineSegment(sketch, "E1322", {"start": v(1, 4.81) * mm, "end": v(1, 4.83) * mm});
            skLineSegment(sketch, "E1323", {"start": v(1, 4.83) * mm, "end": v(1, 4.86) * mm});
            skLineSegment(sketch, "E1324", {"start": v(1, 4.86) * mm, "end": v(1.02, 4.9) * mm});
            skLineSegment(sketch, "E1325", {"start": v(1.02, 4.9) * mm, "end": v(1.04, 4.95) * mm});
            skLineSegment(sketch, "E1326", {"start": v(1.04, 4.95) * mm, "end": v(1.07, 5.01) * mm});
            skLineSegment(sketch, "E1327", {"start": v(1.07, 5.01) * mm, "end": v(1.11, 5.08) * mm});
            skLineSegment(sketch, "E1328", {"start": v(1.11, 5.08) * mm, "end": v(1.16, 5.16) * mm});
            skLineSegment(sketch, "E1329", {"start": v(1.16, 5.16) * mm, "end": v(1.22, 5.24) * mm});
            skLineSegment(sketch, "E1330", {"start": v(1.22, 5.24) * mm, "end": v(1.3, 5.33) * mm});
            skLineSegment(sketch, "E1331", {"start": v(1.3, 5.33) * mm, "end": v(1.38, 5.43) * mm});
            skLineSegment(sketch, "E1332", {"start": v(1.38, 5.43) * mm, "end": v(1.48, 5.53) * mm});
            skLineSegment(sketch, "E1333", {"start": v(1.48, 5.53) * mm, "end": v(1.59, 5.63) * mm});
            skLineSegment(sketch, "E1334", {"start": v(1.59, 5.63) * mm, "end": v(1.72, 5.74) * mm});
            skLineSegment(sketch, "E1335", {"start": v(1.72, 5.74) * mm, "end": v(1.75, 5.77) * mm});
            skArc(sketch, "E1336", {"start": v(1.75, 5.77) * mm, "mid": v(2, 5.69) * mm, "end": v(2.23, 5.6) * mm});
            skLineSegment(sketch, "E1337", {"start": v(2.23, 5.6) * mm, "end": v(2.24, 5.56) * mm});
            skLineSegment(sketch, "E1338", {"start": v(2.24, 5.56) * mm, "end": v(2.27, 5.4) * mm});
            skLineSegment(sketch, "E1339", {"start": v(2.27, 5.4) * mm, "end": v(2.3, 5.25) * mm});
            skLineSegment(sketch, "E1340", {"start": v(2.3, 5.25) * mm, "end": v(2.31, 5.1) * mm});
            skLineSegment(sketch, "E1341", {"start": v(2.31, 5.1) * mm, "end": v(2.32, 4.98) * mm});
            skLineSegment(sketch, "E1342", {"start": v(2.32, 4.98) * mm, "end": v(2.32, 4.86) * mm});
            skLineSegment(sketch, "E1343", {"start": v(2.32, 4.86) * mm, "end": v(2.32, 4.76) * mm});
            skLineSegment(sketch, "E1344", {"start": v(2.32, 4.76) * mm, "end": v(2.3, 4.67) * mm});
            skLineSegment(sketch, "E1345", {"start": v(2.3, 4.67) * mm, "end": v(2.3, 4.6) * mm});
            skLineSegment(sketch, "E1346", {"start": v(2.3, 4.6) * mm, "end": v(2.29, 4.52) * mm});
            skLineSegment(sketch, "E1347", {"start": v(2.29, 4.52) * mm, "end": v(2.27, 4.47) * mm});
            skLineSegment(sketch, "E1348", {"start": v(2.27, 4.47) * mm, "end": v(2.26, 4.43) * mm});
            skLineSegment(sketch, "E1349", {"start": v(2.26, 4.43) * mm, "end": v(2.25, 4.4) * mm});
            skLineSegment(sketch, "E1350", {"start": v(2.25, 4.4) * mm, "end": v(2.24, 4.38) * mm});
            skLineSegment(sketch, "E1351", {"start": v(2.24, 4.38) * mm, "end": v(2.24, 4.38) * mm});
            skLineSegment(sketch, "E1352", {"start": v(2.24, 4.38) * mm, "end": v(1.97, 3.83) * mm});
            skArc(sketch, "E1353", {"start": v(1.97, 3.83) * mm, "mid": v(2.36, 3.6) * mm, "end": v(2.72, 3.34) * mm});
            skSolve(sketch);
        }
        {
            var Q0;
            Q0 = qSketchRegion(id + "F2", true);
            extrude(context, id + "F3", {"entities" : qUnion([Q0]), "depth" : (getVariable(context, 'Gear1')) * mm});
        }
        {
            var Q0;
            Q0 = qSketchRegion(id + "F1", true);
            extrude(context, id + "F4", {"entities" : qUnion([Q0]), "operationType" : NewBodyOperationType.ADD, "depth" : 6 * mm});
        }
        {
            var Q0;
            {var subQ0=sQuery(id+"F1.wireOp",EDGE,"E378");var subQ1=sQuery(id+"F1.wireOp",EDGE,"E374");var subQ2=sQuery(id+"F1.wireOp",EDGE,"E572");var subQ3=sQuery(id+"F1.wireOp",EDGE,"E370");var subQ4=sQuery(id+"F1.wireOp",EDGE,"E366");var subQ5=sQuery(id+"F1.wireOp",EDGE,"E363");var subQ6=sQuery(id+"F1.wireOp",EDGE,"E359");var subQ7=sQuery(id+"F1.wireOp",EDGE,"E557");var subQ8=sQuery(id+"F1.wireOp",EDGE,"E358");var subQ9=sQuery(id+"F1.wireOp",EDGE,"E556");var subQ10=sQuery(id+"F1.wireOp",EDGE,"E356");var subQ11=sQuery(id+"F1.wireOp",EDGE,"E355");var subQ12=sQuery(id+"F1.wireOp",EDGE,"E354");var subQ13=sQuery(id+"F1.wireOp",EDGE,"E352");var subQ14=sQuery(id+"F1.wireOp",EDGE,"E350");var subQ15=sQuery(id+"F1.wireOp",EDGE,"E344");var subQ16=sQuery(id+"F1.wireOp",EDGE,"E340");var subQ17=sQuery(id+"F1.wireOp",EDGE,"E336");var subQ18=sQuery(id+"F1.wireOp",EDGE,"E334");var subQ19=sQuery(id+"F1.wireOp",EDGE,"E328");var subQ20=sQuery(id+"F1.wireOp",EDGE,"E324");var subQ21=sQuery(id+"F1.wireOp",EDGE,"E379");var subQ22=sQuery(id+"F1.wireOp",EDGE,"E322");var subQ23=sQuery(id+"F1.wireOp",EDGE,"E321");var subQ24=sQuery(id+"F1.wireOp",EDGE,"E318");var subQ25=sQuery(id+"F1.wireOp",EDGE,"E314");var subQ26=sQuery(id+"F1.wireOp",EDGE,"E310");var subQ27=sQuery(id+"F1.wireOp",EDGE,"E306");var subQ28=sQuery(id+"F1.wireOp",EDGE,"E305");var subQ29=sQuery(id+"F1.wireOp",EDGE,"E297");var subQ30=sQuery(id+"F1.wireOp",EDGE,"E294");var subQ31=sQuery(id+"F1.wireOp",EDGE,"E349");var subQ32=sQuery(id+"F1.wireOp",EDGE,"E292");var subQ33=sQuery(id+"F1.wireOp",EDGE,"E291");var subQ34=sQuery(id+"F1.wireOp",EDGE,"E288");var subQ35=sQuery(id+"F1.wireOp",EDGE,"E284");var subQ36=sQuery(id+"F1.wireOp",EDGE,"E275");var subQ37=sQuery(id+"F1.wireOp",EDGE,"E272");var subQ38=sQuery(id+"F1.wireOp",EDGE,"E269");var subQ39=sQuery(id+"F1.wireOp",EDGE,"E267");var subQ40=sQuery(id+"F1.wireOp",EDGE,"E266");var subQ41=sQuery(id+"F1.wireOp",EDGE,"E263");var subQ42=sQuery(id+"F1.wireOp",EDGE,"E262");var subQ43=sQuery(id+"F1.wireOp",EDGE,"E368");var subQ44=sQuery(id+"F1.wireOp",EDGE,"E261");var subQ45=sQuery(id+"F1.wireOp",EDGE,"E258");var subQ46=sQuery(id+"F1.wireOp",EDGE,"E254");var subQ47=sQuery(id+"F1.wireOp",EDGE,"E245");var subQ48=sQuery(id+"F1.wireOp",EDGE,"E242");var subQ49=sQuery(id+"F1.wireOp",EDGE,"E240");var subQ50=sQuery(id+"F1.wireOp",EDGE,"E239");var subQ51=sQuery(id+"F1.wireOp",EDGE,"E377");var subQ52=sQuery(id+"F1.wireOp",EDGE,"E238");var subQ53=sQuery(id+"F1.wireOp",EDGE,"E436");var subQ54=sQuery(id+"F1.wireOp",EDGE,"E236");var subQ55=sQuery(id+"F1.wireOp",EDGE,"E235");var subQ56=sQuery(id+"F1.wireOp",EDGE,"E232");var subQ57=sQuery(id+"F1.wireOp",EDGE,"E229");var subQ58=sQuery(id+"F1.wireOp",EDGE,"E228");var subQ59=sQuery(id+"F1.wireOp",EDGE,"E227");var subQ60=sQuery(id+"F1.wireOp",EDGE,"E362");var subQ61=sQuery(id+"F1.wireOp",EDGE,"E223");var subQ62=sQuery(id+"F1.wireOp",EDGE,"E421");var subQ63=sQuery(id+"F1.wireOp",EDGE,"E220");var subQ64=sQuery(id+"F1.wireOp",EDGE,"E212");var subQ65=sQuery(id+"F1.wireOp",EDGE,"E211");var subQ66=sQuery(id+"F1.wireOp",EDGE,"E209");var subQ67=sQuery(id+"F1.wireOp",EDGE,"E372");var subQ68=sQuery(id+"F1.wireOp",EDGE,"E347");var subQ69=sQuery(id+"F1.wireOp",EDGE,"E208");var subQ70=sQuery(id+"F1.wireOp",EDGE,"E406");var subQ71=sQuery(id+"F1.wireOp",EDGE,"E205");var subQ72=sQuery(id+"F1.wireOp",EDGE,"E202");var subQ73=sQuery(id+"F1.wireOp",EDGE,"E361");var subQ74=sQuery(id+"F1.wireOp",EDGE,"E163");var subQ75=sQuery(id+"F1.wireOp",EDGE,"E222");var subQ76=sQuery(id+"F1.wireOp",EDGE,"E420");var subQ77=sQuery(id+"F1.wireOp",EDGE,"E197");var subQ78=sQuery(id+"F1.wireOp",EDGE,"E332");var subQ79=sQuery(id+"F1.wireOp",EDGE,"E193");var subQ80=sQuery(id+"F1.wireOp",EDGE,"E391");var subQ81=sQuery(id+"F1.wireOp",EDGE,"E189");var subQ82=sQuery(id+"F1.wireOp",EDGE,"E182");var subQ83=sQuery(id+"F1.wireOp",EDGE,"E907");var subQ84=sQuery(id+"F1.wireOp",EDGE,"E181");var subQ85=sQuery(id+"F1.wireOp",EDGE,"E906");var subQ86=sQuery(id+"F1.wireOp",EDGE,"E341");var subQ87=sQuery(id+"F1.wireOp",EDGE,"E316");var subQ88=sQuery(id+"F1.wireOp",EDGE,"E118");var subQ89=sQuery(id+"F1.wireOp",EDGE,"E177");var subQ90=sQuery(id+"F1.wireOp",EDGE,"E375");var subQ91=sQuery(id+"F1.wireOp",EDGE,"E315");var subQ92=sQuery(id+"F1.wireOp",EDGE,"E117");var subQ93=sQuery(id+"F1.wireOp",EDGE,"E176");var subQ94=sQuery(id+"F1.wireOp",EDGE,"E175");var subQ95=sQuery(id+"F1.wireOp",EDGE,"E338");var subQ96=sQuery(id+"F1.wireOp",EDGE,"E231");var subQ97=sQuery(id+"F1.wireOp",EDGE,"E174");var subQ98=sQuery(id+"F1.wireOp",EDGE,"E899");var subQ99=sQuery(id+"F1.wireOp",EDGE,"E173");var subQ100=sQuery(id+"F1.wireOp",EDGE,"E172");var subQ101=sQuery(id+"F1.wireOp",EDGE,"E331");var subQ102=sQuery(id+"F1.wireOp",EDGE,"E133");var subQ103=sQuery(id+"F1.wireOp",EDGE,"E192");var subQ104=sQuery(id+"F1.wireOp",EDGE,"E390");var subQ105=sQuery(id+"F1.wireOp",EDGE,"E167");var subQ106=sQuery(id+"F1.wireOp",EDGE,"E892");var subQ107=sQuery(id+"F1.wireOp",EDGE,"E164");var subQ108=sQuery(id+"F1.wireOp",EDGE,"E216");var subQ109=sQuery(id+"F1.wireOp",EDGE,"E159");var subQ110=sQuery(id+"F1.wireOp",EDGE,"E884");var subQ111=sQuery(id+"F1.wireOp",EDGE,"E215");var subQ112=sQuery(id+"F1.wireOp",EDGE,"E158");var subQ113=sQuery(id+"F1.wireOp",EDGE,"E883");var subQ114=sQuery(id+"F1.wireOp",EDGE,"E157");var subQ115=sQuery(id+"F1.wireOp",EDGE,"E151");var subQ116=sQuery(id+"F1.wireOp",EDGE,"E876");var subQ117=sQuery(id+"F1.wireOp",EDGE,"E311");var subQ118=sQuery(id+"F1.wireOp",EDGE,"E147");var subQ119=sQuery(id+"F1.wireOp",EDGE,"E345");var subQ120=sQuery(id+"F1.wireOp",EDGE,"E285");var subQ121=sQuery(id+"F1.wireOp",EDGE,"E87");var subQ122=sQuery(id+"F1.wireOp",EDGE,"E146");var subQ123=sQuery(id+"F1.wireOp",EDGE,"E145");var subQ124=sQuery(id+"F1.wireOp",EDGE,"E365");var subQ125=sQuery(id+"F1.wireOp",EDGE,"E308");var subQ126=sQuery(id+"F1.wireOp",EDGE,"E201");var subQ127=sQuery(id+"F1.wireOp",EDGE,"E367");var subQ128=sQuery(id+"F1.wireOp",EDGE,"E144");var subQ129=sQuery(id+"F1.wireOp",EDGE,"E869");var subQ130=sQuery(id+"F1.wireOp",EDGE,"E199");var subQ131=sQuery(id+"F1.wireOp",EDGE,"E142");var subQ132=sQuery(id+"F1.wireOp",EDGE,"E301");var subQ133=sQuery(id+"F1.wireOp",EDGE,"E103");var subQ134=sQuery(id+"F1.wireOp",EDGE,"E162");var subQ135=sQuery(id+"F1.wireOp",EDGE,"E360");var subQ136=sQuery(id+"F1.wireOp",EDGE,"E137");var subQ137=sQuery(id+"F1.wireOp",EDGE,"E160");var subQ138=sQuery(id+"F1.wireOp",EDGE,"E135");var subQ139=sQuery(id+"F1.wireOp",EDGE,"E134");var subQ140=sQuery(id+"F1.wireOp",EDGE,"E185");var subQ141=sQuery(id+"F1.wireOp",EDGE,"E128");var subQ142=sQuery(id+"F1.wireOp",EDGE,"E853");var subQ143=sQuery(id+"F1.wireOp",EDGE,"E121");var subQ144=sQuery(id+"F1.wireOp",EDGE,"E120");var subQ145=sQuery(id+"F1.wireOp",EDGE,"E119");var subQ146=sQuery(id+"F1.wireOp",EDGE,"E116");var subQ147=sQuery(id+"F1.wireOp",EDGE,"E115");var subQ148=sQuery(id+"F1.wireOp",EDGE,"E278");var subQ149=sQuery(id+"F1.wireOp",EDGE,"E171");var subQ150=sQuery(id+"F1.wireOp",EDGE,"E337");var subQ151=sQuery(id+"F1.wireOp",EDGE,"E114");var subQ152=sQuery(id+"F1.wireOp",EDGE,"E839");var subQ153=sQuery(id+"F1.wireOp",EDGE,"E169");var subQ154=sQuery(id+"F1.wireOp",EDGE,"E112");var subQ155=sQuery(id+"F1.wireOp",EDGE,"E132");var subQ156=sQuery(id+"F1.wireOp",EDGE,"E330");var subQ157=sQuery(id+"F1.wireOp",EDGE,"E107");var subQ158=sQuery(id+"F1.wireOp",EDGE,"E104");var subQ159=sQuery(id+"F1.wireOp",EDGE,"E155");var subQ160=sQuery(id+"F1.wireOp",EDGE,"E98");var subQ161=sQuery(id+"F1.wireOp",EDGE,"E823");var subQ162=sQuery(id+"F1.wireOp",EDGE,"E153");var subQ163=sQuery(id+"F1.wireOp",EDGE,"E96");var subQ164=sQuery(id+"F1.wireOp",EDGE,"E95");var subQ165=sQuery(id+"F1.wireOp",EDGE,"E94");var subQ166=sQuery(id+"F1.wireOp",EDGE,"E92");var subQ167=sQuery(id+"F1.wireOp",EDGE,"E91");var subQ168=sQuery(id+"F1.wireOp",EDGE,"E90");var subQ169=sQuery(id+"F1.wireOp",EDGE,"E89");var subQ170=sQuery(id+"F1.wireOp",EDGE,"E251");var subQ171=sQuery(id+"F1.wireOp",EDGE,"E86");var subQ172=sQuery(id+"F1.wireOp",EDGE,"E85");var subQ173=sQuery(id+"F1.wireOp",EDGE,"E248");var subQ174=sQuery(id+"F1.wireOp",EDGE,"E141");var subQ175=sQuery(id+"F1.wireOp",EDGE,"E307");var subQ176=sQuery(id+"F1.wireOp",EDGE,"E84");var subQ177=sQuery(id+"F1.wireOp",EDGE,"E809");var subQ178=sQuery(id+"F1.wireOp",EDGE,"E139");var subQ179=sQuery(id+"F1.wireOp",EDGE,"E82");var subQ180=sQuery(id+"F1.wireOp",EDGE,"E244");var subQ181=sQuery(id+"F1.wireOp",EDGE,"E80");var subQ182=sQuery(id+"F1.wireOp",EDGE,"E78");var subQ183=sQuery(id+"F1.wireOp",EDGE,"E101");var subQ184=sQuery(id+"F1.wireOp",EDGE,"E76");var subQ185=sQuery(id+"F1.wireOp",EDGE,"E74");var subQ186=sQuery(id+"F1.wireOp",EDGE,"E73");var subQ187=sQuery(id+"F1.wireOp",EDGE,"E71");var subQ188=sQuery(id+"F1.wireOp",EDGE,"E125");var subQ189=sQuery(id+"F1.wireOp",EDGE,"E68");var subQ190=sQuery(id+"F1.wireOp",EDGE,"E793");var subQ191=sQuery(id+"F1.wireOp",EDGE,"E124");var subQ192=sQuery(id+"F1.wireOp",EDGE,"E67");var subQ193=sQuery(id+"F1.wireOp",EDGE,"E123");var subQ194=sQuery(id+"F1.wireOp",EDGE,"E66");var subQ195=sQuery(id+"F1.wireOp",EDGE,"E65");var subQ196=sQuery(id+"F1.wireOp",EDGE,"E62");var subQ197=sQuery(id+"F1.wireOp",EDGE,"E59");var subQ198=sQuery(id+"F1.wireOp",EDGE,"E221");var subQ199=sQuery(id+"F1.wireOp",EDGE,"E57");var subQ200=sQuery(id+"F1.wireOp",EDGE,"E56");var subQ201=sQuery(id+"F1.wireOp",EDGE,"E55");var subQ202=sQuery(id+"F1.wireOp",EDGE,"E218");var subQ203=sQuery(id+"F1.wireOp",EDGE,"E54");var subQ204=sQuery(id+"F1.wireOp",EDGE,"E779");var subQ205=sQuery(id+"F1.wireOp",EDGE,"E217");var subQ206=sQuery(id+"F1.wireOp",EDGE,"E53");var subQ207=sQuery(id+"F1.wireOp",EDGE,"E778");var subQ208=sQuery(id+"F1.wireOp",EDGE,"E213");var subQ209=sQuery(id+"F1.wireOp",EDGE,"E49");var subQ210=sQuery(id+"F1.wireOp",EDGE,"E47");var subQ211=sQuery(id+"F1.wireOp",EDGE,"E210");var subQ212=sQuery(id+"F1.wireOp",EDGE,"E46");var subQ213=sQuery(id+"F1.wireOp",EDGE,"E771");var subQ214=sQuery(id+"F1.wireOp",EDGE,"E70");var subQ215=sQuery(id+"F1.wireOp",EDGE,"E45");var subQ216=sQuery(id+"F1.wireOp",EDGE,"E44");var subQ217=sQuery(id+"F1.wireOp",EDGE,"E43");var subQ218=sQuery(id+"F1.wireOp",EDGE,"E39");var subQ219=sQuery(id+"F1.wireOp",EDGE,"E764");var subQ220=sQuery(id+"F1.wireOp",EDGE,"E38");var subQ221=sQuery(id+"F1.wireOp",EDGE,"E763");var subQ222=sQuery(id+"F1.wireOp",EDGE,"E93");var subQ223=sQuery(id+"F1.wireOp",EDGE,"E36");var subQ224=sQuery(id+"F1.wireOp",EDGE,"E35");var subQ225=sQuery(id+"F1.wireOp",EDGE,"E33");var subQ226=sQuery(id+"F1.wireOp",EDGE,"E32");var subQ227=sQuery(id+"F1.wireOp",EDGE,"E31");var subQ228=sQuery(id+"F1.wireOp",EDGE,"E756");var subQ229=sQuery(id+"F1.wireOp",EDGE,"E29");var subQ230=sQuery(id+"F1.wireOp",EDGE,"E27");var subQ231=sQuery(id+"F1.wireOp",EDGE,"E26");var subQ232=sQuery(id+"F1.wireOp",EDGE,"E25");var subQ233=sQuery(id+"F1.wireOp",EDGE,"E187");var subQ234=sQuery(id+"F1.wireOp",EDGE,"E23");var subQ235=sQuery(id+"F1.wireOp",EDGE,"E748");var subQ236=sQuery(id+"F1.wireOp",EDGE,"E183");var subQ237=sQuery(id+"F1.wireOp",EDGE,"E126");var subQ238=sQuery(id+"F1.wireOp",EDGE,"E19");var subQ239=sQuery(id+"F1.wireOp",EDGE,"E17");var subQ240=sQuery(id+"F1.wireOp",EDGE,"E13");var subQ241=sQuery(id+"F1.wireOp",EDGE,"E9");var subQ242=sQuery(id+"F1.wireOp",EDGE,"E6");var subQ243=sQuery(id+"F1.wireOp",EDGE,"E862");var subQ244=sQuery(id+"F1.wireOp",EDGE,"E5");var subQ245=sQuery(id+"F1.wireOp",EDGE,"E4");var subQ246=sQuery(id+"F1.wireOp",EDGE,"E3");var subQ247=sQuery(id+"F1.wireOp",EDGE,"E1");var subQ248=sQuery(id+"F1.wireOp",EDGE,"E726");var subQ249=sQuery(id+"F1.wireOp",EDGE,"E309");var subQ250=sQuery(id+"F1.wireOp",EDGE,"E313");var subQ251=sQuery(id+"F1.wireOp",EDGE,"E255");var subQ252=sQuery(id+"F1.wireOp",EDGE,"E846");var subQ253=sQuery(id+"F1.wireOp",EDGE,"E280");var subQ254=sQuery(id+"F1.wireOp",EDGE,"E770");var subQ255=sQuery(id+"F1.wireOp",EDGE,"E186");var subQ256=sQuery(id+"F1.wireOp",EDGE,"E129");var subQ257=sQuery(id+"F1.wireOp",EDGE,"E854");var subQ258=sQuery(id+"F1.wireOp",EDGE,"E271");var subQ259=sQuery(id+"F1.wireOp",EDGE,"E40");var subQ260=sQuery(id+"F1.wireOp",EDGE,"E860");var subQ261=sQuery(id+"F1.wireOp",EDGE,"E342");var subQ262=sQuery(id+"F1.wireOp",EDGE,"E317");var subQ263=sQuery(id+"F1.wireOp",EDGE,"E178");var subQ264=sQuery(id+"F1.wireOp",EDGE,"E376");var subQ265=sQuery(id+"F1.wireOp",EDGE,"E832");var subQ266=sQuery(id+"F1.wireOp",EDGE,"E320");var subQ267=sQuery(id+"F1.wireOp",EDGE,"E264");var subQ268=sQuery(id+"F1.wireOp",EDGE,"E279");var subQ269=sQuery(id+"F1.wireOp",EDGE,"E621");var subQ270=sQuery(id+"F1.wireOp",EDGE,"E198");var subQ271=sQuery(id+"F1.wireOp",EDGE,"E364");var subQ272=sQuery(id+"F1.wireOp",EDGE,"E200");var subQ273=sQuery(id+"F1.wireOp",EDGE,"E143");var subQ274=sQuery(id+"F1.wireOp",EDGE,"E868");var subQ275=sQuery(id+"F1.wireOp",EDGE,"E881");var subQ276=sQuery(id+"F1.wireOp",EDGE,"E72");var subQ277=sQuery(id+"F1.wireOp",EDGE,"E48");var subQ278=sQuery(id+"F1.wireOp",EDGE,"E657");var subQ279=sQuery(id+"F1.wireOp",EDGE,"E567");var subQ280=sQuery(id+"F1.wireOp",EDGE,"E905");var subQ281=sQuery(id+"F1.wireOp",EDGE,"E168");var subQ282=sQuery(id+"F1.wireOp",EDGE,"E111");var subQ283=sQuery(id+"F1.wireOp",EDGE,"E353");var subQ284=sQuery(id+"F1.wireOp",EDGE,"E469");var subQ285=sQuery(id+"F1.wireOp",EDGE,"E37");var subQ286=sQuery(id+"F1.wireOp",EDGE,"E618");var subQ287=sQuery(id+"F1.wireOp",EDGE,"E179");var subQ288=sQuery(id+"F1.wireOp",EDGE,"E15");var subQ289=sQuery(id+"F1.wireOp",EDGE,"E740");var subQ290=sQuery(id+"F1.wireOp",EDGE,"E681");var subQ291=sQuery(id+"F1.wireOp",EDGE,"E711");var subQ292=sQuery(id+"F1.wireOp",EDGE,"E246");var subQ293=sQuery(id+"F1.wireOp",EDGE,"E889");var subQ294=sQuery(id+"F1.wireOp",EDGE,"E606");var subQ295=sQuery(id+"F1.wireOp",EDGE,"E825");var subQ296=sQuery(id+"F1.wireOp",EDGE,"E859");var subQ297=sQuery(id+"F1.wireOp",EDGE,"E58");var subQ298=sQuery(id+"F1.wireOp",EDGE,"E576");var subQ299=sQuery(id+"F1.wireOp",EDGE,"E41");var subQ300=sQuery(id+"F1.wireOp",EDGE,"E64");var subQ301=sQuery(id+"F1.wireOp",EDGE,"E673");var subQ302=sQuery(id+"F1.wireOp",EDGE,"E583");var subQ303=sQuery(id+"F1.wireOp",EDGE,"E8");var subQ304=sQuery(id+"F1.wireOp",EDGE,"E733");var subQ305=sQuery(id+"F1.wireOp",EDGE,"E18");var subQ306=sQuery(id+"F1.wireOp",EDGE,"E627");var subQ307=sQuery(id+"F1.wireOp",EDGE,"E260");var subQ308=sQuery(id+"F1.wireOp",EDGE,"E237");var subQ309=sQuery(id+"F1.wireOp",EDGE,"E249");var subQ310=sQuery(id+"F1.wireOp",EDGE,"E30");var subQ311=sQuery(id+"F1.wireOp",EDGE,"E755");var subQ312=sQuery(id+"F1.wireOp",EDGE,"E637");var subQ313=sQuery(id+"F1.wireOp",EDGE,"E639");var subQ314=sQuery(id+"F1.wireOp",EDGE,"E395");var subQ315=sQuery(id+"F1.wireOp",EDGE,"E7");var subQ316=sQuery(id+"F1.wireOp",EDGE,"E863");var subQ317=sQuery(id+"F1.wireOp",EDGE,"E188");var subQ318=sQuery(id+"F1.wireOp",EDGE,"E24");var subQ319=sQuery(id+"F1.wireOp",EDGE,"E749");var subQ320=sQuery(id+"F1.wireOp",EDGE,"E635");var subQ321=sQuery(id+"F1.wireOp",EDGE,"E897");var subQ322=sQuery(id+"F1.wireOp",EDGE,"E150");var subQ323=sQuery(id+"F1.wireOp",EDGE,"E759");var subQ324=sQuery(id+"F1.wireOp",EDGE,"E28");var subQ325=sQuery(id+"F1.wireOp",EDGE,"E546");var subQ326=sQuery(id+"F1.wireOp",EDGE,"E493");var subQ327=sQuery(id+"F1.wireOp",EDGE,"E253");var subQ328=sQuery(id+"F1.wireOp",EDGE,"E34");var subQ329=sQuery(id+"F1.wireOp",EDGE,"E643");var subQ330=sQuery(id+"F1.wireOp",EDGE,"E11");var subQ331=sQuery(id+"F1.wireOp",EDGE,"E276");var subQ332=sQuery(id+"F1.wireOp",EDGE,"E10");var subQ333=sQuery(id+"F1.wireOp",EDGE,"E287");var subQ334=sQuery(id+"F1.wireOp",EDGE,"E21");var subQ335=sQuery(id+"F1.wireOp",EDGE,"E190");var subQ336=sQuery(id+"F1.wireOp",EDGE,"E165");var subQ337=sQuery(id+"F1.wireOp",EDGE,"E289");var subQ338=sQuery(id+"F1.wireOp",EDGE,"E256");var subQ339=sQuery(id+"F1.wireOp",EDGE,"E14");var subQ340=sQuery(id+"F1.wireOp",EDGE,"E623");var subQ341=sQuery(id+"F1.wireOp",EDGE,"E233");var subQ342=sQuery(id+"F1.wireOp",EDGE,"E257");var subQ343=sQuery(id+"F1.wireOp",EDGE,"E191");var subQ344=sQuery(id+"F1.wireOp",EDGE,"E166");var subQ345=sQuery(id+"F1.wireOp",EDGE,"E891");var subQ346=sQuery(id+"F1.wireOp",EDGE,"E775");var subQ347=sQuery(id+"F1.wireOp",EDGE,"E149");var subQ348=sQuery(id+"F1.wireOp",EDGE,"E651");var subQ349=sQuery(id+"F1.wireOp",EDGE,"E219");var subQ350=sQuery(id+"F1.wireOp",EDGE,"E579");var subQ351=sQuery(id+"F1.wireOp",EDGE,"E273");var subQ352=sQuery(id+"F1.wireOp",EDGE,"E549");var subQ353=sQuery(id+"F1.wireOp",EDGE,"E515");var subQ354=sQuery(id+"F1.wireOp",EDGE,"E433");var subQ355=sQuery(id+"F1.wireOp",EDGE,"E631");var subQ356=sQuery(id+"F1.wireOp",EDGE,"E282");var subQ357=sQuery(id+"F1.wireOp",EDGE,"E63");var subQ358=sQuery(id+"F1.wireOp",EDGE,"E449");var subQ359=sQuery(id+"F1.wireOp",EDGE,"E647");var subQ360=sQuery(id+"F1.wireOp",EDGE,"E476");var subQ361=sQuery(id+"F1.wireOp",EDGE,"E102");var subQ362=sQuery(id+"F1.wireOp",EDGE,"E300");var subQ363=sQuery(id+"F1.wireOp",EDGE,"E77");var subQ364=sQuery(id+"F1.wireOp",EDGE,"E712");var subQ365=sQuery(id+"F1.wireOp",EDGE,"E371");var subQ366=sQuery(id+"F1.wireOp",EDGE,"E230");var subQ367=sQuery(id+"F1.wireOp",EDGE,"E590");var subQ368=sQuery(id+"F1.wireOp",EDGE,"E560");var subQ369=sQuery(id+"F1.wireOp",EDGE,"E60");var subQ370=sQuery(id+"F1.wireOp",EDGE,"E716");var subQ371=sQuery(id+"F1.wireOp",EDGE,"E456");var subQ372=sQuery(id+"F1.wireOp",EDGE,"E268");var subQ373=sQuery(id+"F1.wireOp",EDGE,"E327");var subQ374=sQuery(id+"F1.wireOp",EDGE,"E754");var subQ375=sQuery(id+"F1.wireOp",EDGE,"E523");var subQ376=sQuery(id+"F1.wireOp",EDGE,"E506");var subQ377=sQuery(id+"F1.wireOp",EDGE,"E428");var subQ378=sQuery(id+"F1.wireOp",EDGE,"E333");var subQ379=sQuery(id+"F1.wireOp",EDGE,"E451");var subQ380=sQuery(id+"F1.wireOp",EDGE,"E719");var subQ381=sQuery(id+"F1.wireOp",EDGE,"E845");var subQ382=sQuery(id+"F1.wireOp",EDGE,"E446");var subQ383=sQuery(id+"F1.wireOp",EDGE,"E723");var subQ384=sQuery(id+"F1.wireOp",EDGE,"E339");var subQ385=sQuery(id+"F1.wireOp",EDGE,"E455");var subQ386=sQuery(id+"F1.wireOp",EDGE,"E837");var subQ387=sQuery(id+"F1.wireOp",EDGE,"E633");var subQ388=sQuery(id+"F1.wireOp",EDGE,"E247");var subQ389=sQuery(id+"F1.wireOp",EDGE,"E140");var subQ390=sQuery(id+"F1.wireOp",EDGE,"E83");var subQ391=sQuery(id+"F1.wireOp",EDGE,"E808");var subQ392=sQuery(id+"F1.wireOp",EDGE,"E195");var subQ393=sQuery(id+"F1.wireOp",EDGE,"E732");var subQ394=sQuery(id+"F1.wireOp",EDGE,"E762");var subQ395=sQuery(id+"F1.wireOp",EDGE,"E511");var subQ396=sQuery(id+"F1.wireOp",EDGE,"E458");var subQ397=sQuery(id+"F1.wireOp",EDGE,"E281");var subQ398=sQuery(id+"F1.wireOp",EDGE,"E530");var subQ399=sQuery(id+"F1.wireOp",EDGE,"E477");var subQ400=sQuery(id+"F1.wireOp",EDGE,"E553");var subQ401=sQuery(id+"F1.wireOp",EDGE,"E665");var subQ402=sQuery(id+"F1.wireOp",EDGE,"E319");var subQ403=sQuery(id+"F1.wireOp",EDGE,"E479");var subQ404=sQuery(id+"F1.wireOp",EDGE,"E677");var subQ405=sQuery(id+"F1.wireOp",EDGE,"E736");var subQ406=sQuery(id+"F1.wireOp",EDGE,"E180");var subQ407=sQuery(id+"F1.wireOp",EDGE,"E16");var subQ408=sQuery(id+"F1.wireOp",EDGE,"E741");var subQ409=sQuery(id+"F1.wireOp",EDGE,"E789");var subQ410=sQuery(id+"F1.wireOp",EDGE,"E203");var subQ411=sQuery(id+"F1.wireOp",EDGE,"E226");var subQ412=sQuery(id+"F1.wireOp",EDGE,"E243");var subQ413=sQuery(id+"F1.wireOp",EDGE,"E792");var subQ414=sQuery(id+"F1.wireOp",EDGE,"E335");var subQ415=sQuery(id+"F1.wireOp",EDGE,"E259");var subQ416=sQuery(id+"F1.wireOp",EDGE,"E867");var subQ417=sQuery(id+"F1.wireOp",EDGE,"E533");var subQ418=sQuery(id+"F1.wireOp",EDGE,"E669");var subQ419=sQuery(id+"F1.wireOp",EDGE,"E529");var subQ420=sQuery(id+"F1.wireOp",EDGE,"E265");var subQ421=sQuery(id+"F1.wireOp",EDGE,"E440");var subQ422=sQuery(id+"F1.wireOp",EDGE,"E718");var subQ423=sQuery(id+"F1.wireOp",EDGE,"E302");var subQ424=sQuery(id+"F1.wireOp",EDGE,"E12");var subQ425=sQuery(id+"F1.wireOp",EDGE,"E700");var subQ426=sQuery(id+"F1.wireOp",EDGE,"E519");var subQ427=sQuery(id+"F1.wireOp",EDGE,"E814");var subQ428=sQuery(id+"F1.wireOp",EDGE,"E79");var subQ429=sQuery(id+"F1.wireOp",EDGE,"E298");var subQ430=sQuery(id+"F1.wireOp",EDGE,"E357");var subQ431=sQuery(id+"F1.wireOp",EDGE,"E295");var subQ432=sQuery(id+"F1.wireOp",EDGE,"E470");var subQ433=sQuery(id+"F1.wireOp",EDGE,"E463");var subQ434=sQuery(id+"F1.wireOp",EDGE,"E661");var subQ435=sQuery(id+"F1.wireOp",EDGE,"E404");var subQ436=sQuery(id+"F1.wireOp",EDGE,"E602");var subQ437=sQuery(id+"F1.wireOp",EDGE,"E69");var subQ438=sQuery(id+"F1.wireOp",EDGE,"E794");var subQ439=sQuery(id+"F1.wireOp",EDGE,"E486");var subQ440=sQuery(id+"F1.wireOp",EDGE,"E206");var subQ441=sQuery(id+"F1.wireOp",EDGE,"E830");var subQ442=sQuery(id+"F1.wireOp",EDGE,"E784");var subQ443=sQuery(id+"F1.wireOp",EDGE,"E252");var subQ444=sQuery(id+"F1.wireOp",EDGE,"E88");var subQ445=sQuery(id+"F1.wireOp",EDGE,"E588");var subQ446=sQuery(id+"F1.wireOp",EDGE,"E409");var subQ447=sQuery(id+"F1.wireOp",EDGE,"E286");var subQ448=sQuery(id+"F1.wireOp",EDGE,"E895");var subQ449=sQuery(id+"F1.wireOp",EDGE,"E622");var subQ450=sQuery(id+"F1.wireOp",EDGE,"E296");var subQ451=sQuery(id+"F1.wireOp",EDGE,"E597");var subQ452=sQuery(id+"F1.wireOp",EDGE,"E196");var subQ453=sQuery(id+"F1.wireOp",EDGE,"E805");var subQ454=sQuery(id+"F1.wireOp",EDGE,"E380");var subQ455=sQuery(id+"F1.wireOp",EDGE,"E323");var subQ456=sQuery(id+"F1.wireOp",EDGE,"E439");var subQ457=sQuery(id+"F1.wireOp",EDGE,"E822");var subQ458=sQuery(id+"F1.wireOp",EDGE,"E522");var subQ459=sQuery(id+"F1.wireOp",EDGE,"E214");var subQ460=sQuery(id+"F1.wireOp",EDGE,"E50");var subQ461=sQuery(id+"F1.wireOp",EDGE,"E600");var subQ462=sQuery(id+"F1.wireOp",EDGE,"E293");var subQ463=sQuery(id+"F1.wireOp",EDGE,"E346");var subQ464=sQuery(id+"F1.wireOp",EDGE,"E148");var subQ465=sQuery(id+"F1.wireOp",EDGE,"E207");var subQ466=sQuery(id+"F1.wireOp",EDGE,"E405");var subQ467=sQuery(id+"F1.wireOp",EDGE,"E326");var subQ468=sQuery(id+"F1.wireOp",EDGE,"E852");var subQ469=sQuery(id+"F1.wireOp",EDGE,"E343");var subQ470=sQuery(id+"F1.wireOp",EDGE,"E541");var subQ471=sQuery(id+"F1.wireOp",EDGE,"E737");var subQ472=sQuery(id+"F1.wireOp",EDGE,"E703");var subQ473=sQuery(id+"F1.wireOp",EDGE,"E100");var subQ474=sQuery(id+"F1.wireOp",EDGE,"E75");var subQ475=sQuery(id+"F1.wireOp",EDGE,"E803");var subQ476=sQuery(id+"F1.wireOp",EDGE,"E2");var subQ477=sQuery(id+"F1.wireOp",EDGE,"E552");var subQ478=sQuery(id+"F1.wireOp",EDGE,"E751");var subQ479=sQuery(id+"F1.wireOp",EDGE,"E893");var subQ480=sQuery(id+"F1.wireOp",EDGE,"E154");var subQ481=sQuery(id+"F1.wireOp",EDGE,"E97");var subQ482=sQuery(id+"F1.wireOp",EDGE,"E730");var subQ483=sQuery(id+"F1.wireOp",EDGE,"E131");var subQ484=sQuery(id+"F1.wireOp",EDGE,"E106");var subQ485=sQuery(id+"F1.wireOp",EDGE,"E373");var subQ486=sQuery(id+"F1.wireOp",EDGE,"E571");var subQ487=sQuery(id+"F1.wireOp",EDGE,"E348");var subQ488=sQuery(id+"F1.wireOp",EDGE,"E130");var subQ489=sQuery(id+"F1.wireOp",EDGE,"E105");var subQ490=sQuery(id+"F1.wireOp",EDGE,"E138");var subQ491=sQuery(id+"F1.wireOp",EDGE,"E81");var subQ492=sQuery(id+"F1.wireOp",EDGE,"E42");var subQ493=sQuery(id+"F1.wireOp",EDGE,"E369");var subQ494=sQuery(id+"F1.wireOp",EDGE,"E485");var subQ495=sQuery(id+"F1.wireOp",EDGE,"E767");var subQ496=sQuery(id+"F1.wireOp",EDGE,"E735");var subQ497=sQuery(id+"F1.wireOp",EDGE,"E277");var subQ498=sQuery(id+"F1.wireOp",EDGE,"E170");var subQ499=sQuery(id+"F1.wireOp",EDGE,"E113");var subQ500=sQuery(id+"F1.wireOp",EDGE,"E838");var subQ501=sQuery(id+"F1.wireOp",EDGE,"E785");var subQ502=sQuery(id+"F1.wireOp",EDGE,"E122");var subQ503=sQuery(id+"F1.wireOp",EDGE,"E194");var subQ504=sQuery(id+"F1.wireOp",EDGE,"E270");var subQ505=sQuery(id+"F1.wireOp",EDGE,"E713");var subQ506=sQuery(id+"F1.wireOp",EDGE,"E879");var subQ507=sQuery(id+"F1.wireOp",EDGE,"E325");var subQ508=sQuery(id+"F1.wireOp",EDGE,"E605");var subQ509=sQuery(id+"F1.wireOp",EDGE,"E204");var subQ510=sQuery(id+"F1.wireOp",EDGE,"E184");var subQ511=sQuery(id+"F1.wireOp",EDGE,"E127");var subQ512=sQuery(id+"F1.wireOp",EDGE,"E20");var subQ513=sQuery(id+"F1.wireOp",EDGE,"E570");var subQ514=sQuery(id+"F1.wireOp",EDGE,"E696");var subQ515=sQuery(id+"F1.wireOp",EDGE,"E161");var subQ516=sQuery(id+"F1.wireOp",EDGE,"E136");var subQ517=sQuery(id+"F1.wireOp",EDGE,"E861");var subQ518=sQuery(id+"F1.wireOp",EDGE,"E801");var subQ519=sQuery(id+"F1.wireOp",EDGE,"E614");var subQ520=sQuery(id+"F1.wireOp",EDGE,"E812");var subQ521=sQuery(id+"F1.wireOp",EDGE,"E707");var subQ522=sQuery(id+"F1.wireOp",EDGE,"E312");var subQ523=sQuery(id+"F1.wireOp",EDGE,"E613");var subQ524=sQuery(id+"F1.wireOp",EDGE,"E457");var subQ525=sQuery(id+"F1.wireOp",EDGE,"E152");var subQ526=sQuery(id+"F1.wireOp",EDGE,"E877");var subQ527=sQuery(id+"F1.wireOp",EDGE,"E224");var subQ528=sQuery(id+"F1.wireOp",EDGE,"E537");var subQ529=sQuery(id+"F1.wireOp",EDGE,"E773");var subQ530=sQuery(id+"F1.wireOp",EDGE,"E743");var subQ531=sQuery(id+"F1.wireOp",EDGE,"E61");var subQ532=sQuery(id+"F1.wireOp",EDGE,"E746");var subQ533=sQuery(id+"F1.wireOp",EDGE,"E693");var subQ534=sQuery(id+"F1.wireOp",EDGE,"E663");var subQ535=sQuery(id+"F1.wireOp",EDGE,"E108");var subQ536=sQuery(id+"F1.wireOp",EDGE,"E51");var subQ537=sQuery(id+"F1.wireOp",EDGE,"E401");var subQ538=sQuery(id+"F1.wireOp",EDGE,"E742");var subQ539=sQuery(id+"F1.wireOp",EDGE,"E22");var subQ540=sQuery(id+"F1.wireOp",EDGE,"E524");var subQ541=sQuery(id+"F1.wireOp",EDGE,"E545");var subQ542=sQuery(id+"F1.wireOp",EDGE,"E427");var subQ543=sQuery(id+"F1.wireOp",EDGE,"E299");var subQ544=sQuery(id+"F1.wireOp",EDGE,"E351");var subQ545=sQuery(id+"F1.wireOp",EDGE,"E574");var subQ546=sQuery(id+"F1.wireOp",EDGE,"E109");var subQ547=sQuery(id+"F1.wireOp",EDGE,"E52");var subQ548=sQuery(id+"F1.wireOp",EDGE,"E156");var subQ549=sQuery(id+"F1.wireOp",EDGE,"E99");var subQ550=sQuery(id+"F1.wireOp",EDGE,"E824");var subQ551=sQuery(id+"F1.wireOp",EDGE,"E274");var subQ552=sQuery(id+"F1.wireOp",EDGE,"E110");var subQ553=sQuery(id+"F1.wireOp",EDGE,"E329");var subQ554=sQuery(id+"F1.wireOp",EDGE,"E705");var subQ555=sQuery(id+"F1.wireOp",EDGE,"E903");var subQ556=sQuery(id+"F1.wireOp",EDGE,"E225");var subQ557=sQuery(id+"F1.wireOp",EDGE,"E821");var subQ558=sQuery(id+"F1.wireOp",EDGE,"E303");var subQ559=sQuery(id+"F1.wireOp",EDGE,"E689");var subQ560=sQuery(id+"F1.wireOp",EDGE,"E887");var subQ561=sQuery(id+"F1.wireOp",EDGE,"E667");var subQ562=sQuery(id+"F1.wireOp",EDGE,"E234");var subQ563=sQuery(id+"F1.wireOp",EDGE,"E290");var subQ564=sQuery(id+"F1.wireOp",EDGE,"E241");var subQ565=sQuery(id+"F1.wireOp",EDGE,"E304");var subQ566=sQuery(id+"F1.wireOp",EDGE,"E250");var subQ567=sQuery(id+"F1.wireOp",EDGE,"E816");var subQ568=sQuery(id+"F1.wireOp",EDGE,"E851");var subQ569=sQuery(id+"F1.wireOp",EDGE,"E283");var subQ570=sQuery(id+"F1.wireOp",EDGE,"E381");var subQ571=sQuery(id+"F1.wireOp",EDGE,"E382");var subQ572=sQuery(id+"F1.wireOp",EDGE,"E383");var subQ573=sQuery(id+"F1.wireOp",EDGE,"E384");var subQ574=sQuery(id+"F1.wireOp",EDGE,"E385");var subQ575=sQuery(id+"F1.wireOp",EDGE,"E386");var subQ576=sQuery(id+"F1.wireOp",EDGE,"E387");var subQ577=sQuery(id+"F1.wireOp",EDGE,"E388");var subQ578=sQuery(id+"F1.wireOp",EDGE,"E586");var subQ579=sQuery(id+"F1.wireOp",EDGE,"E389");var subQ580=sQuery(id+"F1.wireOp",EDGE,"E587");var subQ581=sQuery(id+"F1.wireOp",EDGE,"E392");var subQ582=sQuery(id+"F1.wireOp",EDGE,"E393");var subQ583=sQuery(id+"F1.wireOp",EDGE,"E394");var subQ584=sQuery(id+"F1.wireOp",EDGE,"E396");var subQ585=sQuery(id+"F1.wireOp",EDGE,"E397");var subQ586=sQuery(id+"F1.wireOp",EDGE,"E398");var subQ587=sQuery(id+"F1.wireOp",EDGE,"E399");var subQ588=sQuery(id+"F1.wireOp",EDGE,"E400");var subQ589=sQuery(id+"F1.wireOp",EDGE,"E402");var subQ590=sQuery(id+"F1.wireOp",EDGE,"E403");var subQ591=sQuery(id+"F1.wireOp",EDGE,"E601");var subQ592=sQuery(id+"F1.wireOp",EDGE,"E407");var subQ593=sQuery(id+"F1.wireOp",EDGE,"E408");var subQ594=sQuery(id+"F1.wireOp",EDGE,"E410");var subQ595=sQuery(id+"F1.wireOp",EDGE,"E411");var subQ596=sQuery(id+"F1.wireOp",EDGE,"E412");var subQ597=sQuery(id+"F1.wireOp",EDGE,"E578");var subQ598=sQuery(id+"F1.wireOp",EDGE,"E413");var subQ599=sQuery(id+"F1.wireOp",EDGE,"E414");var subQ600=sQuery(id+"F1.wireOp",EDGE,"E415");var subQ601=sQuery(id+"F1.wireOp",EDGE,"E416");var subQ602=sQuery(id+"F1.wireOp",EDGE,"E417");var subQ603=sQuery(id+"F1.wireOp",EDGE,"E418");var subQ604=sQuery(id+"F1.wireOp",EDGE,"E616");var subQ605=sQuery(id+"F1.wireOp",EDGE,"E419");var subQ606=sQuery(id+"F1.wireOp",EDGE,"E617");var subQ607=sQuery(id+"F1.wireOp",EDGE,"E422");var subQ608=sQuery(id+"F1.wireOp",EDGE,"E423");var subQ609=sQuery(id+"F1.wireOp",EDGE,"E424");var subQ610=sQuery(id+"F1.wireOp",EDGE,"E425");var subQ611=sQuery(id+"F1.wireOp",EDGE,"E426");var subQ612=sQuery(id+"F1.wireOp",EDGE,"E429");var subQ613=sQuery(id+"F1.wireOp",EDGE,"E430");var subQ614=sQuery(id+"F1.wireOp",EDGE,"E431");var subQ615=sQuery(id+"F1.wireOp",EDGE,"E432");var subQ616=sQuery(id+"F1.wireOp",EDGE,"E434");var subQ617=sQuery(id+"F1.wireOp",EDGE,"E632");var subQ618=sQuery(id+"F1.wireOp",EDGE,"E435");var subQ619=sQuery(id+"F1.wireOp",EDGE,"E437");var subQ620=sQuery(id+"F1.wireOp",EDGE,"E438");var subQ621=sQuery(id+"F1.wireOp",EDGE,"E441");var subQ622=sQuery(id+"F1.wireOp",EDGE,"E442");var subQ623=sQuery(id+"F1.wireOp",EDGE,"E608");var subQ624=sQuery(id+"F1.wireOp",EDGE,"E443");var subQ625=sQuery(id+"F1.wireOp",EDGE,"E444");var subQ626=sQuery(id+"F1.wireOp",EDGE,"E445");var subQ627=sQuery(id+"F1.wireOp",EDGE,"E447");var subQ628=sQuery(id+"F1.wireOp",EDGE,"E448");var subQ629=sQuery(id+"F1.wireOp",EDGE,"E646");var subQ630=sQuery(id+"F1.wireOp",EDGE,"E450");var subQ631=sQuery(id+"F1.wireOp",EDGE,"E452");var subQ632=sQuery(id+"F1.wireOp",EDGE,"E453");var subQ633=sQuery(id+"F1.wireOp",EDGE,"E454");var subQ634=sQuery(id+"F1.wireOp",EDGE,"E459");var subQ635=sQuery(id+"F1.wireOp",EDGE,"E460");var subQ636=sQuery(id+"F1.wireOp",EDGE,"E461");var subQ637=sQuery(id+"F1.wireOp",EDGE,"E462");var subQ638=sQuery(id+"F1.wireOp",EDGE,"E464");var subQ639=sQuery(id+"F1.wireOp",EDGE,"E662");var subQ640=sQuery(id+"F1.wireOp",EDGE,"E465");var subQ641=sQuery(id+"F1.wireOp",EDGE,"E466");var subQ642=sQuery(id+"F1.wireOp",EDGE,"E467");var subQ643=sQuery(id+"F1.wireOp",EDGE,"E468");var subQ644=sQuery(id+"F1.wireOp",EDGE,"E471");var subQ645=sQuery(id+"F1.wireOp",EDGE,"E472");var subQ646=sQuery(id+"F1.wireOp",EDGE,"E638");var subQ647=sQuery(id+"F1.wireOp",EDGE,"E473");var subQ648=sQuery(id+"F1.wireOp",EDGE,"E474");var subQ649=sQuery(id+"F1.wireOp",EDGE,"E475");var subQ650=sQuery(id+"F1.wireOp",EDGE,"E478");var subQ651=sQuery(id+"F1.wireOp",EDGE,"E676");var subQ652=sQuery(id+"F1.wireOp",EDGE,"E480");var subQ653=sQuery(id+"F1.wireOp",EDGE,"E481");var subQ654=sQuery(id+"F1.wireOp",EDGE,"E482");var subQ655=sQuery(id+"F1.wireOp",EDGE,"E483");var subQ656=sQuery(id+"F1.wireOp",EDGE,"E484");var subQ657=sQuery(id+"F1.wireOp",EDGE,"E487");var subQ658=sQuery(id+"F1.wireOp",EDGE,"E488");var subQ659=sQuery(id+"F1.wireOp",EDGE,"E489");var subQ660=sQuery(id+"F1.wireOp",EDGE,"E490");var subQ661=sQuery(id+"F1.wireOp",EDGE,"E491");var subQ662=sQuery(id+"F1.wireOp",EDGE,"E492");var subQ663=sQuery(id+"F1.wireOp",EDGE,"E494");var subQ664=sQuery(id+"F1.wireOp",EDGE,"E692");var subQ665=sQuery(id+"F1.wireOp",EDGE,"E495");var subQ666=sQuery(id+"F1.wireOp",EDGE,"E496");var subQ667=sQuery(id+"F1.wireOp",EDGE,"E497");var subQ668=sQuery(id+"F1.wireOp",EDGE,"E498");var subQ669=sQuery(id+"F1.wireOp",EDGE,"E499");var subQ670=sQuery(id+"F1.wireOp",EDGE,"E500");var subQ671=sQuery(id+"F1.wireOp",EDGE,"E501");var subQ672=sQuery(id+"F1.wireOp",EDGE,"E502");var subQ673=sQuery(id+"F1.wireOp",EDGE,"E503");var subQ674=sQuery(id+"F1.wireOp",EDGE,"E504");var subQ675=sQuery(id+"F1.wireOp",EDGE,"E505");var subQ676=sQuery(id+"F1.wireOp",EDGE,"E507");var subQ677=sQuery(id+"F1.wireOp",EDGE,"E508");var subQ678=sQuery(id+"F1.wireOp",EDGE,"E509");var subQ679=sQuery(id+"F1.wireOp",EDGE,"E510");var subQ680=sQuery(id+"F1.wireOp",EDGE,"E512");var subQ681=sQuery(id+"F1.wireOp",EDGE,"E513");var subQ682=sQuery(id+"F1.wireOp",EDGE,"E514");var subQ683=sQuery(id+"F1.wireOp",EDGE,"E516");var subQ684=sQuery(id+"F1.wireOp",EDGE,"E517");var subQ685=sQuery(id+"F1.wireOp",EDGE,"E518");var subQ686=sQuery(id+"F1.wireOp",EDGE,"E520");var subQ687=sQuery(id+"F1.wireOp",EDGE,"E521");var subQ688=sQuery(id+"F1.wireOp",EDGE,"E525");var subQ689=sQuery(id+"F1.wireOp",EDGE,"E526");var subQ690=sQuery(id+"F1.wireOp",EDGE,"E527");var subQ691=sQuery(id+"F1.wireOp",EDGE,"E528");var subQ692=sQuery(id+"F1.wireOp",EDGE,"E531");var subQ693=sQuery(id+"F1.wireOp",EDGE,"E532");var subQ694=sQuery(id+"F1.wireOp",EDGE,"E534");var subQ695=sQuery(id+"F1.wireOp",EDGE,"E535");var subQ696=sQuery(id+"F1.wireOp",EDGE,"E536");var subQ697=sQuery(id+"F1.wireOp",EDGE,"E538");var subQ698=sQuery(id+"F1.wireOp",EDGE,"E539");var subQ699=sQuery(id+"F1.wireOp",EDGE,"E540");var subQ700=sQuery(id+"F1.wireOp",EDGE,"E542");var subQ701=sQuery(id+"F1.wireOp",EDGE,"E543");var subQ702=sQuery(id+"F1.wireOp",EDGE,"E544");var subQ703=sQuery(id+"F1.wireOp",EDGE,"E547");var subQ704=sQuery(id+"F1.wireOp",EDGE,"E548");var subQ705=sQuery(id+"F1.wireOp",EDGE,"E550");var subQ706=sQuery(id+"F1.wireOp",EDGE,"E551");var subQ707=sQuery(id+"F1.wireOp",EDGE,"E554");var subQ708=sQuery(id+"F1.wireOp",EDGE,"E555");var subQ709=sQuery(id+"F1.wireOp",EDGE,"E558");var subQ710=sQuery(id+"F1.wireOp",EDGE,"E559");var subQ711=sQuery(id+"F1.wireOp",EDGE,"E561");var subQ712=sQuery(id+"F1.wireOp",EDGE,"E562");var subQ713=sQuery(id+"F1.wireOp",EDGE,"E563");var subQ714=sQuery(id+"F1.wireOp",EDGE,"E564");var subQ715=sQuery(id+"F1.wireOp",EDGE,"E565");var subQ716=sQuery(id+"F1.wireOp",EDGE,"E566");var subQ717=sQuery(id+"F1.wireOp",EDGE,"E568");var subQ718=sQuery(id+"F1.wireOp",EDGE,"E569");var subQ719=sQuery(id+"F1.wireOp",EDGE,"E573");var subQ720=sQuery(id+"F1.wireOp",EDGE,"E575");var subQ721=sQuery(id+"F1.wireOp",EDGE,"E577");var subQ722=sQuery(id+"F1.wireOp",EDGE,"E580");var subQ723=sQuery(id+"F1.wireOp",EDGE,"E581");var subQ724=sQuery(id+"F1.wireOp",EDGE,"E582");var subQ725=sQuery(id+"F1.wireOp",EDGE,"E584");var subQ726=sQuery(id+"F1.wireOp",EDGE,"E585");var subQ727=sQuery(id+"F1.wireOp",EDGE,"E589");var subQ728=sQuery(id+"F1.wireOp",EDGE,"E591");var subQ729=sQuery(id+"F1.wireOp",EDGE,"E592");var subQ730=sQuery(id+"F1.wireOp",EDGE,"E593");var subQ731=sQuery(id+"F1.wireOp",EDGE,"E594");var subQ732=sQuery(id+"F1.wireOp",EDGE,"E595");var subQ733=sQuery(id+"F1.wireOp",EDGE,"E596");var subQ734=sQuery(id+"F1.wireOp",EDGE,"E598");var subQ735=sQuery(id+"F1.wireOp",EDGE,"E599");var subQ736=sQuery(id+"F1.wireOp",EDGE,"E797");var subQ737=sQuery(id+"F1.wireOp",EDGE,"E603");var subQ738=sQuery(id+"F1.wireOp",EDGE,"E604");var subQ739=sQuery(id+"F1.wireOp",EDGE,"E607");var subQ740=sQuery(id+"F1.wireOp",EDGE,"E609");var subQ741=sQuery(id+"F1.wireOp",EDGE,"E610");var subQ742=sQuery(id+"F1.wireOp",EDGE,"E611");var subQ743=sQuery(id+"F1.wireOp",EDGE,"E612");var subQ744=sQuery(id+"F1.wireOp",EDGE,"E615");var subQ745=sQuery(id+"F1.wireOp",EDGE,"E813");var subQ746=sQuery(id+"F1.wireOp",EDGE,"E619");var subQ747=sQuery(id+"F1.wireOp",EDGE,"E620");var subQ748=sQuery(id+"F1.wireOp",EDGE,"E624");var subQ749=sQuery(id+"F1.wireOp",EDGE,"E625");var subQ750=sQuery(id+"F1.wireOp",EDGE,"E626");var subQ751=sQuery(id+"F1.wireOp",EDGE,"E628");var subQ752=sQuery(id+"F1.wireOp",EDGE,"E629");var subQ753=sQuery(id+"F1.wireOp",EDGE,"E827");var subQ754=sQuery(id+"F1.wireOp",EDGE,"E630");var subQ755=sQuery(id+"F1.wireOp",EDGE,"E828");var subQ756=sQuery(id+"F1.wireOp",EDGE,"E634");var subQ757=sQuery(id+"F1.wireOp",EDGE,"E636");var subQ758=sQuery(id+"F1.wireOp",EDGE,"E640");var subQ759=sQuery(id+"F1.wireOp",EDGE,"E641");var subQ760=sQuery(id+"F1.wireOp",EDGE,"E642");var subQ761=sQuery(id+"F1.wireOp",EDGE,"E644");var subQ762=sQuery(id+"F1.wireOp",EDGE,"E842");var subQ763=sQuery(id+"F1.wireOp",EDGE,"E645");var subQ764=sQuery(id+"F1.wireOp",EDGE,"E843");var subQ765=sQuery(id+"F1.wireOp",EDGE,"E648");var subQ766=sQuery(id+"F1.wireOp",EDGE,"E649");var subQ767=sQuery(id+"F1.wireOp",EDGE,"E650");var subQ768=sQuery(id+"F1.wireOp",EDGE,"E652");var subQ769=sQuery(id+"F1.wireOp",EDGE,"E653");var subQ770=sQuery(id+"F1.wireOp",EDGE,"E819");var subQ771=sQuery(id+"F1.wireOp",EDGE,"E654");var subQ772=sQuery(id+"F1.wireOp",EDGE,"E655");var subQ773=sQuery(id+"F1.wireOp",EDGE,"E656");var subQ774=sQuery(id+"F1.wireOp",EDGE,"E658");var subQ775=sQuery(id+"F1.wireOp",EDGE,"E659");var subQ776=sQuery(id+"F1.wireOp",EDGE,"E857");var subQ777=sQuery(id+"F1.wireOp",EDGE,"E660");var subQ778=sQuery(id+"F1.wireOp",EDGE,"E858");var subQ779=sQuery(id+"F1.wireOp",EDGE,"E664");var subQ780=sQuery(id+"F1.wireOp",EDGE,"E666");var subQ781=sQuery(id+"F1.wireOp",EDGE,"E668");var subQ782=sQuery(id+"F1.wireOp",EDGE,"E670");var subQ783=sQuery(id+"F1.wireOp",EDGE,"E671");var subQ784=sQuery(id+"F1.wireOp",EDGE,"E672");var subQ785=sQuery(id+"F1.wireOp",EDGE,"E674");var subQ786=sQuery(id+"F1.wireOp",EDGE,"E872");var subQ787=sQuery(id+"F1.wireOp",EDGE,"E675");var subQ788=sQuery(id+"F1.wireOp",EDGE,"E873");var subQ789=sQuery(id+"F1.wireOp",EDGE,"E678");var subQ790=sQuery(id+"F1.wireOp",EDGE,"E679");var subQ791=sQuery(id+"F1.wireOp",EDGE,"E680");var subQ792=sQuery(id+"F1.wireOp",EDGE,"E682");var subQ793=sQuery(id+"F1.wireOp",EDGE,"E683");var subQ794=sQuery(id+"F1.wireOp",EDGE,"E849");var subQ795=sQuery(id+"F1.wireOp",EDGE,"E684");var subQ796=sQuery(id+"F1.wireOp",EDGE,"E685");var subQ797=sQuery(id+"F1.wireOp",EDGE,"E686");var subQ798=sQuery(id+"F1.wireOp",EDGE,"E687");var subQ799=sQuery(id+"F1.wireOp",EDGE,"E688");var subQ800=sQuery(id+"F1.wireOp",EDGE,"E690");var subQ801=sQuery(id+"F1.wireOp",EDGE,"E888");var subQ802=sQuery(id+"F1.wireOp",EDGE,"E691");var subQ803=sQuery(id+"F1.wireOp",EDGE,"E694");var subQ804=sQuery(id+"F1.wireOp",EDGE,"E695");var subQ805=sQuery(id+"F1.wireOp",EDGE,"E697");var subQ806=sQuery(id+"F1.wireOp",EDGE,"E698");var subQ807=sQuery(id+"F1.wireOp",EDGE,"E699");var subQ808=sQuery(id+"F1.wireOp",EDGE,"E701");var subQ809=sQuery(id+"F1.wireOp",EDGE,"E702");var subQ810=sQuery(id+"F1.wireOp",EDGE,"E704");var subQ811=sQuery(id+"F1.wireOp",EDGE,"E902");var subQ812=sQuery(id+"F1.wireOp",EDGE,"E706");var subQ813=sQuery(id+"F1.wireOp",EDGE,"E708");var subQ814=sQuery(id+"F1.wireOp",EDGE,"E709");var subQ815=sQuery(id+"F1.wireOp",EDGE,"E710");var subQ816=sQuery(id+"F1.wireOp",EDGE,"E714");var subQ817=sQuery(id+"F1.wireOp",EDGE,"E715");var subQ818=sQuery(id+"F1.wireOp",EDGE,"E717");var subQ819=sQuery(id+"F1.wireOp",EDGE,"E720");var subQ820=sQuery(id+"F1.wireOp",EDGE,"E721");var subQ821=sQuery(id+"F1.wireOp",EDGE,"E722");var subQ822=sQuery(id+"F1.wireOp",EDGE,"E724");var subQ823=sQuery(id+"F1.wireOp",EDGE,"E725");var subQ824=sQuery(id+"F1.wireOp",EDGE,"E727");var subQ825=sQuery(id+"F1.wireOp",EDGE,"E728");var subQ826=sQuery(id+"F1.wireOp",EDGE,"E729");var subQ827=sQuery(id+"F1.wireOp",EDGE,"E731");var subQ828=sQuery(id+"F1.wireOp",EDGE,"E734");var subQ829=sQuery(id+"F1.wireOp",EDGE,"E738");var subQ830=sQuery(id+"F1.wireOp",EDGE,"E739");var subQ831=sQuery(id+"F1.wireOp",EDGE,"E744");var subQ832=sQuery(id+"F1.wireOp",EDGE,"E745");var subQ833=sQuery(id+"F1.wireOp",EDGE,"E747");var subQ834=sQuery(id+"F1.wireOp",EDGE,"E750");var subQ835=sQuery(id+"F1.wireOp",EDGE,"E752");var subQ836=sQuery(id+"F1.wireOp",EDGE,"E753");var subQ837=sQuery(id+"F1.wireOp",EDGE,"E757");var subQ838=sQuery(id+"F1.wireOp",EDGE,"E758");var subQ839=sQuery(id+"F1.wireOp",EDGE,"E760");var subQ840=sQuery(id+"F1.wireOp",EDGE,"E761");var subQ841=sQuery(id+"F1.wireOp",EDGE,"E765");var subQ842=sQuery(id+"F1.wireOp",EDGE,"E766");var subQ843=sQuery(id+"F1.wireOp",EDGE,"E768");var subQ844=sQuery(id+"F1.wireOp",EDGE,"E769");var subQ845=sQuery(id+"F1.wireOp",EDGE,"E772");var subQ846=sQuery(id+"F1.wireOp",EDGE,"E774");var subQ847=sQuery(id+"F1.wireOp",EDGE,"E776");var subQ848=sQuery(id+"F1.wireOp",EDGE,"E777");var subQ849=sQuery(id+"F1.wireOp",EDGE,"E780");var subQ850=sQuery(id+"F1.wireOp",EDGE,"E781");var subQ851=sQuery(id+"F1.wireOp",EDGE,"E782");var subQ852=sQuery(id+"F1.wireOp",EDGE,"E783");var subQ853=sQuery(id+"F1.wireOp",EDGE,"E786");var subQ854=sQuery(id+"F1.wireOp",EDGE,"E787");var subQ855=sQuery(id+"F1.wireOp",EDGE,"E788");var subQ856=sQuery(id+"F1.wireOp",EDGE,"E790");var subQ857=sQuery(id+"F1.wireOp",EDGE,"E791");var subQ858=sQuery(id+"F1.wireOp",EDGE,"E795");var subQ859=sQuery(id+"F1.wireOp",EDGE,"E796");var subQ860=sQuery(id+"F1.wireOp",EDGE,"E798");var subQ861=sQuery(id+"F1.wireOp",EDGE,"E799");var subQ862=sQuery(id+"F1.wireOp",EDGE,"E800");var subQ863=sQuery(id+"F1.wireOp",EDGE,"E802");var subQ864=sQuery(id+"F1.wireOp",EDGE,"E804");var subQ865=sQuery(id+"F1.wireOp",EDGE,"E806");var subQ866=sQuery(id+"F1.wireOp",EDGE,"E807");var subQ867=sQuery(id+"F1.wireOp",EDGE,"E810");var subQ868=sQuery(id+"F1.wireOp",EDGE,"E811");var subQ869=sQuery(id+"F1.wireOp",EDGE,"E815");var subQ870=sQuery(id+"F1.wireOp",EDGE,"E817");var subQ871=sQuery(id+"F1.wireOp",EDGE,"E818");var subQ872=sQuery(id+"F1.wireOp",EDGE,"E820");var subQ873=sQuery(id+"F1.wireOp",EDGE,"E826");var subQ874=sQuery(id+"F1.wireOp",EDGE,"E829");var subQ875=sQuery(id+"F1.wireOp",EDGE,"E831");var subQ876=sQuery(id+"F1.wireOp",EDGE,"E833");var subQ877=sQuery(id+"F1.wireOp",EDGE,"E834");var subQ878=sQuery(id+"F1.wireOp",EDGE,"E835");var subQ879=sQuery(id+"F1.wireOp",EDGE,"E836");var subQ880=sQuery(id+"F1.wireOp",EDGE,"E840");var subQ881=sQuery(id+"F1.wireOp",EDGE,"E841");var subQ882=sQuery(id+"F1.wireOp",EDGE,"E844");var subQ883=sQuery(id+"F1.wireOp",EDGE,"E847");var subQ884=sQuery(id+"F1.wireOp",EDGE,"E848");var subQ885=sQuery(id+"F1.wireOp",EDGE,"E850");var subQ886=sQuery(id+"F1.wireOp",EDGE,"E855");var subQ887=sQuery(id+"F1.wireOp",EDGE,"E856");var subQ888=sQuery(id+"F1.wireOp",EDGE,"E864");var subQ889=sQuery(id+"F1.wireOp",EDGE,"E865");var subQ890=sQuery(id+"F1.wireOp",EDGE,"E866");var subQ891=sQuery(id+"F1.wireOp",EDGE,"E870");var subQ892=sQuery(id+"F1.wireOp",EDGE,"E871");var subQ893=sQuery(id+"F1.wireOp",EDGE,"E874");var subQ894=sQuery(id+"F1.wireOp",EDGE,"E875");var subQ895=sQuery(id+"F1.wireOp",EDGE,"E878");var subQ896=sQuery(id+"F1.wireOp",EDGE,"E880");var subQ897=sQuery(id+"F1.wireOp",EDGE,"E882");var subQ898=sQuery(id+"F1.wireOp",EDGE,"E885");var subQ899=sQuery(id+"F1.wireOp",EDGE,"E886");var subQ900=sQuery(id+"F1.wireOp",EDGE,"E890");var subQ901=sQuery(id+"F1.wireOp",EDGE,"E894");var subQ902=sQuery(id+"F1.wireOp",EDGE,"E896");var subQ903=sQuery(id+"F1.wireOp",EDGE,"E898");var subQ904=sQuery(id+"F1.wireOp",EDGE,"E900");var subQ905=sQuery(id+"F1.wireOp",EDGE,"E901");var subQ906=sQuery(id+"F1.wireOp",EDGE,"E904");var subQ907=sQuery(id+"F1.wireOp",EDGE,"E908");var subQ908=sQuery(id+"F1.wireOp",EDGE,"E909");var subQ909=sQuery(id+"F1.wireOp",EDGE,"E910");Q0=makeQuery(id+"F4.boolean.opBoolean","SPLIT",FACE,{"disambiguationData":[TD([makeQuery(id+"F3.opExtrude","SWEPT_FACE",FACE,{"disambiguationData":[OSD([sQuery(id+"F2.wireOp",EDGE,"E912")])]})])],"derivedFrom":makeQuery(id+"F4.opExtrude","CAP_FACE",FACE,{"disambiguationData":[OSD([sQuery(id+"F1.wireOp",EDGE,"E0"),subQ247,subQ476,subQ246,subQ245,subQ244,subQ242,subQ315,subQ303,subQ241,subQ332,subQ330,subQ424,subQ240,subQ339,subQ288,subQ407,subQ239,subQ305,subQ238,subQ512,subQ334,subQ539,subQ234,subQ318,subQ232,subQ231,subQ230,subQ324,subQ229,subQ310,subQ227,subQ226,subQ225,subQ328,subQ224,subQ223,subQ285,subQ220,subQ218,subQ259,subQ299,subQ492,subQ217,subQ216,subQ215,subQ212,subQ210,subQ277,subQ209,subQ460,subQ536,subQ547,subQ206,subQ203,subQ201,subQ200,subQ199,subQ297,subQ197,subQ369,subQ531,subQ196,subQ357,subQ300,subQ195,subQ194,subQ192,subQ189,subQ437,subQ214,subQ187,subQ276,subQ186,subQ185,subQ474,subQ184,subQ363,subQ182,subQ428,subQ181,subQ491,subQ179,subQ390,subQ176,subQ172,subQ171,subQ121,subQ444,subQ169,subQ168,subQ167,subQ166,subQ222,subQ165,subQ164,subQ163,subQ481,subQ160,subQ549,subQ473,subQ183,subQ361,subQ133,subQ158,subQ489,subQ484,subQ157,subQ535,subQ546,subQ552,subQ282,subQ154,subQ499,subQ151,subQ147,subQ146,subQ92,subQ88,subQ145,subQ144,subQ143,subQ502,subQ193,subQ191,subQ188,subQ237,subQ511,subQ141,subQ256,subQ488,subQ483,subQ155,subQ102,subQ139,subQ138,subQ516,subQ136,subQ490,subQ178,subQ389,subQ174,subQ131,subQ273,subQ128,subQ123,subQ122,subQ118,subQ464,subQ347,subQ322,subQ115,subQ525,subQ162,subQ480,subQ159,subQ548,subQ114,subQ112,subQ109,subQ137,subQ515,subQ134,subQ74,subQ107,subQ336,subQ344,subQ105,subQ281,subQ153,subQ498,subQ149,subQ100,subQ99,subQ97,subQ94,subQ93,subQ89,subQ263,subQ287,subQ406,subQ84,subQ82,subQ236,subQ510,subQ140,subQ255,subQ233,subQ317,subQ81,subQ335,subQ343,subQ103,subQ79,subQ503,subQ392,subQ452,subQ77,subQ270,subQ130,subQ272,subQ126,subQ72,subQ410,subQ509,subQ71,subQ440,subQ465,subQ69,subQ66,subQ211,subQ65,subQ64,subQ208,subQ459,subQ111,subQ108,subQ205,subQ202,subQ349,subQ63,subQ198,subQ75,subQ61,subQ527,subQ556,subQ411,subQ59,subQ58,subQ57,subQ366,subQ96,subQ56,subQ341,subQ562,subQ55,subQ54,subQ308,subQ52,subQ50,subQ49,subQ564,subQ48,subQ412,subQ180,subQ47,subQ292,subQ388,subQ173,subQ309,subQ566,subQ170,subQ443,subQ327,subQ46,subQ251,subQ338,subQ342,subQ45,subQ415,subQ307,subQ44,subQ42,subQ41,subQ267,subQ420,subQ40,subQ39,subQ372,subQ38,subQ504,subQ258,subQ37,subQ351,subQ551,subQ36,subQ331,subQ497,subQ148,subQ268,subQ253,subQ397,subQ356,subQ569,subQ35,subQ120,subQ447,subQ333,subQ34,subQ337,subQ563,subQ33,subQ32,subQ462,subQ30,subQ431,subQ450,subQ29,subQ429,subQ543,subQ362,subQ132,subQ423,subQ558,subQ565,subQ28,subQ27,subQ175,subQ125,subQ249,subQ26,subQ117,subQ522,subQ250,subQ25,subQ91,subQ87,subQ262,subQ24,subQ402,subQ266,subQ23,subQ22,subQ455,subQ20,subQ507,subQ467,subQ373,subQ19,subQ553,subQ156,subQ101,subQ78,subQ378,subQ18,subQ414,subQ17,subQ150,subQ95,subQ384,subQ16,subQ86,subQ261,subQ469,subQ15,subQ119,subQ463,subQ68,subQ487,subQ31,subQ14,subQ544,subQ13,subQ283,subQ12,subQ11,subQ10,subQ430,subQ8,subQ6,subQ135,subQ73,subQ60,subQ5,subQ271,subQ124,subQ4,subQ127,subQ43,subQ493,subQ3,subQ365,subQ67,subQ485,subQ1,subQ90,subQ264,subQ51,subQ0,subQ21,subQ454,subQ570,subQ571,subQ572,subQ573,subQ574,subQ575,subQ576,subQ577,subQ579,subQ104,subQ80,subQ581,subQ582,subQ583,subQ314,subQ584,subQ585,subQ586,subQ587,subQ588,subQ537,subQ589,subQ590,subQ435,subQ466,subQ70,subQ592,subQ593,subQ446,subQ594,subQ595,subQ596,subQ598,subQ599,subQ600,subQ601,subQ602,subQ603,subQ605,subQ76,subQ62,subQ607,subQ608,subQ609,subQ610,subQ611,subQ542,subQ377,subQ612,subQ613,subQ614,subQ615,subQ354,subQ616,subQ618,subQ53,subQ619,subQ620,subQ456,subQ421,subQ621,subQ622,subQ624,subQ625,subQ626,subQ382,subQ627,subQ628,subQ358,subQ630,subQ379,subQ631,subQ632,subQ633,subQ385,subQ371,subQ524,subQ396,subQ634,subQ635,subQ636,subQ637,subQ433,subQ638,subQ640,subQ641,subQ642,subQ643,subQ284,subQ432,subQ644,subQ645,subQ647,subQ648,subQ649,subQ360,subQ399,subQ650,subQ403,subQ652,subQ653,subQ654,subQ655,subQ656,subQ494,subQ439,subQ657,subQ658,subQ659,subQ660,subQ661,subQ662,subQ326,subQ663,subQ665,subQ666,subQ667,subQ668,subQ669,subQ670,subQ671,subQ672,subQ673,subQ674,subQ675,subQ376,subQ676,subQ677,subQ678,subQ679,subQ395,subQ680,subQ681,subQ682,subQ353,subQ683,subQ684,subQ685,subQ426,subQ686,subQ687,subQ458,subQ375,subQ540,subQ688,subQ689,subQ690,subQ691,subQ419,subQ398,subQ692,subQ693,subQ417,subQ694,subQ695,subQ696,subQ528,subQ697,subQ698,subQ699,subQ470,subQ700,subQ701,subQ702,subQ541,subQ325,subQ703,subQ704,subQ352,subQ705,subQ706,subQ477,subQ400,subQ707,subQ708,subQ9,subQ7,subQ709,subQ710,subQ368,subQ711,subQ712,subQ713,subQ714,subQ715,subQ716,subQ279,subQ717,subQ718,subQ513,subQ486,subQ2,subQ719,subQ545,subQ720,subQ298,subQ721,subQ597,subQ350,subQ722,subQ723,subQ724,subQ302,subQ725,subQ726,subQ578,subQ580,subQ445,subQ727,subQ367,subQ728,subQ729,subQ730,subQ731,subQ732,subQ733,subQ451,subQ734,subQ735,subQ461,subQ591,subQ436,subQ737,subQ738,subQ508,subQ294,subQ739,subQ623,subQ740,subQ741,subQ742,subQ743,subQ523,subQ519,subQ744,subQ604,subQ606,subQ286,subQ746,subQ747,subQ269,subQ449,subQ340,subQ748,subQ749,subQ750,subQ306,subQ751,subQ752,subQ754,subQ355,subQ617,subQ387,subQ756,subQ320,subQ757,subQ312,subQ646,subQ313,subQ758,subQ759,subQ760,subQ329,subQ761,subQ763,subQ629,subQ359,subQ765,subQ766,subQ767,subQ348,subQ768,subQ769,subQ771,subQ772,subQ773,subQ278,subQ774,subQ775,subQ777,subQ434,subQ639,subQ534,subQ779,subQ401,subQ780,subQ561,subQ781,subQ418,subQ782,subQ783,subQ784,subQ301,subQ785,subQ787,subQ651,subQ404,subQ789,subQ790,subQ791,subQ290,subQ792,subQ793,subQ795,subQ796,subQ797,subQ798,subQ799,subQ559,subQ800,subQ802,subQ664,subQ533,subQ803,subQ804,subQ514,subQ805,subQ806,subQ807,subQ425,subQ808,subQ809,subQ472,subQ810,subQ554,subQ812,subQ521,subQ813,subQ814,subQ815,subQ291,subQ364,subQ505,subQ816,subQ817,subQ370,subQ818,subQ422,subQ380,subQ819,subQ820,subQ821,subQ383,subQ822,subQ823,subQ248,subQ824,subQ825,subQ826,subQ482,subQ827,subQ393,subQ304,subQ828,subQ496,subQ405,subQ471,subQ829,subQ830,subQ289,subQ408,subQ538,subQ530,subQ831,subQ832,subQ532,subQ833,subQ235,subQ319,subQ834,subQ478,subQ835,subQ836,subQ374,subQ311,subQ228,subQ837,subQ838,subQ323,subQ839,subQ840,subQ394,subQ221,subQ219,subQ841,subQ842,subQ495,subQ843,subQ844,subQ254,subQ213,subQ845,subQ529,subQ846,subQ346,subQ847,subQ848,subQ207,subQ204,subQ849,subQ850,subQ851,subQ852,subQ442,subQ501,subQ853,subQ854,subQ855,subQ409,subQ856,subQ857,subQ413,subQ190,subQ438,subQ858,subQ859,subQ736,subQ860,subQ861,subQ862,subQ518,subQ863,subQ475,subQ864,subQ453,subQ865,subQ866,subQ391,subQ177,subQ867,subQ868,subQ520,subQ745,subQ427,subQ869,subQ567,subQ870,subQ871,subQ770,subQ872,subQ557,subQ457,subQ161,subQ550,subQ295,subQ873,subQ753,subQ755,subQ874,subQ441,subQ875,subQ265,subQ876,subQ877,subQ878,subQ879,subQ386,subQ500,subQ152,subQ880,subQ881,subQ762,subQ764,subQ882,subQ381,subQ252,subQ883,subQ884,subQ794,subQ885,subQ568,subQ468,subQ142,subQ257,subQ886,subQ887,subQ776,subQ778,subQ296,subQ260,subQ517,subQ243,subQ316,subQ888,subQ889,subQ890,subQ416,subQ274,subQ129,subQ891,subQ892,subQ786,subQ788,subQ893,subQ894,subQ116,subQ526,subQ895,subQ506,subQ896,subQ275,subQ897,subQ113,subQ110,subQ898,subQ899,subQ560,subQ801,subQ293,subQ900,subQ345,subQ106,subQ479,subQ901,subQ448,subQ902,subQ321,subQ903,subQ98,subQ904,subQ905,subQ811,subQ555,subQ906,subQ280,subQ85,subQ83,subQ907,subQ908,subQ909])],"isStart":false})});}
            var sketch = newSketch(context, id + "F5", { "sketchPlane" : qUnion([Q0])});
            skCircle(sketch, "E1354", {"center": v(0, 0) * mm, "radius": 19.52 * mm, "construction": true});
            skCircle(sketch, "E1355", {"center": v(0, 19.52) * mm, "radius": 7.9 * mm});
            skCircle(sketch, "E1356", {"center": v(19.47, 0.03) * mm, "radius": 7.9 * mm});
            skCircle(sketch, "E1357", {"center": v(0.1, -19.35) * mm, "radius": 7.9 * mm});
            skCircle(sketch, "E1358", {"center": v(-19.61, -0.13) * mm, "radius": 7.9 * mm});
            skSolve(sketch);
        }
        {
            var Q0;
            Q0=makeQuery(id+"F5.imprint","IMPRINT",FACE,{"disambiguationData":[TD([[makeQuery(id+"F5.imprint","IMPRINT",EDGE,{"derivedFrom":sQuery(id+"F5.wireOp",EDGE,"E1358")}),1.0]])]});
            var Q1;
            Q1=makeQuery(id+"F5.imprint","IMPRINT",FACE,{"disambiguationData":[TD([[makeQuery(id+"F5.imprint","IMPRINT",EDGE,{"derivedFrom":sQuery(id+"F5.wireOp",EDGE,"E1355")}),1.0]])]});
            var Q2;
            Q2=makeQuery(id+"F5.imprint","IMPRINT",FACE,{"disambiguationData":[TD([[makeQuery(id+"F5.imprint","IMPRINT",EDGE,{"derivedFrom":sQuery(id+"F5.wireOp",EDGE,"E1356")}),1.0]])]});
            var Q3;
            Q3=makeQuery(id+"F5.imprint","IMPRINT",FACE,{"disambiguationData":[TD([[makeQuery(id+"F5.imprint","IMPRINT",EDGE,{"derivedFrom":sQuery(id+"F5.wireOp",EDGE,"E1357")}),1.0]])]});
            extrude(context, id + "F6", {"entities" : qUnion([Q0, Q1, Q2, Q3]), "operationType" : NewBodyOperationType.REMOVE, "endBound" : BoundingType.THROUGH_ALL, "oppositeDirection" : true, "depth" : 25 * mm});
        }
    });
